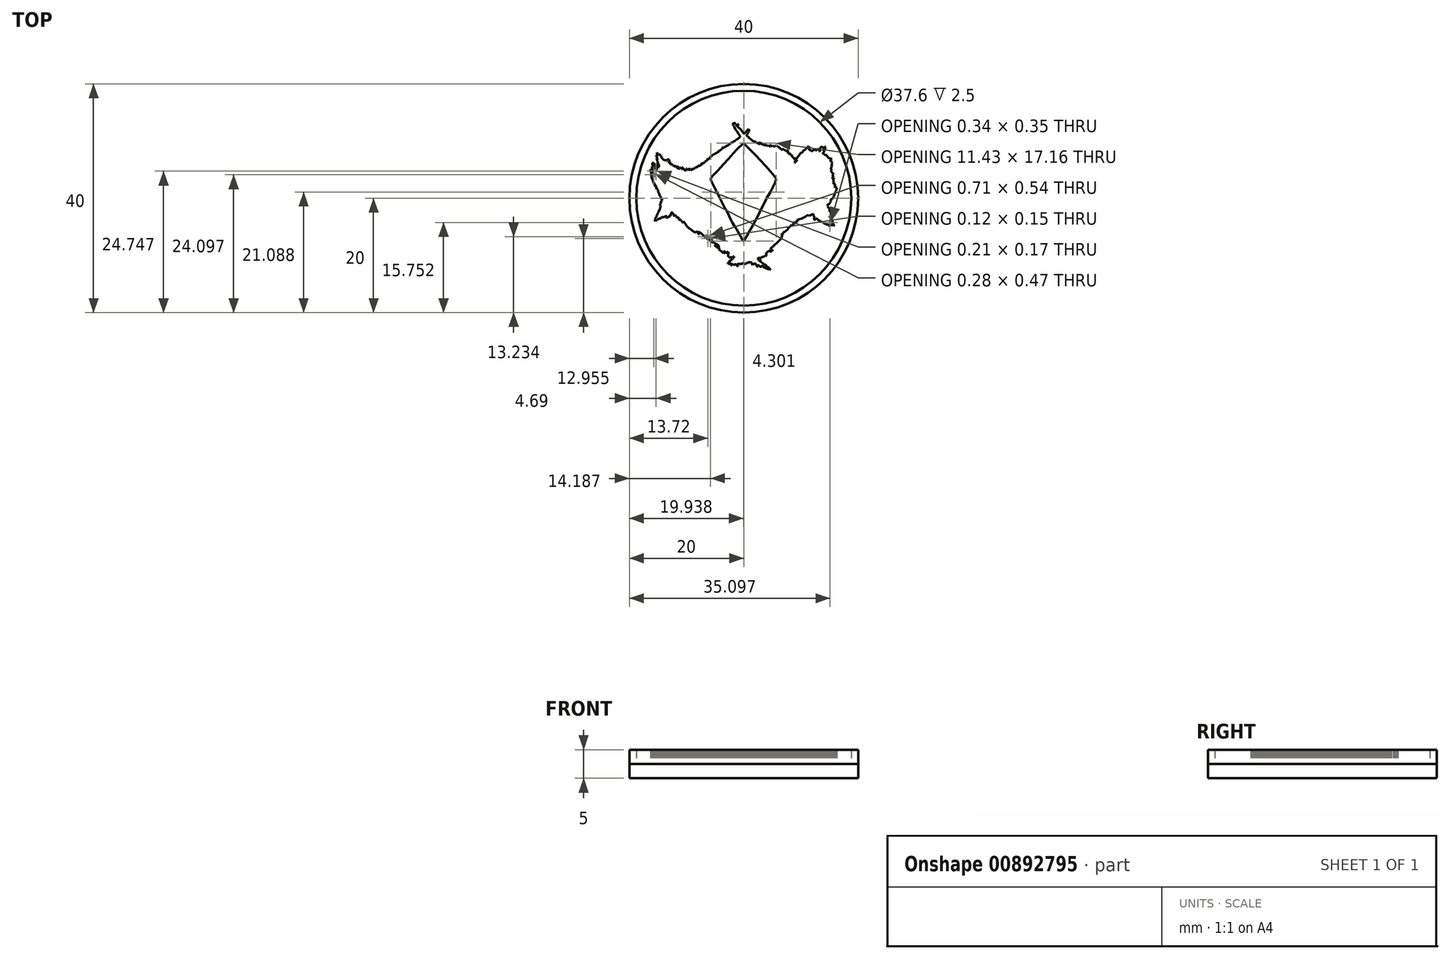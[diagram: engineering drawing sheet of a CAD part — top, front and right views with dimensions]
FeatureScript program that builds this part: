
annotation { "Feature Type Name" : "Feature", "Feature Type Description" : "" }
export const myFeature = defineFeature(function(context is Context, id is Id, definition is map)
    precondition{}
    {
        {
            var Q0;
            Q0=qCreatedBy(makeId("Top.planeOp"),FACE);
            var sketch = newSketch(context, id + "F0", { "sketchPlane" : qUnion([Q0])});
            skCircle(sketch, "E0", {"center": v(0, 0) * mm, "radius": 20 * mm});
            skLineSegment(sketch, "E1", {"start": v(-14.5, 0) * mm, "end": v(-14.54, 0.13) * mm});
            skLineSegment(sketch, "E2", {"start": v(-14.54, 0.13) * mm, "end": v(-14.54, 0.3) * mm});
            skLineSegment(sketch, "E3", {"start": v(-14.54, 0.3) * mm, "end": v(-14.71, 0.46) * mm});
            skLineSegment(sketch, "E4", {"start": v(-14.71, 0.46) * mm, "end": v(-14.74, 0.74) * mm});
            skLineSegment(sketch, "E5", {"start": v(-14.74, 0.74) * mm, "end": v(-14.94, 1.13) * mm});
            skLineSegment(sketch, "E6", {"start": v(-14.94, 1.13) * mm, "end": v(-14.94, 1.38) * mm});
            skLineSegment(sketch, "E7", {"start": v(-14.94, 1.38) * mm, "end": v(-15.19, 1.72) * mm});
            skLineSegment(sketch, "E8", {"start": v(-15.19, 1.72) * mm, "end": v(-15.27, 1.72) * mm});
            skLineSegment(sketch, "E9", {"start": v(-15.27, 1.72) * mm, "end": v(-15.39, 1.88) * mm});
            skLineSegment(sketch, "E10", {"start": v(-15.39, 1.88) * mm, "end": v(-15.39, 1.93) * mm});
            skLineSegment(sketch, "E11", {"start": v(-15.39, 1.93) * mm, "end": v(-15.35, 1.93) * mm});
            skLineSegment(sketch, "E12", {"start": v(-15.35, 1.93) * mm, "end": v(-15.31, 1.9) * mm});
            skLineSegment(sketch, "E13", {"start": v(-15.31, 1.9) * mm, "end": v(-15.28, 1.88) * mm});
            skLineSegment(sketch, "E14", {"start": v(-15.28, 1.88) * mm, "end": v(-15.3, 2) * mm});
            skLineSegment(sketch, "E15", {"start": v(-15.3, 2) * mm, "end": v(-15.39, 2.25) * mm});
            skLineSegment(sketch, "E16", {"start": v(-15.39, 2.25) * mm, "end": v(-15.5, 2.42) * mm});
            skLineSegment(sketch, "E17", {"start": v(-15.5, 2.42) * mm, "end": v(-15.53, 2.38) * mm});
            skLineSegment(sketch, "E18", {"start": v(-15.53, 2.38) * mm, "end": v(-15.5, 2.3) * mm});
            skLineSegment(sketch, "E19", {"start": v(-15.5, 2.3) * mm, "end": v(-15.43, 2.07) * mm});
            skLineSegment(sketch, "E20", {"start": v(-15.43, 2.07) * mm, "end": v(-15.49, 2.1) * mm});
            skLineSegment(sketch, "E21", {"start": v(-15.49, 2.1) * mm, "end": v(-15.77, 2.88) * mm});
            skLineSegment(sketch, "E22", {"start": v(-15.77, 2.88) * mm, "end": v(-16.12, 3.61) * mm});
            skLineSegment(sketch, "E23", {"start": v(-16.12, 3.61) * mm, "end": v(-16.1, 3.73) * mm});
            skLineSegment(sketch, "E24", {"start": v(-16.1, 3.73) * mm, "end": v(-16.09, 3.76) * mm});
            skLineSegment(sketch, "E25", {"start": v(-16.09, 3.76) * mm, "end": v(-16.09, 3.82) * mm});
            skLineSegment(sketch, "E26", {"start": v(-16.09, 3.82) * mm, "end": v(-16.2, 3.97) * mm});
            skLineSegment(sketch, "E27", {"start": v(-16.2, 3.97) * mm, "end": v(-16.2, 4.5) * mm});
            skLineSegment(sketch, "E28", {"start": v(-16.2, 4.5) * mm, "end": v(-16.28, 4.76) * mm});
            skLineSegment(sketch, "E29", {"start": v(-16.28, 4.76) * mm, "end": v(-16.3, 4.82) * mm});
            skLineSegment(sketch, "E30", {"start": v(-16.3, 4.82) * mm, "end": v(-16.26, 4.9) * mm});
            skLineSegment(sketch, "E31", {"start": v(-16.26, 4.9) * mm, "end": v(-16.21, 5.05) * mm});
            skLineSegment(sketch, "E32", {"start": v(-16.21, 5.05) * mm, "end": v(-16.16, 5.08) * mm});
            skLineSegment(sketch, "E33", {"start": v(-16.16, 5.08) * mm, "end": v(-16.07, 5.08) * mm});
            skLineSegment(sketch, "E34", {"start": v(-16.07, 5.08) * mm, "end": v(-16.02, 5.06) * mm});
            skLineSegment(sketch, "E35", {"start": v(-16.02, 5.06) * mm, "end": v(-16, 4.99) * mm});
            skLineSegment(sketch, "E36", {"start": v(-16, 4.99) * mm, "end": v(-16, 4.8) * mm});
            skLineSegment(sketch, "E37", {"start": v(-16, 4.8) * mm, "end": v(-16, 4.68) * mm});
            skLineSegment(sketch, "E38", {"start": v(-16, 4.68) * mm, "end": v(-15.94, 4.57) * mm});
            skLineSegment(sketch, "E39", {"start": v(-15.94, 4.57) * mm, "end": v(-15.87, 4.5) * mm});
            skLineSegment(sketch, "E40", {"start": v(-15.87, 4.5) * mm, "end": v(-15.84, 4.45) * mm});
            skLineSegment(sketch, "E41", {"start": v(-15.84, 4.45) * mm, "end": v(-15.81, 4.44) * mm});
            skLineSegment(sketch, "E42", {"start": v(-15.81, 4.44) * mm, "end": v(-15.8, 4.45) * mm});
            skLineSegment(sketch, "E43", {"start": v(-15.8, 4.45) * mm, "end": v(-15.8, 4.5) * mm});
            skLineSegment(sketch, "E44", {"start": v(-15.8, 4.5) * mm, "end": v(-15.83, 4.56) * mm});
            skLineSegment(sketch, "E45", {"start": v(-15.83, 4.56) * mm, "end": v(-15.87, 4.63) * mm});
            skLineSegment(sketch, "E46", {"start": v(-15.87, 4.63) * mm, "end": v(-15.89, 4.7) * mm});
            skLineSegment(sketch, "E47", {"start": v(-15.89, 4.7) * mm, "end": v(-15.91, 4.95) * mm});
            skLineSegment(sketch, "E48", {"start": v(-15.91, 4.95) * mm, "end": v(-15.94, 5.06) * mm});
            skLineSegment(sketch, "E49", {"start": v(-15.94, 5.06) * mm, "end": v(-16, 5.15) * mm});
            skLineSegment(sketch, "E50", {"start": v(-16, 5.15) * mm, "end": v(-16.11, 5.25) * mm});
            skLineSegment(sketch, "E51", {"start": v(-16.11, 5.25) * mm, "end": v(-16.14, 5.31) * mm});
            skLineSegment(sketch, "E52", {"start": v(-16.14, 5.31) * mm, "end": v(-16.1, 5.37) * mm});
            skLineSegment(sketch, "E53", {"start": v(-16.1, 5.37) * mm, "end": v(-16.06, 5.43) * mm});
            skLineSegment(sketch, "E54", {"start": v(-16.06, 5.43) * mm, "end": v(-16.03, 5.44) * mm});
            skLineSegment(sketch, "E55", {"start": v(-16.03, 5.44) * mm, "end": v(-15.99, 5.44) * mm});
            skLineSegment(sketch, "E56", {"start": v(-15.99, 5.44) * mm, "end": v(-15.97, 5.4) * mm});
            skLineSegment(sketch, "E57", {"start": v(-15.97, 5.4) * mm, "end": v(-15.9, 5.33) * mm});
            skLineSegment(sketch, "E58", {"start": v(-15.9, 5.33) * mm, "end": v(-15.87, 5.3) * mm});
            skLineSegment(sketch, "E59", {"start": v(-15.87, 5.3) * mm, "end": v(-15.84, 5.29) * mm});
            skLineSegment(sketch, "E60", {"start": v(-15.84, 5.29) * mm, "end": v(-15.81, 5.28) * mm});
            skLineSegment(sketch, "E61", {"start": v(-15.81, 5.28) * mm, "end": v(-15.78, 5.3) * mm});
            skLineSegment(sketch, "E62", {"start": v(-15.78, 5.3) * mm, "end": v(-15.77, 5.3) * mm});
            skLineSegment(sketch, "E63", {"start": v(-15.77, 5.3) * mm, "end": v(-15.76, 5.35) * mm});
            skLineSegment(sketch, "E64", {"start": v(-15.76, 5.35) * mm, "end": v(-15.75, 5.43) * mm});
            skLineSegment(sketch, "E65", {"start": v(-15.75, 5.43) * mm, "end": v(-15.73, 5.45) * mm});
            skLineSegment(sketch, "E66", {"start": v(-15.73, 5.45) * mm, "end": v(-15.72, 5.48) * mm});
            skLineSegment(sketch, "E67", {"start": v(-15.72, 5.48) * mm, "end": v(-15.72, 5.51) * mm});
            skLineSegment(sketch, "E68", {"start": v(-15.72, 5.51) * mm, "end": v(-15.72, 5.54) * mm});
            skLineSegment(sketch, "E69", {"start": v(-15.72, 5.54) * mm, "end": v(-15.73, 5.58) * mm});
            skLineSegment(sketch, "E70", {"start": v(-15.73, 5.58) * mm, "end": v(-15.78, 5.62) * mm});
            skLineSegment(sketch, "E71", {"start": v(-15.78, 5.62) * mm, "end": v(-15.84, 5.67) * mm});
            skLineSegment(sketch, "E72", {"start": v(-15.84, 5.67) * mm, "end": v(-15.9, 5.7) * mm});
            skLineSegment(sketch, "E73", {"start": v(-15.9, 5.7) * mm, "end": v(-15.93, 5.74) * mm});
            skLineSegment(sketch, "E74", {"start": v(-15.93, 5.74) * mm, "end": v(-15.95, 5.78) * mm});
            skLineSegment(sketch, "E75", {"start": v(-15.95, 5.78) * mm, "end": v(-15.98, 5.84) * mm});
            skLineSegment(sketch, "E76", {"start": v(-15.98, 5.84) * mm, "end": v(-15.99, 5.89) * mm});
            skLineSegment(sketch, "E77", {"start": v(-15.99, 5.89) * mm, "end": v(-16, 5.94) * mm});
            skLineSegment(sketch, "E78", {"start": v(-16, 5.94) * mm, "end": v(-16, 5.98) * mm});
            skLineSegment(sketch, "E79", {"start": v(-16, 5.98) * mm, "end": v(-15.99, 6.03) * mm});
            skLineSegment(sketch, "E80", {"start": v(-15.99, 6.03) * mm, "end": v(-15.97, 6.08) * mm});
            skLineSegment(sketch, "E81", {"start": v(-15.97, 6.08) * mm, "end": v(-15.95, 6.13) * mm});
            skLineSegment(sketch, "E82", {"start": v(-15.95, 6.13) * mm, "end": v(-15.95, 6.16) * mm});
            skLineSegment(sketch, "E83", {"start": v(-15.95, 6.16) * mm, "end": v(-15.93, 6.18) * mm});
            skLineSegment(sketch, "E84", {"start": v(-15.93, 6.18) * mm, "end": v(-15.9, 6.2) * mm});
            skLineSegment(sketch, "E85", {"start": v(-15.9, 6.2) * mm, "end": v(-15.87, 6.2) * mm});
            skLineSegment(sketch, "E86", {"start": v(-15.87, 6.2) * mm, "end": v(-15.84, 6.19) * mm});
            skLineSegment(sketch, "E87", {"start": v(-15.84, 6.19) * mm, "end": v(-15.83, 6.18) * mm});
            skLineSegment(sketch, "E88", {"start": v(-15.83, 6.18) * mm, "end": v(-15.79, 6.16) * mm});
            skLineSegment(sketch, "E89", {"start": v(-15.79, 6.16) * mm, "end": v(-15.73, 6.12) * mm});
            skLineSegment(sketch, "E90", {"start": v(-15.73, 6.12) * mm, "end": v(-15.68, 6.09) * mm});
            skLineSegment(sketch, "E91", {"start": v(-15.68, 6.09) * mm, "end": v(-15.64, 6.05) * mm});
            skLineSegment(sketch, "E92", {"start": v(-15.64, 6.05) * mm, "end": v(-15.6, 6.01) * mm});
            skLineSegment(sketch, "E93", {"start": v(-15.6, 6.01) * mm, "end": v(-15.58, 5.97) * mm});
            skLineSegment(sketch, "E94", {"start": v(-15.58, 5.97) * mm, "end": v(-15.57, 5.92) * mm});
            skLineSegment(sketch, "E95", {"start": v(-15.57, 5.92) * mm, "end": v(-15.57, 5.86) * mm});
            skLineSegment(sketch, "E96", {"start": v(-15.57, 5.86) * mm, "end": v(-15.58, 5.79) * mm});
            skLineSegment(sketch, "E97", {"start": v(-15.58, 5.79) * mm, "end": v(-15.6, 5.74) * mm});
            skLineSegment(sketch, "E98", {"start": v(-15.6, 5.74) * mm, "end": v(-15.62, 5.7) * mm});
            skLineSegment(sketch, "E99", {"start": v(-15.62, 5.7) * mm, "end": v(-15.63, 5.63) * mm});
            skLineSegment(sketch, "E100", {"start": v(-15.63, 5.63) * mm, "end": v(-15.63, 5.6) * mm});
            skLineSegment(sketch, "E101", {"start": v(-15.63, 5.6) * mm, "end": v(-15.62, 5.57) * mm});
            skLineSegment(sketch, "E102", {"start": v(-15.62, 5.57) * mm, "end": v(-15.61, 5.52) * mm});
            skLineSegment(sketch, "E103", {"start": v(-15.61, 5.52) * mm, "end": v(-15.62, 5.45) * mm});
            skLineSegment(sketch, "E104", {"start": v(-15.62, 5.45) * mm, "end": v(-15.6, 5.4) * mm});
            skLineSegment(sketch, "E105", {"start": v(-15.6, 5.4) * mm, "end": v(-15.58, 5.38) * mm});
            skLineSegment(sketch, "E106", {"start": v(-15.58, 5.38) * mm, "end": v(-15.57, 5.36) * mm});
            skLineSegment(sketch, "E107", {"start": v(-15.57, 5.36) * mm, "end": v(-15.55, 5.35) * mm});
            skLineSegment(sketch, "E108", {"start": v(-15.55, 5.35) * mm, "end": v(-15.58, 5.34) * mm});
            skLineSegment(sketch, "E109", {"start": v(-15.58, 5.34) * mm, "end": v(-15.59, 5.33) * mm});
            skLineSegment(sketch, "E110", {"start": v(-15.59, 5.33) * mm, "end": v(-15.6, 5.3) * mm});
            skLineSegment(sketch, "E111", {"start": v(-15.6, 5.3) * mm, "end": v(-15.58, 5.28) * mm});
            skLineSegment(sketch, "E112", {"start": v(-15.58, 5.28) * mm, "end": v(-15.57, 5.27) * mm});
            skLineSegment(sketch, "E113", {"start": v(-15.57, 5.27) * mm, "end": v(-15.55, 5.26) * mm});
            skLineSegment(sketch, "E114", {"start": v(-15.55, 5.26) * mm, "end": v(-15.54, 5.27) * mm});
            skLineSegment(sketch, "E115", {"start": v(-15.54, 5.27) * mm, "end": v(-15.53, 5.27) * mm});
            skLineSegment(sketch, "E116", {"start": v(-15.53, 5.27) * mm, "end": v(-15.52, 5.3) * mm});
            skLineSegment(sketch, "E117", {"start": v(-15.52, 5.3) * mm, "end": v(-15.52, 5.3) * mm});
            skLineSegment(sketch, "E118", {"start": v(-15.52, 5.3) * mm, "end": v(-15.5, 5.3) * mm});
            skLineSegment(sketch, "E119", {"start": v(-15.5, 5.3) * mm, "end": v(-15.5, 5.3) * mm});
            skLineSegment(sketch, "E120", {"start": v(-15.5, 5.3) * mm, "end": v(-15.49, 5.28) * mm});
            skLineSegment(sketch, "E121", {"start": v(-15.49, 5.28) * mm, "end": v(-15.48, 5.28) * mm});
            skLineSegment(sketch, "E122", {"start": v(-15.48, 5.28) * mm, "end": v(-15.46, 5.27) * mm});
            skLineSegment(sketch, "E123", {"start": v(-15.46, 5.27) * mm, "end": v(-15.46, 5.26) * mm});
            skLineSegment(sketch, "E124", {"start": v(-15.46, 5.26) * mm, "end": v(-15.44, 5.23) * mm});
            skLineSegment(sketch, "E125", {"start": v(-15.44, 5.23) * mm, "end": v(-15.42, 5.22) * mm});
            skLineSegment(sketch, "E126", {"start": v(-15.42, 5.22) * mm, "end": v(-15.4, 5.1) * mm});
            skLineSegment(sketch, "E127", {"start": v(-15.4, 5.1) * mm, "end": v(-15.39, 5.05) * mm});
            skLineSegment(sketch, "E128", {"start": v(-15.39, 5.05) * mm, "end": v(-15.37, 5.03) * mm});
            skLineSegment(sketch, "E129", {"start": v(-15.37, 5.03) * mm, "end": v(-15.35, 5.02) * mm});
            skLineSegment(sketch, "E130", {"start": v(-15.35, 5.02) * mm, "end": v(-15.32, 5.03) * mm});
            skLineSegment(sketch, "E131", {"start": v(-15.32, 5.03) * mm, "end": v(-15.32, 5.04) * mm});
            skLineSegment(sketch, "E132", {"start": v(-15.32, 5.04) * mm, "end": v(-15.32, 5.06) * mm});
            skLineSegment(sketch, "E133", {"start": v(-15.32, 5.06) * mm, "end": v(-15.34, 5.06) * mm});
            skLineSegment(sketch, "E134", {"start": v(-15.34, 5.06) * mm, "end": v(-15.35, 5.07) * mm});
            skLineSegment(sketch, "E135", {"start": v(-15.35, 5.07) * mm, "end": v(-15.35, 5.08) * mm});
            skLineSegment(sketch, "E136", {"start": v(-15.35, 5.08) * mm, "end": v(-15.35, 5.1) * mm});
            skLineSegment(sketch, "E137", {"start": v(-15.35, 5.1) * mm, "end": v(-15.33, 5.1) * mm});
            skLineSegment(sketch, "E138", {"start": v(-15.33, 5.1) * mm, "end": v(-15.3, 5.1) * mm});
            skLineSegment(sketch, "E139", {"start": v(-15.3, 5.1) * mm, "end": v(-15.3, 5.09) * mm});
            skLineSegment(sketch, "E140", {"start": v(-15.3, 5.09) * mm, "end": v(-15.28, 5.08) * mm});
            skLineSegment(sketch, "E141", {"start": v(-15.28, 5.08) * mm, "end": v(-15.27, 5.06) * mm});
            skLineSegment(sketch, "E142", {"start": v(-15.27, 5.06) * mm, "end": v(-15.25, 5.06) * mm});
            skLineSegment(sketch, "E143", {"start": v(-15.25, 5.06) * mm, "end": v(-15.23, 5.05) * mm});
            skLineSegment(sketch, "E144", {"start": v(-15.23, 5.05) * mm, "end": v(-15.21, 5.03) * mm});
            skLineSegment(sketch, "E145", {"start": v(-15.21, 5.03) * mm, "end": v(-15.2, 5.02) * mm});
            skLineSegment(sketch, "E146", {"start": v(-15.2, 5.02) * mm, "end": v(-15.15, 5.02) * mm});
            skLineSegment(sketch, "E147", {"start": v(-15.15, 5.02) * mm, "end": v(-15.14, 5.02) * mm});
            skLineSegment(sketch, "E148", {"start": v(-15.14, 5.02) * mm, "end": v(-15.13, 5.04) * mm});
            skLineSegment(sketch, "E149", {"start": v(-15.13, 5.04) * mm, "end": v(-15.13, 5.05) * mm});
            skLineSegment(sketch, "E150", {"start": v(-15.13, 5.05) * mm, "end": v(-15.13, 5.07) * mm});
            skLineSegment(sketch, "E151", {"start": v(-15.13, 5.07) * mm, "end": v(-15.14, 5.08) * mm});
            skLineSegment(sketch, "E152", {"start": v(-15.14, 5.08) * mm, "end": v(-15.15, 5.1) * mm});
            skLineSegment(sketch, "E153", {"start": v(-15.15, 5.1) * mm, "end": v(-15.19, 5.12) * mm});
            skLineSegment(sketch, "E154", {"start": v(-15.19, 5.12) * mm, "end": v(-15.2, 5.14) * mm});
            skLineSegment(sketch, "E155", {"start": v(-15.2, 5.14) * mm, "end": v(-15.2, 5.18) * mm});
            skLineSegment(sketch, "E156", {"start": v(-15.2, 5.18) * mm, "end": v(-15.2, 5.22) * mm});
            skLineSegment(sketch, "E157", {"start": v(-15.2, 5.22) * mm, "end": v(-15.2, 5.25) * mm});
            skLineSegment(sketch, "E158", {"start": v(-15.2, 5.25) * mm, "end": v(-15.2, 5.28) * mm});
            skLineSegment(sketch, "E159", {"start": v(-15.2, 5.28) * mm, "end": v(-15.2, 5.3) * mm});
            skLineSegment(sketch, "E160", {"start": v(-15.2, 5.3) * mm, "end": v(-15.24, 5.36) * mm});
            skLineSegment(sketch, "E161", {"start": v(-15.24, 5.36) * mm, "end": v(-15.26, 5.4) * mm});
            skLineSegment(sketch, "E162", {"start": v(-15.26, 5.4) * mm, "end": v(-15.28, 5.47) * mm});
            skLineSegment(sketch, "E163", {"start": v(-15.28, 5.47) * mm, "end": v(-15.3, 5.53) * mm});
            skLineSegment(sketch, "E164", {"start": v(-15.3, 5.53) * mm, "end": v(-15.3, 5.56) * mm});
            skLineSegment(sketch, "E165", {"start": v(-15.3, 5.56) * mm, "end": v(-15.33, 5.6) * mm});
            skLineSegment(sketch, "E166", {"start": v(-15.33, 5.6) * mm, "end": v(-15.34, 5.63) * mm});
            skLineSegment(sketch, "E167", {"start": v(-15.34, 5.63) * mm, "end": v(-15.34, 5.66) * mm});
            skLineSegment(sketch, "E168", {"start": v(-15.34, 5.66) * mm, "end": v(-15.33, 5.69) * mm});
            skLineSegment(sketch, "E169", {"start": v(-15.33, 5.69) * mm, "end": v(-15.32, 5.7) * mm});
            skLineSegment(sketch, "E170", {"start": v(-15.32, 5.7) * mm, "end": v(-15.28, 5.73) * mm});
            skLineSegment(sketch, "E171", {"start": v(-15.28, 5.73) * mm, "end": v(-15.25, 5.75) * mm});
            skLineSegment(sketch, "E172", {"start": v(-15.25, 5.75) * mm, "end": v(-15.19, 5.75) * mm});
            skLineSegment(sketch, "E173", {"start": v(-15.19, 5.75) * mm, "end": v(-15.17, 5.75) * mm});
            skLineSegment(sketch, "E174", {"start": v(-15.17, 5.75) * mm, "end": v(-15.13, 5.72) * mm});
            skLineSegment(sketch, "E175", {"start": v(-15.13, 5.72) * mm, "end": v(-15.12, 5.7) * mm});
            skLineSegment(sketch, "E176", {"start": v(-15.12, 5.7) * mm, "end": v(-15.1, 5.62) * mm});
            skLineSegment(sketch, "E177", {"start": v(-15.1, 5.62) * mm, "end": v(-15.09, 5.59) * mm});
            skLineSegment(sketch, "E178", {"start": v(-15.09, 5.59) * mm, "end": v(-15.03, 5.53) * mm});
            skLineSegment(sketch, "E179", {"start": v(-15.03, 5.53) * mm, "end": v(-14.97, 5.52) * mm});
            skLineSegment(sketch, "E180", {"start": v(-14.97, 5.52) * mm, "end": v(-14.9, 5.47) * mm});
            skLineSegment(sketch, "E181", {"start": v(-14.9, 5.47) * mm, "end": v(-14.85, 5.44) * mm});
            skLineSegment(sketch, "E182", {"start": v(-14.85, 5.44) * mm, "end": v(-14.8, 5.43) * mm});
            skLineSegment(sketch, "E183", {"start": v(-14.8, 5.43) * mm, "end": v(-14.8, 5.44) * mm});
            skLineSegment(sketch, "E184", {"start": v(-14.8, 5.44) * mm, "end": v(-14.8, 5.6) * mm});
            skLineSegment(sketch, "E185", {"start": v(-14.8, 5.6) * mm, "end": v(-14.84, 5.75) * mm});
            skLineSegment(sketch, "E186", {"start": v(-14.84, 5.75) * mm, "end": v(-14.9, 5.92) * mm});
            skLineSegment(sketch, "E187", {"start": v(-14.9, 5.92) * mm, "end": v(-14.94, 6.02) * mm});
            skLineSegment(sketch, "E188", {"start": v(-14.94, 6.02) * mm, "end": v(-15, 6.16) * mm});
            skLineSegment(sketch, "E189", {"start": v(-15, 6.16) * mm, "end": v(-15.03, 6.2) * mm});
            skLineSegment(sketch, "E190", {"start": v(-15.03, 6.2) * mm, "end": v(-15.04, 6.28) * mm});
            skLineSegment(sketch, "E191", {"start": v(-15.04, 6.28) * mm, "end": v(-15.03, 6.33) * mm});
            skLineSegment(sketch, "E192", {"start": v(-15.03, 6.33) * mm, "end": v(-15.04, 6.4) * mm});
            skLineSegment(sketch, "E193", {"start": v(-15.04, 6.4) * mm, "end": v(-15.07, 6.45) * mm});
            skLineSegment(sketch, "E194", {"start": v(-15.07, 6.45) * mm, "end": v(-15.13, 6.51) * mm});
            skLineSegment(sketch, "E195", {"start": v(-15.13, 6.51) * mm, "end": v(-15.14, 6.56) * mm});
            skLineSegment(sketch, "E196", {"start": v(-15.14, 6.56) * mm, "end": v(-15.15, 6.71) * mm});
            skLineSegment(sketch, "E197", {"start": v(-15.15, 6.71) * mm, "end": v(-15.16, 6.78) * mm});
            skLineSegment(sketch, "E198", {"start": v(-15.16, 6.78) * mm, "end": v(-15.19, 6.82) * mm});
            skLineSegment(sketch, "E199", {"start": v(-15.19, 6.82) * mm, "end": v(-15.2, 6.86) * mm});
            skLineSegment(sketch, "E200", {"start": v(-15.2, 6.86) * mm, "end": v(-15.2, 6.87) * mm});
            skLineSegment(sketch, "E201", {"start": v(-15.2, 6.87) * mm, "end": v(-15.19, 6.89) * mm});
            skLineSegment(sketch, "E202", {"start": v(-15.19, 6.89) * mm, "end": v(-15.16, 6.89) * mm});
            skLineSegment(sketch, "E203", {"start": v(-15.16, 6.89) * mm, "end": v(-15.15, 6.84) * mm});
            skLineSegment(sketch, "E204", {"start": v(-15.15, 6.84) * mm, "end": v(-15.13, 6.83) * mm});
            skLineSegment(sketch, "E205", {"start": v(-15.13, 6.83) * mm, "end": v(-15.1, 6.8) * mm});
            skLineSegment(sketch, "E206", {"start": v(-15.1, 6.8) * mm, "end": v(-15.1, 6.8) * mm});
            skLineSegment(sketch, "E207", {"start": v(-15.1, 6.8) * mm, "end": v(-15.09, 6.8) * mm});
            skLineSegment(sketch, "E208", {"start": v(-15.09, 6.8) * mm, "end": v(-15.09, 6.82) * mm});
            skLineSegment(sketch, "E209", {"start": v(-15.09, 6.82) * mm, "end": v(-15.09, 6.84) * mm});
            skLineSegment(sketch, "E210", {"start": v(-15.09, 6.84) * mm, "end": v(-15.1, 6.86) * mm});
            skLineSegment(sketch, "E211", {"start": v(-15.1, 6.86) * mm, "end": v(-15.12, 6.89) * mm});
            skLineSegment(sketch, "E212", {"start": v(-15.12, 6.89) * mm, "end": v(-15.17, 6.99) * mm});
            skLineSegment(sketch, "E213", {"start": v(-15.17, 6.99) * mm, "end": v(-15.2, 7.14) * mm});
            skLineSegment(sketch, "E214", {"start": v(-15.2, 7.14) * mm, "end": v(-15.24, 7.29) * mm});
            skLineSegment(sketch, "E215", {"start": v(-15.24, 7.29) * mm, "end": v(-15.26, 7.35) * mm});
            skLineSegment(sketch, "E216", {"start": v(-15.26, 7.35) * mm, "end": v(-15.3, 7.42) * mm});
            skLineSegment(sketch, "E217", {"start": v(-15.3, 7.42) * mm, "end": v(-15.33, 7.43) * mm});
            skLineSegment(sketch, "E218", {"start": v(-15.33, 7.43) * mm, "end": v(-15.32, 7.46) * mm});
            skLineSegment(sketch, "E219", {"start": v(-15.32, 7.46) * mm, "end": v(-15.28, 7.47) * mm});
            skLineSegment(sketch, "E220", {"start": v(-15.28, 7.47) * mm, "end": v(-15.22, 7.4) * mm});
            skLineSegment(sketch, "E221", {"start": v(-15.22, 7.4) * mm, "end": v(-15.18, 7.4) * mm});
            skLineSegment(sketch, "E222", {"start": v(-15.18, 7.4) * mm, "end": v(-15.14, 7.44) * mm});
            skLineSegment(sketch, "E223", {"start": v(-15.14, 7.44) * mm, "end": v(-15.1, 7.46) * mm});
            skLineSegment(sketch, "E224", {"start": v(-15.1, 7.46) * mm, "end": v(-15.1, 7.54) * mm});
            skLineSegment(sketch, "E225", {"start": v(-15.1, 7.54) * mm, "end": v(-15.13, 7.6) * mm});
            skLineSegment(sketch, "E226", {"start": v(-15.13, 7.6) * mm, "end": v(-15.17, 7.72) * mm});
            skLineSegment(sketch, "E227", {"start": v(-15.17, 7.72) * mm, "end": v(-15.17, 7.81) * mm});
            skLineSegment(sketch, "E228", {"start": v(-15.17, 7.81) * mm, "end": v(-15.22, 7.88) * mm});
            skLineSegment(sketch, "E229", {"start": v(-15.22, 7.88) * mm, "end": v(-15.2, 7.91) * mm});
            skLineSegment(sketch, "E230", {"start": v(-15.2, 7.91) * mm, "end": v(-15.12, 7.86) * mm});
            skLineSegment(sketch, "E231", {"start": v(-15.12, 7.86) * mm, "end": v(-15.01, 7.78) * mm});
            skLineSegment(sketch, "E232", {"start": v(-15.01, 7.78) * mm, "end": v(-14.94, 7.7) * mm});
            skLineSegment(sketch, "E233", {"start": v(-14.94, 7.7) * mm, "end": v(-14.89, 7.63) * mm});
            skLineSegment(sketch, "E234", {"start": v(-14.89, 7.63) * mm, "end": v(-14.86, 7.62) * mm});
            skLineSegment(sketch, "E235", {"start": v(-14.86, 7.62) * mm, "end": v(-14.86, 7.67) * mm});
            skLineSegment(sketch, "E236", {"start": v(-14.86, 7.67) * mm, "end": v(-14.84, 7.69) * mm});
            skLineSegment(sketch, "E237", {"start": v(-15.81, 4.21) * mm, "end": v(-15.84, 4.26) * mm});
            skLineSegment(sketch, "E238", {"start": v(-15.84, 4.26) * mm, "end": v(-15.84, 4.3) * mm});
            skLineSegment(sketch, "E239", {"start": v(-15.84, 4.3) * mm, "end": v(-15.8, 4.33) * mm});
            skLineSegment(sketch, "E240", {"start": v(-15.8, 4.33) * mm, "end": v(-15.75, 4.31) * mm});
            skLineSegment(sketch, "E241", {"start": v(-15.75, 4.31) * mm, "end": v(-15.67, 4.2) * mm});
            skLineSegment(sketch, "E242", {"start": v(-15.67, 4.2) * mm, "end": v(-15.6, 4.03) * mm});
            skLineSegment(sketch, "E243", {"start": v(-15.6, 4.03) * mm, "end": v(-15.56, 3.86) * mm});
            skLineSegment(sketch, "E244", {"start": v(-15.56, 3.86) * mm, "end": v(-15.59, 3.87) * mm});
            skLineSegment(sketch, "E245", {"start": v(-15.59, 3.87) * mm, "end": v(-15.68, 4.04) * mm});
            skLineSegment(sketch, "E246", {"start": v(-15.68, 4.04) * mm, "end": v(-15.74, 4.13) * mm});
            skLineSegment(sketch, "E247", {"start": v(-15.74, 4.13) * mm, "end": v(-15.79, 4.18) * mm});
            skLineSegment(sketch, "E248", {"start": v(-15.79, 4.18) * mm, "end": v(-15.81, 4.21) * mm});
            skLineSegment(sketch, "E249", {"start": v(-15.21, 4.66) * mm, "end": v(-15.33, 4.67) * mm});
            skLineSegment(sketch, "E250", {"start": v(-15.33, 4.67) * mm, "end": v(-15.39, 4.7) * mm});
            skLineSegment(sketch, "E251", {"start": v(-15.39, 4.7) * mm, "end": v(-15.41, 4.74) * mm});
            skLineSegment(sketch, "E252", {"start": v(-15.41, 4.74) * mm, "end": v(-15.41, 4.8) * mm});
            skLineSegment(sketch, "E253", {"start": v(-15.41, 4.8) * mm, "end": v(-15.39, 4.83) * mm});
            skLineSegment(sketch, "E254", {"start": v(-15.39, 4.83) * mm, "end": v(-15.32, 4.83) * mm});
            skLineSegment(sketch, "E255", {"start": v(-15.32, 4.83) * mm, "end": v(-15.28, 4.8) * mm});
            skLineSegment(sketch, "E256", {"start": v(-15.28, 4.8) * mm, "end": v(-15.24, 4.75) * mm});
            skLineSegment(sketch, "E257", {"start": v(-15.24, 4.75) * mm, "end": v(-15.2, 4.7) * mm});
            skLineSegment(sketch, "E258", {"start": v(-15.2, 4.7) * mm, "end": v(-15.21, 4.66) * mm});
            skLineSegment(sketch, "E259", {"start": v(-14.84, 7.69) * mm, "end": v(-14.78, 7.6) * mm});
            skLineSegment(sketch, "E260", {"start": v(-14.78, 7.6) * mm, "end": v(-14.75, 7.62) * mm});
            skLineSegment(sketch, "E261", {"start": v(-14.75, 7.62) * mm, "end": v(-14.77, 7.69) * mm});
            skLineSegment(sketch, "E262", {"start": v(-14.77, 7.69) * mm, "end": v(-14.74, 7.7) * mm});
            skLineSegment(sketch, "E263", {"start": v(-14.74, 7.7) * mm, "end": v(-14.68, 7.66) * mm});
            skLineSegment(sketch, "E264", {"start": v(-14.68, 7.66) * mm, "end": v(-14.6, 7.58) * mm});
            skLineSegment(sketch, "E265", {"start": v(-14.6, 7.58) * mm, "end": v(-14.58, 7.5) * mm});
            skLineSegment(sketch, "E266", {"start": v(-14.58, 7.5) * mm, "end": v(-14.48, 7.38) * mm});
            skLineSegment(sketch, "E267", {"start": v(-14.48, 7.38) * mm, "end": v(-14.43, 7.35) * mm});
            skLineSegment(sketch, "E268", {"start": v(-14.43, 7.35) * mm, "end": v(-14.4, 7.26) * mm});
            skLineSegment(sketch, "E269", {"start": v(-14.4, 7.26) * mm, "end": v(-14.32, 7.1) * mm});
            skLineSegment(sketch, "E270", {"start": v(-14.32, 7.1) * mm, "end": v(-14.28, 7) * mm});
            skLineSegment(sketch, "E271", {"start": v(-14.28, 7) * mm, "end": v(-14.22, 6.97) * mm});
            skLineSegment(sketch, "E272", {"start": v(-14.22, 6.97) * mm, "end": v(-14.19, 6.87) * mm});
            skLineSegment(sketch, "E273", {"start": v(-14.19, 6.87) * mm, "end": v(-14.13, 6.8) * mm});
            skLineSegment(sketch, "E274", {"start": v(-14.13, 6.8) * mm, "end": v(-14.02, 6.8) * mm});
            skLineSegment(sketch, "E275", {"start": v(-14.02, 6.8) * mm, "end": v(-14, 6.76) * mm});
            skLineSegment(sketch, "E276", {"start": v(-14, 6.76) * mm, "end": v(-14.03, 6.72) * mm});
            skLineSegment(sketch, "E277", {"start": v(-14.03, 6.72) * mm, "end": v(-14, 6.68) * mm});
            skLineSegment(sketch, "E278", {"start": v(-14, 6.68) * mm, "end": v(-13.97, 6.64) * mm});
            skLineSegment(sketch, "E279", {"start": v(-13.97, 6.64) * mm, "end": v(-13.93, 6.65) * mm});
            skLineSegment(sketch, "E280", {"start": v(-13.93, 6.65) * mm, "end": v(-13.88, 6.7) * mm});
            skLineSegment(sketch, "E281", {"start": v(-13.88, 6.7) * mm, "end": v(-13.8, 6.73) * mm});
            skLineSegment(sketch, "E282", {"start": v(-13.8, 6.73) * mm, "end": v(-13.78, 6.77) * mm});
            skLineSegment(sketch, "E283", {"start": v(-13.78, 6.77) * mm, "end": v(-13.73, 6.78) * mm});
            skLineSegment(sketch, "E284", {"start": v(-13.73, 6.78) * mm, "end": v(-13.7, 6.73) * mm});
            skLineSegment(sketch, "E285", {"start": v(-13.7, 6.73) * mm, "end": v(-13.66, 6.67) * mm});
            skLineSegment(sketch, "E286", {"start": v(-13.66, 6.67) * mm, "end": v(-13.62, 6.62) * mm});
            skLineSegment(sketch, "E287", {"start": v(-13.62, 6.62) * mm, "end": v(-13.58, 6.6) * mm});
            skLineSegment(sketch, "E288", {"start": v(-13.58, 6.6) * mm, "end": v(-13.56, 6.62) * mm});
            skLineSegment(sketch, "E289", {"start": v(-13.56, 6.62) * mm, "end": v(-13.55, 6.76) * mm});
            skLineSegment(sketch, "E290", {"start": v(-13.55, 6.76) * mm, "end": v(-13.5, 6.77) * mm});
            skLineSegment(sketch, "E291", {"start": v(-13.5, 6.77) * mm, "end": v(-13.47, 6.73) * mm});
            skLineSegment(sketch, "E292", {"start": v(-13.47, 6.73) * mm, "end": v(-13.44, 6.67) * mm});
            skLineSegment(sketch, "E293", {"start": v(-13.44, 6.67) * mm, "end": v(-13.43, 6.63) * mm});
            skLineSegment(sketch, "E294", {"start": v(-13.43, 6.63) * mm, "end": v(-13.4, 6.62) * mm});
            skLineSegment(sketch, "E295", {"start": v(-13.4, 6.62) * mm, "end": v(-13.39, 6.63) * mm});
            skLineSegment(sketch, "E296", {"start": v(-13.39, 6.63) * mm, "end": v(-13.38, 6.72) * mm});
            skLineSegment(sketch, "E297", {"start": v(-13.38, 6.72) * mm, "end": v(-13.36, 6.73) * mm});
            skLineSegment(sketch, "E298", {"start": v(-13.36, 6.73) * mm, "end": v(-13.36, 6.75) * mm});
            skLineSegment(sketch, "E299", {"start": v(-13.36, 6.75) * mm, "end": v(-13.39, 6.79) * mm});
            skLineSegment(sketch, "E300", {"start": v(-13.39, 6.79) * mm, "end": v(-13.4, 6.82) * mm});
            skLineSegment(sketch, "E301", {"start": v(-13.4, 6.82) * mm, "end": v(-13.38, 6.84) * mm});
            skLineSegment(sketch, "E302", {"start": v(-13.38, 6.84) * mm, "end": v(-13.31, 6.77) * mm});
            skLineSegment(sketch, "E303", {"start": v(-13.31, 6.77) * mm, "end": v(-13.28, 6.79) * mm});
            skLineSegment(sketch, "E304", {"start": v(-13.28, 6.79) * mm, "end": v(-13.24, 6.8) * mm});
            skLineSegment(sketch, "E305", {"start": v(-13.24, 6.8) * mm, "end": v(-13.18, 6.78) * mm});
            skLineSegment(sketch, "E306", {"start": v(-13.18, 6.78) * mm, "end": v(-13.16, 6.76) * mm});
            skLineSegment(sketch, "E307", {"start": v(-13.16, 6.76) * mm, "end": v(-13.12, 6.77) * mm});
            skLineSegment(sketch, "E308", {"start": v(-13.12, 6.77) * mm, "end": v(-13.09, 6.8) * mm});
            skLineSegment(sketch, "E309", {"start": v(-13.09, 6.8) * mm, "end": v(-13.05, 6.81) * mm});
            skLineSegment(sketch, "E310", {"start": v(-13.05, 6.81) * mm, "end": v(-13.02, 6.78) * mm});
            skLineSegment(sketch, "E311", {"start": v(-13.02, 6.78) * mm, "end": v(-13.04, 6.76) * mm});
            skLineSegment(sketch, "E312", {"start": v(-13.04, 6.76) * mm, "end": v(-13.07, 6.72) * mm});
            skLineSegment(sketch, "E313", {"start": v(-13.07, 6.72) * mm, "end": v(-13.08, 6.7) * mm});
            skLineSegment(sketch, "E314", {"start": v(-13.08, 6.7) * mm, "end": v(-13, 6.6) * mm});
            skLineSegment(sketch, "E315", {"start": v(-13, 6.6) * mm, "end": v(-12.98, 6.57) * mm});
            skLineSegment(sketch, "E316", {"start": v(-12.98, 6.57) * mm, "end": v(-12.95, 6.51) * mm});
            skLineSegment(sketch, "E317", {"start": v(-12.95, 6.51) * mm, "end": v(-12.98, 6.47) * mm});
            skLineSegment(sketch, "E318", {"start": v(-12.98, 6.47) * mm, "end": v(-13.09, 6.46) * mm});
            skLineSegment(sketch, "E319", {"start": v(-13.09, 6.46) * mm, "end": v(-13.11, 6.45) * mm});
            skLineSegment(sketch, "E320", {"start": v(-13.11, 6.45) * mm, "end": v(-13.11, 6.4) * mm});
            skLineSegment(sketch, "E321", {"start": v(-13.11, 6.4) * mm, "end": v(-13.08, 6.37) * mm});
            skLineSegment(sketch, "E322", {"start": v(-13.08, 6.37) * mm, "end": v(-13.06, 6.38) * mm});
            skLineSegment(sketch, "E323", {"start": v(-13.06, 6.38) * mm, "end": v(-13.05, 6.4) * mm});
            skLineSegment(sketch, "E324", {"start": v(-13.05, 6.4) * mm, "end": v(-13.02, 6.4) * mm});
            skLineSegment(sketch, "E325", {"start": v(-13.02, 6.4) * mm, "end": v(-13, 6.35) * mm});
            skLineSegment(sketch, "E326", {"start": v(-13, 6.35) * mm, "end": v(-13, 6.31) * mm});
            skLineSegment(sketch, "E327", {"start": v(-13, 6.31) * mm, "end": v(-13.04, 6.29) * mm});
            skLineSegment(sketch, "E328", {"start": v(-13.04, 6.29) * mm, "end": v(-13.07, 6.26) * mm});
            skLineSegment(sketch, "E329", {"start": v(-13.07, 6.26) * mm, "end": v(-13.07, 6.22) * mm});
            skLineSegment(sketch, "E330", {"start": v(-13.07, 6.22) * mm, "end": v(-13.03, 6.18) * mm});
            skLineSegment(sketch, "E331", {"start": v(-13.03, 6.18) * mm, "end": v(-13, 6.18) * mm});
            skLineSegment(sketch, "E332", {"start": v(-13, 6.18) * mm, "end": v(-12.97, 6.2) * mm});
            skLineSegment(sketch, "E333", {"start": v(-12.97, 6.2) * mm, "end": v(-12.93, 6.2) * mm});
            skLineSegment(sketch, "E334", {"start": v(-12.93, 6.2) * mm, "end": v(-12.93, 6.17) * mm});
            skLineSegment(sketch, "E335", {"start": v(-12.93, 6.17) * mm, "end": v(-12.94, 6.13) * mm});
            skLineSegment(sketch, "E336", {"start": v(-12.94, 6.13) * mm, "end": v(-12.91, 6.07) * mm});
            skLineSegment(sketch, "E337", {"start": v(-12.91, 6.07) * mm, "end": v(-12.82, 5.94) * mm});
            skLineSegment(sketch, "E338", {"start": v(-12.82, 5.94) * mm, "end": v(-12.77, 5.9) * mm});
            skLineSegment(sketch, "E339", {"start": v(-12.77, 5.9) * mm, "end": v(-12.74, 5.92) * mm});
            skLineSegment(sketch, "E340", {"start": v(-12.74, 5.92) * mm, "end": v(-12.75, 6.01) * mm});
            skLineSegment(sketch, "E341", {"start": v(-12.75, 6.01) * mm, "end": v(-12.73, 6.06) * mm});
            skLineSegment(sketch, "E342", {"start": v(-12.73, 6.06) * mm, "end": v(-12.68, 6.06) * mm});
            skLineSegment(sketch, "E343", {"start": v(-12.68, 6.06) * mm, "end": v(-12.21, 5.68) * mm});
            skLineSegment(sketch, "E344", {"start": v(-12.21, 5.68) * mm, "end": v(-12.18, 5.6) * mm});
            skLineSegment(sketch, "E345", {"start": v(-12.18, 5.6) * mm, "end": v(-12.15, 5.53) * mm});
            skLineSegment(sketch, "E346", {"start": v(-12.15, 5.53) * mm, "end": v(-12.12, 5.55) * mm});
            skLineSegment(sketch, "E347", {"start": v(-12.12, 5.55) * mm, "end": v(-12.12, 5.63) * mm});
            skLineSegment(sketch, "E348", {"start": v(-12.12, 5.63) * mm, "end": v(-12.1, 5.67) * mm});
            skLineSegment(sketch, "E349", {"start": v(-12.1, 5.67) * mm, "end": v(-12.06, 5.67) * mm});
            skLineSegment(sketch, "E350", {"start": v(-12.06, 5.67) * mm, "end": v(-11.92, 5.56) * mm});
            skLineSegment(sketch, "E351", {"start": v(-11.92, 5.56) * mm, "end": v(-11.75, 5.51) * mm});
            skLineSegment(sketch, "E352", {"start": v(-11.75, 5.51) * mm, "end": v(-11.63, 5.4) * mm});
            skLineSegment(sketch, "E353", {"start": v(-12.89, 6.2) * mm, "end": v(-12.87, 6.2) * mm});
            skLineSegment(sketch, "E354", {"start": v(-12.87, 6.2) * mm, "end": v(-12.84, 6.2) * mm});
            skLineSegment(sketch, "E355", {"start": v(-12.84, 6.2) * mm, "end": v(-12.81, 6.18) * mm});
            skLineSegment(sketch, "E356", {"start": v(-12.81, 6.18) * mm, "end": v(-12.81, 6.1) * mm});
            skLineSegment(sketch, "E357", {"start": v(-12.81, 6.1) * mm, "end": v(-12.83, 6.07) * mm});
            skLineSegment(sketch, "E358", {"start": v(-12.83, 6.07) * mm, "end": v(-12.85, 6.07) * mm});
            skLineSegment(sketch, "E359", {"start": v(-12.85, 6.07) * mm, "end": v(-12.88, 6.1) * mm});
            skLineSegment(sketch, "E360", {"start": v(-12.88, 6.1) * mm, "end": v(-12.9, 6.13) * mm});
            skLineSegment(sketch, "E361", {"start": v(-12.9, 6.13) * mm, "end": v(-12.89, 6.2) * mm});
            skLineSegment(sketch, "E362", {"start": v(-11.63, 5.4) * mm, "end": v(-11.5, 5.23) * mm});
            skLineSegment(sketch, "E363", {"start": v(-11.5, 5.23) * mm, "end": v(-11.45, 5.18) * mm});
            skLineSegment(sketch, "E364", {"start": v(-11.45, 5.18) * mm, "end": v(-11.43, 5.18) * mm});
            skLineSegment(sketch, "E365", {"start": v(-11.43, 5.18) * mm, "end": v(-11.42, 5.23) * mm});
            skLineSegment(sketch, "E366", {"start": v(-11.42, 5.23) * mm, "end": v(-11.46, 5.28) * mm});
            skLineSegment(sketch, "E367", {"start": v(-11.46, 5.28) * mm, "end": v(-11.46, 5.34) * mm});
            skLineSegment(sketch, "E368", {"start": v(-11.46, 5.34) * mm, "end": v(-11.46, 5.38) * mm});
            skLineSegment(sketch, "E369", {"start": v(-11.46, 5.38) * mm, "end": v(-11.52, 5.45) * mm});
            skLineSegment(sketch, "E370", {"start": v(-11.52, 5.45) * mm, "end": v(-11.57, 5.52) * mm});
            skLineSegment(sketch, "E371", {"start": v(-11.57, 5.52) * mm, "end": v(-11.58, 5.59) * mm});
            skLineSegment(sketch, "E372", {"start": v(-11.58, 5.59) * mm, "end": v(-11.55, 5.62) * mm});
            skLineSegment(sketch, "E373", {"start": v(-11.55, 5.62) * mm, "end": v(-11.52, 5.6) * mm});
            skLineSegment(sketch, "E374", {"start": v(-11.52, 5.6) * mm, "end": v(-11.48, 5.53) * mm});
            skLineSegment(sketch, "E375", {"start": v(-11.48, 5.53) * mm, "end": v(-11.44, 5.48) * mm});
            skLineSegment(sketch, "E376", {"start": v(-11.44, 5.48) * mm, "end": v(-11.42, 5.42) * mm});
            skLineSegment(sketch, "E377", {"start": v(-11.42, 5.42) * mm, "end": v(-11.4, 5.33) * mm});
            skLineSegment(sketch, "E378", {"start": v(-11.4, 5.33) * mm, "end": v(-11.38, 5.29) * mm});
            skLineSegment(sketch, "E379", {"start": v(-11.38, 5.29) * mm, "end": v(-11.35, 5.22) * mm});
            skLineSegment(sketch, "E380", {"start": v(-11.35, 5.22) * mm, "end": v(-11.34, 5.18) * mm});
            skLineSegment(sketch, "E381", {"start": v(-11.34, 5.18) * mm, "end": v(-11.3, 5.18) * mm});
            skLineSegment(sketch, "E382", {"start": v(-11.3, 5.18) * mm, "end": v(-11.3, 5.2) * mm});
            skLineSegment(sketch, "E383", {"start": v(-11.3, 5.2) * mm, "end": v(-11.17, 5.2) * mm});
            skLineSegment(sketch, "E384", {"start": v(-11.17, 5.2) * mm, "end": v(-11.13, 5.25) * mm});
            skLineSegment(sketch, "E385", {"start": v(-11.13, 5.25) * mm, "end": v(-11.07, 5.32) * mm});
            skLineSegment(sketch, "E386", {"start": v(-11.07, 5.32) * mm, "end": v(-11, 5.35) * mm});
            skLineSegment(sketch, "E387", {"start": v(-11, 5.35) * mm, "end": v(-11, 5.42) * mm});
            skLineSegment(sketch, "E388", {"start": v(-11, 5.42) * mm, "end": v(-10.95, 5.43) * mm});
            skLineSegment(sketch, "E389", {"start": v(-10.95, 5.43) * mm, "end": v(-10.9, 5.34) * mm});
            skLineSegment(sketch, "E390", {"start": v(-10.9, 5.34) * mm, "end": v(-10.86, 5.21) * mm});
            skLineSegment(sketch, "E391", {"start": v(-10.86, 5.21) * mm, "end": v(-10.81, 5.1) * mm});
            skLineSegment(sketch, "E392", {"start": v(-10.81, 5.1) * mm, "end": v(-10.78, 5.07) * mm});
            skLineSegment(sketch, "E393", {"start": v(-10.78, 5.07) * mm, "end": v(-10.75, 5.08) * mm});
            skLineSegment(sketch, "E394", {"start": v(-10.75, 5.08) * mm, "end": v(-10.7, 5.12) * mm});
            skLineSegment(sketch, "E395", {"start": v(-10.7, 5.12) * mm, "end": v(-10.7, 5.16) * mm});
            skLineSegment(sketch, "E396", {"start": v(-10.7, 5.16) * mm, "end": v(-10.72, 5.21) * mm});
            skLineSegment(sketch, "E397", {"start": v(-10.72, 5.21) * mm, "end": v(-10.74, 5.27) * mm});
            skLineSegment(sketch, "E398", {"start": v(-10.74, 5.27) * mm, "end": v(-10.77, 5.3) * mm});
            skLineSegment(sketch, "E399", {"start": v(-10.77, 5.3) * mm, "end": v(-10.76, 5.34) * mm});
            skLineSegment(sketch, "E400", {"start": v(-10.76, 5.34) * mm, "end": v(-10.72, 5.38) * mm});
            skLineSegment(sketch, "E401", {"start": v(-10.72, 5.38) * mm, "end": v(-10.66, 5.37) * mm});
            skLineSegment(sketch, "E402", {"start": v(-10.66, 5.37) * mm, "end": v(-10.64, 5.25) * mm});
            skLineSegment(sketch, "E403", {"start": v(-10.64, 5.25) * mm, "end": v(-10.58, 5.2) * mm});
            skLineSegment(sketch, "E404", {"start": v(-10.58, 5.2) * mm, "end": v(-10.5, 5.13) * mm});
            skLineSegment(sketch, "E405", {"start": v(-10.5, 5.13) * mm, "end": v(-10.4, 5) * mm});
            skLineSegment(sketch, "E406", {"start": v(-10.4, 5) * mm, "end": v(-10.32, 4.89) * mm});
            skLineSegment(sketch, "E407", {"start": v(-10.32, 4.89) * mm, "end": v(-10.31, 4.85) * mm});
            skLineSegment(sketch, "E408", {"start": v(-10.31, 4.85) * mm, "end": v(-10.27, 4.85) * mm});
            skLineSegment(sketch, "E409", {"start": v(-10.27, 4.85) * mm, "end": v(-10.26, 4.9) * mm});
            skLineSegment(sketch, "E410", {"start": v(-10.26, 4.9) * mm, "end": v(-10.29, 4.93) * mm});
            skLineSegment(sketch, "E411", {"start": v(-10.29, 4.93) * mm, "end": v(-10.29, 4.98) * mm});
            skLineSegment(sketch, "E412", {"start": v(-10.29, 4.98) * mm, "end": v(-10.27, 5) * mm});
            skLineSegment(sketch, "E413", {"start": v(-10.27, 5) * mm, "end": v(-10.22, 4.98) * mm});
            skLineSegment(sketch, "E414", {"start": v(-10.22, 4.98) * mm, "end": v(-10.18, 4.96) * mm});
            skLineSegment(sketch, "E415", {"start": v(-10.18, 4.96) * mm, "end": v(-10.16, 4.93) * mm});
            skLineSegment(sketch, "E416", {"start": v(-10.16, 4.93) * mm, "end": v(-10.15, 4.9) * mm});
            skLineSegment(sketch, "E417", {"start": v(-10.15, 4.9) * mm, "end": v(-10.07, 4.9) * mm});
            skLineSegment(sketch, "E418", {"start": v(-10.07, 4.9) * mm, "end": v(-10.05, 4.93) * mm});
            skLineSegment(sketch, "E419", {"start": v(-10.05, 4.93) * mm, "end": v(-10.03, 4.95) * mm});
            skLineSegment(sketch, "E420", {"start": v(-10.03, 4.95) * mm, "end": v(-10.03, 5.03) * mm});
            skLineSegment(sketch, "E421", {"start": v(-10.03, 5.03) * mm, "end": v(-10.06, 5.07) * mm});
            skLineSegment(sketch, "E422", {"start": v(-10.06, 5.07) * mm, "end": v(-10.06, 5.15) * mm});
            skLineSegment(sketch, "E423", {"start": v(-10.06, 5.15) * mm, "end": v(-10.02, 5.2) * mm});
            skLineSegment(sketch, "E424", {"start": v(-10.02, 5.2) * mm, "end": v(-9.95, 5.17) * mm});
            skLineSegment(sketch, "E425", {"start": v(-9.95, 5.17) * mm, "end": v(-9.94, 5.13) * mm});
            skLineSegment(sketch, "E426", {"start": v(-9.94, 5.13) * mm, "end": v(-9.97, 5.08) * mm});
            skLineSegment(sketch, "E427", {"start": v(-9.97, 5.08) * mm, "end": v(-9.92, 5) * mm});
            skLineSegment(sketch, "E428", {"start": v(-9.92, 5) * mm, "end": v(-9.88, 4.95) * mm});
            skLineSegment(sketch, "E429", {"start": v(-9.88, 4.95) * mm, "end": v(-9.84, 4.95) * mm});
            skLineSegment(sketch, "E430", {"start": v(-9.84, 4.95) * mm, "end": v(-9.82, 5.01) * mm});
            skLineSegment(sketch, "E431", {"start": v(-9.82, 5.01) * mm, "end": v(-9.79, 5.04) * mm});
            skLineSegment(sketch, "E432", {"start": v(-9.79, 5.04) * mm, "end": v(-9.73, 5.05) * mm});
            skLineSegment(sketch, "E433", {"start": v(-9.73, 5.05) * mm, "end": v(-9.7, 5.08) * mm});
            skLineSegment(sketch, "E434", {"start": v(-9.7, 5.08) * mm, "end": v(-9.65, 5.08) * mm});
            skLineSegment(sketch, "E435", {"start": v(-9.65, 5.08) * mm, "end": v(-9.62, 4.98) * mm});
            skLineSegment(sketch, "E436", {"start": v(-9.62, 4.98) * mm, "end": v(-9.58, 4.93) * mm});
            skLineSegment(sketch, "E437", {"start": v(-9.58, 4.93) * mm, "end": v(-9.53, 4.93) * mm});
            skLineSegment(sketch, "E438", {"start": v(-9.53, 4.93) * mm, "end": v(-9.51, 4.96) * mm});
            skLineSegment(sketch, "E439", {"start": v(-9.51, 4.96) * mm, "end": v(-9.51, 5.03) * mm});
            skLineSegment(sketch, "E440", {"start": v(-9.51, 5.03) * mm, "end": v(-9.56, 5.09) * mm});
            skLineSegment(sketch, "E441", {"start": v(-9.56, 5.09) * mm, "end": v(-9.55, 5.12) * mm});
            skLineSegment(sketch, "E442", {"start": v(-9.55, 5.12) * mm, "end": v(-9.5, 5.1) * mm});
            skLineSegment(sketch, "E443", {"start": v(-9.5, 5.1) * mm, "end": v(-9.41, 5.03) * mm});
            skLineSegment(sketch, "E444", {"start": v(-9.41, 5.03) * mm, "end": v(-9.4, 5.04) * mm});
            skLineSegment(sketch, "E445", {"start": v(-9.4, 5.04) * mm, "end": v(-9.4, 5.12) * mm});
            skLineSegment(sketch, "E446", {"start": v(-9.4, 5.12) * mm, "end": v(-9.38, 5.12) * mm});
            skLineSegment(sketch, "E447", {"start": v(-9.38, 5.12) * mm, "end": v(-9.29, 5.03) * mm});
            skLineSegment(sketch, "E448", {"start": v(-9.29, 5.03) * mm, "end": v(-9.27, 4.98) * mm});
            skLineSegment(sketch, "E449", {"start": v(-9.27, 4.98) * mm, "end": v(-9.15, 4.93) * mm});
            skLineSegment(sketch, "E450", {"start": v(-9.15, 4.93) * mm, "end": v(-9.06, 4.93) * mm});
            skLineSegment(sketch, "E451", {"start": v(-9.06, 4.93) * mm, "end": v(-9, 5.03) * mm});
            skLineSegment(sketch, "E452", {"start": v(-9, 5.03) * mm, "end": v(-8.99, 5.07) * mm});
            skLineSegment(sketch, "E453", {"start": v(-8.99, 5.07) * mm, "end": v(-8.99, 5.12) * mm});
            skLineSegment(sketch, "E454", {"start": v(-8.99, 5.12) * mm, "end": v(-9.02, 5.15) * mm});
            skLineSegment(sketch, "E455", {"start": v(-9.02, 5.15) * mm, "end": v(-9.02, 5.22) * mm});
            skLineSegment(sketch, "E456", {"start": v(-9.02, 5.22) * mm, "end": v(-9, 5.25) * mm});
            skLineSegment(sketch, "E457", {"start": v(-9, 5.25) * mm, "end": v(-8.97, 5.25) * mm});
            skLineSegment(sketch, "E458", {"start": v(-8.97, 5.25) * mm, "end": v(-8.93, 5.2) * mm});
            skLineSegment(sketch, "E459", {"start": v(-8.93, 5.2) * mm, "end": v(-8.9, 5.16) * mm});
            skLineSegment(sketch, "E460", {"start": v(-8.9, 5.16) * mm, "end": v(-8.69, 5.16) * mm});
            skLineSegment(sketch, "E461", {"start": v(-8.69, 5.16) * mm, "end": v(-8.64, 5.2) * mm});
            skLineSegment(sketch, "E462", {"start": v(-8.64, 5.2) * mm, "end": v(-8.6, 5.24) * mm});
            skLineSegment(sketch, "E463", {"start": v(-8.6, 5.24) * mm, "end": v(-8.52, 5.27) * mm});
            skLineSegment(sketch, "E464", {"start": v(-8.52, 5.27) * mm, "end": v(-8.47, 5.34) * mm});
            skLineSegment(sketch, "E465", {"start": v(-8.47, 5.34) * mm, "end": v(-8.4, 5.42) * mm});
            skLineSegment(sketch, "E466", {"start": v(-8.4, 5.42) * mm, "end": v(-8.35, 5.45) * mm});
            skLineSegment(sketch, "E467", {"start": v(-8.35, 5.45) * mm, "end": v(-8.28, 5.44) * mm});
            skLineSegment(sketch, "E468", {"start": v(-8.28, 5.44) * mm, "end": v(-8.23, 5.42) * mm});
            skLineSegment(sketch, "E469", {"start": v(-8.23, 5.42) * mm, "end": v(-8.14, 5.42) * mm});
            skLineSegment(sketch, "E470", {"start": v(-8.14, 5.42) * mm, "end": v(-8.06, 5.55) * mm});
            skLineSegment(sketch, "E471", {"start": v(-8.06, 5.55) * mm, "end": v(-7.91, 5.66) * mm});
            skLineSegment(sketch, "E472", {"start": v(-7.91, 5.66) * mm, "end": v(-7.81, 5.76) * mm});
            skLineSegment(sketch, "E473", {"start": v(-7.81, 5.76) * mm, "end": v(-7.76, 5.76) * mm});
            skLineSegment(sketch, "E474", {"start": v(-7.76, 5.76) * mm, "end": v(-7.74, 5.75) * mm});
            skLineSegment(sketch, "E475", {"start": v(-7.74, 5.75) * mm, "end": v(-7.81, 5.67) * mm});
            skLineSegment(sketch, "E476", {"start": v(-7.81, 5.67) * mm, "end": v(-7.8, 5.63) * mm});
            skLineSegment(sketch, "E477", {"start": v(-7.8, 5.63) * mm, "end": v(-7.73, 5.63) * mm});
            skLineSegment(sketch, "E478", {"start": v(-7.73, 5.63) * mm, "end": v(-7.58, 5.8) * mm});
            skLineSegment(sketch, "E479", {"start": v(-7.58, 5.8) * mm, "end": v(-7.47, 5.8) * mm});
            skLineSegment(sketch, "E480", {"start": v(-7.47, 5.8) * mm, "end": v(-7.43, 5.85) * mm});
            skLineSegment(sketch, "E481", {"start": v(-7.43, 5.85) * mm, "end": v(-7.43, 5.98) * mm});
            skLineSegment(sketch, "E482", {"start": v(-7.43, 5.98) * mm, "end": v(-7.45, 6.02) * mm});
            skLineSegment(sketch, "E483", {"start": v(-7.45, 6.02) * mm, "end": v(-7.44, 6.05) * mm});
            skLineSegment(sketch, "E484", {"start": v(-7.44, 6.05) * mm, "end": v(-7.41, 6.1) * mm});
            skLineSegment(sketch, "E485", {"start": v(-7.41, 6.1) * mm, "end": v(-7.37, 6.09) * mm});
            skLineSegment(sketch, "E486", {"start": v(-7.37, 6.09) * mm, "end": v(-7.36, 6.05) * mm});
            skLineSegment(sketch, "E487", {"start": v(-7.36, 6.05) * mm, "end": v(-7.38, 6) * mm});
            skLineSegment(sketch, "E488", {"start": v(-7.38, 6) * mm, "end": v(-7.38, 5.93) * mm});
            skLineSegment(sketch, "E489", {"start": v(-7.38, 5.93) * mm, "end": v(-7.37, 5.9) * mm});
            skLineSegment(sketch, "E490", {"start": v(-7.37, 5.9) * mm, "end": v(-7.32, 5.9) * mm});
            skLineSegment(sketch, "E491", {"start": v(-7.32, 5.9) * mm, "end": v(-7.3, 5.94) * mm});
            skLineSegment(sketch, "E492", {"start": v(-7.3, 5.94) * mm, "end": v(-7.27, 6.01) * mm});
            skLineSegment(sketch, "E493", {"start": v(-7.27, 6.01) * mm, "end": v(-7.25, 6.05) * mm});
            skLineSegment(sketch, "E494", {"start": v(-7.25, 6.05) * mm, "end": v(-7.2, 6.06) * mm});
            skLineSegment(sketch, "E495", {"start": v(-7.2, 6.06) * mm, "end": v(-7.2, 6) * mm});
            skLineSegment(sketch, "E496", {"start": v(-7.2, 6) * mm, "end": v(-7.17, 6) * mm});
            skLineSegment(sketch, "E497", {"start": v(-7.17, 6) * mm, "end": v(-7.1, 6.1) * mm});
            skLineSegment(sketch, "E498", {"start": v(-7.1, 6.1) * mm, "end": v(-7.07, 6.16) * mm});
            skLineSegment(sketch, "E499", {"start": v(-7.07, 6.16) * mm, "end": v(-7, 6.22) * mm});
            skLineSegment(sketch, "E500", {"start": v(-7, 6.22) * mm, "end": v(-6.97, 6.26) * mm});
            skLineSegment(sketch, "E501", {"start": v(-6.97, 6.26) * mm, "end": v(-6.94, 6.22) * mm});
            skLineSegment(sketch, "E502", {"start": v(-6.94, 6.22) * mm, "end": v(-6.86, 6.23) * mm});
            skLineSegment(sketch, "E503", {"start": v(-6.86, 6.23) * mm, "end": v(-6.83, 6.28) * mm});
            skLineSegment(sketch, "E504", {"start": v(-6.83, 6.28) * mm, "end": v(-6.82, 6.35) * mm});
            skLineSegment(sketch, "E505", {"start": v(-6.82, 6.35) * mm, "end": v(-6.8, 6.38) * mm});
            skLineSegment(sketch, "E506", {"start": v(-6.8, 6.38) * mm, "end": v(-6.77, 6.43) * mm});
            skLineSegment(sketch, "E507", {"start": v(-6.77, 6.43) * mm, "end": v(-6.72, 6.48) * mm});
            skLineSegment(sketch, "E508", {"start": v(-6.72, 6.48) * mm, "end": v(-6.62, 6.49) * mm});
            skLineSegment(sketch, "E509", {"start": v(-6.62, 6.49) * mm, "end": v(-6.56, 6.55) * mm});
            skLineSegment(sketch, "E510", {"start": v(-6.56, 6.55) * mm, "end": v(-6.53, 6.61) * mm});
            skLineSegment(sketch, "E511", {"start": v(-6.53, 6.61) * mm, "end": v(-6.5, 6.65) * mm});
            skLineSegment(sketch, "E512", {"start": v(-6.5, 6.65) * mm, "end": v(-6.42, 6.63) * mm});
            skLineSegment(sketch, "E513", {"start": v(-6.42, 6.63) * mm, "end": v(-6.36, 6.65) * mm});
            skLineSegment(sketch, "E514", {"start": v(-6.36, 6.65) * mm, "end": v(-6.32, 6.67) * mm});
            skLineSegment(sketch, "E515", {"start": v(-6.32, 6.67) * mm, "end": v(-6.33, 6.7) * mm});
            skLineSegment(sketch, "E516", {"start": v(-6.33, 6.7) * mm, "end": v(-6.42, 6.74) * mm});
            skLineSegment(sketch, "E517", {"start": v(-6.42, 6.74) * mm, "end": v(-6.35, 6.8) * mm});
            skLineSegment(sketch, "E518", {"start": v(-6.35, 6.8) * mm, "end": v(-6.32, 6.88) * mm});
            skLineSegment(sketch, "E519", {"start": v(-6.32, 6.88) * mm, "end": v(-6.25, 6.95) * mm});
            skLineSegment(sketch, "E520", {"start": v(-6.25, 6.95) * mm, "end": v(-6.22, 6.94) * mm});
            skLineSegment(sketch, "E521", {"start": v(-6.22, 6.94) * mm, "end": v(-6.21, 6.9) * mm});
            skLineSegment(sketch, "E522", {"start": v(-6.21, 6.9) * mm, "end": v(-6.24, 6.88) * mm});
            skLineSegment(sketch, "E523", {"start": v(-6.24, 6.88) * mm, "end": v(-6.25, 6.8) * mm});
            skLineSegment(sketch, "E524", {"start": v(-6.25, 6.8) * mm, "end": v(-6.18, 6.8) * mm});
            skLineSegment(sketch, "E525", {"start": v(-6.18, 6.8) * mm, "end": v(-6.16, 6.85) * mm});
            skLineSegment(sketch, "E526", {"start": v(-6.16, 6.85) * mm, "end": v(-6.05, 6.93) * mm});
            skLineSegment(sketch, "E527", {"start": v(-6.05, 6.93) * mm, "end": v(-5.91, 7.04) * mm});
            skLineSegment(sketch, "E528", {"start": v(-5.91, 7.04) * mm, "end": v(-5.89, 7.07) * mm});
            skLineSegment(sketch, "E529", {"start": v(-5.89, 7.07) * mm, "end": v(-5.89, 7.11) * mm});
            skLineSegment(sketch, "E530", {"start": v(-5.89, 7.11) * mm, "end": v(-5.95, 7.17) * mm});
            skLineSegment(sketch, "E531", {"start": v(-5.95, 7.17) * mm, "end": v(-5.94, 7.23) * mm});
            skLineSegment(sketch, "E532", {"start": v(-5.94, 7.23) * mm, "end": v(-5.91, 7.25) * mm});
            skLineSegment(sketch, "E533", {"start": v(-5.91, 7.25) * mm, "end": v(-5.86, 7.26) * mm});
            skLineSegment(sketch, "E534", {"start": v(-5.86, 7.26) * mm, "end": v(-5.85, 7.23) * mm});
            skLineSegment(sketch, "E535", {"start": v(-5.85, 7.23) * mm, "end": v(-5.78, 7.24) * mm});
            skLineSegment(sketch, "E536", {"start": v(-5.78, 7.24) * mm, "end": v(-5.75, 7.27) * mm});
            skLineSegment(sketch, "E537", {"start": v(-5.75, 7.27) * mm, "end": v(-5.7, 7.27) * mm});
            skLineSegment(sketch, "E538", {"start": v(-5.7, 7.27) * mm, "end": v(-5.52, 7.52) * mm});
            skLineSegment(sketch, "E539", {"start": v(-5.52, 7.52) * mm, "end": v(-5.41, 7.52) * mm});
            skLineSegment(sketch, "E540", {"start": v(-5.41, 7.52) * mm, "end": v(-5.21, 7.72) * mm});
            skLineSegment(sketch, "E541", {"start": v(-5.21, 7.72) * mm, "end": v(-5.15, 7.73) * mm});
            skLineSegment(sketch, "E542", {"start": v(-5.15, 7.73) * mm, "end": v(-5.15, 7.67) * mm});
            skLineSegment(sketch, "E543", {"start": v(-5.15, 7.67) * mm, "end": v(-5.1, 7.67) * mm});
            skLineSegment(sketch, "E544", {"start": v(-5.1, 7.67) * mm, "end": v(-5.09, 7.73) * mm});
            skLineSegment(sketch, "E545", {"start": v(-5.09, 7.73) * mm, "end": v(-5.05, 7.72) * mm});
            skLineSegment(sketch, "E546", {"start": v(-5.05, 7.72) * mm, "end": v(-5.04, 7.7) * mm});
            skLineSegment(sketch, "E547", {"start": v(-5.04, 7.7) * mm, "end": v(-5.02, 7.72) * mm});
            skLineSegment(sketch, "E548", {"start": v(-5.02, 7.72) * mm, "end": v(-5, 7.73) * mm});
            skLineSegment(sketch, "E549", {"start": v(-5, 7.73) * mm, "end": v(-4.99, 7.8) * mm});
            skLineSegment(sketch, "E550", {"start": v(-4.99, 7.8) * mm, "end": v(-5.02, 7.84) * mm});
            skLineSegment(sketch, "E551", {"start": v(-5.02, 7.84) * mm, "end": v(-4.98, 7.87) * mm});
            skLineSegment(sketch, "E552", {"start": v(-4.98, 7.87) * mm, "end": v(-4.92, 7.85) * mm});
            skLineSegment(sketch, "E553", {"start": v(-4.92, 7.85) * mm, "end": v(-4.87, 7.82) * mm});
            skLineSegment(sketch, "E554", {"start": v(-4.87, 7.82) * mm, "end": v(-4.8, 7.85) * mm});
            skLineSegment(sketch, "E555", {"start": v(-4.8, 7.85) * mm, "end": v(-4.71, 7.91) * mm});
            skLineSegment(sketch, "E556", {"start": v(-4.71, 7.91) * mm, "end": v(-4.7, 7.97) * mm});
            skLineSegment(sketch, "E557", {"start": v(-4.7, 7.97) * mm, "end": v(-4.63, 7.98) * mm});
            skLineSegment(sketch, "E558", {"start": v(-4.63, 7.98) * mm, "end": v(-4.58, 8.02) * mm});
            skLineSegment(sketch, "E559", {"start": v(-4.58, 8.02) * mm, "end": v(-4.54, 8.06) * mm});
            skLineSegment(sketch, "E560", {"start": v(-4.54, 8.06) * mm, "end": v(-4.4, 8.13) * mm});
            skLineSegment(sketch, "E561", {"start": v(-4.4, 8.13) * mm, "end": v(-4.35, 8.18) * mm});
            skLineSegment(sketch, "E562", {"start": v(-4.35, 8.18) * mm, "end": v(-4.36, 8.2) * mm});
            skLineSegment(sketch, "E563", {"start": v(-4.36, 8.2) * mm, "end": v(-4.4, 8.25) * mm});
            skLineSegment(sketch, "E564", {"start": v(-4.4, 8.25) * mm, "end": v(-4.42, 8.3) * mm});
            skLineSegment(sketch, "E565", {"start": v(-4.42, 8.3) * mm, "end": v(-4.36, 8.3) * mm});
            skLineSegment(sketch, "E566", {"start": v(-4.36, 8.3) * mm, "end": v(-4.3, 8.3) * mm});
            skLineSegment(sketch, "E567", {"start": v(-4.3, 8.3) * mm, "end": v(-4.28, 8.27) * mm});
            skLineSegment(sketch, "E568", {"start": v(-4.28, 8.27) * mm, "end": v(-4.24, 8.27) * mm});
            skLineSegment(sketch, "E569", {"start": v(-4.24, 8.27) * mm, "end": v(-4.2, 8.3) * mm});
            skLineSegment(sketch, "E570", {"start": v(-4.2, 8.3) * mm, "end": v(-4.17, 8.35) * mm});
            skLineSegment(sketch, "E571", {"start": v(-4.17, 8.35) * mm, "end": v(-4.1, 8.37) * mm});
            skLineSegment(sketch, "E572", {"start": v(-4.1, 8.37) * mm, "end": v(-3.9, 8.58) * mm});
            skLineSegment(sketch, "E573", {"start": v(-3.9, 8.58) * mm, "end": v(-3.73, 8.7) * mm});
            skLineSegment(sketch, "E574", {"start": v(-3.73, 8.7) * mm, "end": v(-3.73, 8.77) * mm});
            skLineSegment(sketch, "E575", {"start": v(-3.73, 8.77) * mm, "end": v(-3.76, 8.82) * mm});
            skLineSegment(sketch, "E576", {"start": v(-3.76, 8.82) * mm, "end": v(-3.75, 8.86) * mm});
            skLineSegment(sketch, "E577", {"start": v(-3.75, 8.86) * mm, "end": v(-3.72, 8.9) * mm});
            skLineSegment(sketch, "E578", {"start": v(-3.72, 8.9) * mm, "end": v(-3.69, 8.9) * mm});
            skLineSegment(sketch, "E579", {"start": v(-3.69, 8.9) * mm, "end": v(-3.66, 8.88) * mm});
            skLineSegment(sketch, "E580", {"start": v(-3.66, 8.88) * mm, "end": v(-3.65, 8.84) * mm});
            skLineSegment(sketch, "E581", {"start": v(-3.65, 8.84) * mm, "end": v(-3.68, 8.8) * mm});
            skLineSegment(sketch, "E582", {"start": v(-3.68, 8.8) * mm, "end": v(-3.67, 8.76) * mm});
            skLineSegment(sketch, "E583", {"start": v(-3.67, 8.76) * mm, "end": v(-3.6, 8.77) * mm});
            skLineSegment(sketch, "E584", {"start": v(-3.6, 8.77) * mm, "end": v(-3.53, 8.81) * mm});
            skLineSegment(sketch, "E585", {"start": v(-3.53, 8.81) * mm, "end": v(-3.45, 8.9) * mm});
            skLineSegment(sketch, "E586", {"start": v(-3.45, 8.9) * mm, "end": v(-3.32, 8.94) * mm});
            skLineSegment(sketch, "E587", {"start": v(-3.32, 8.94) * mm, "end": v(-2.76, 9.26) * mm});
            skLineSegment(sketch, "E588", {"start": v(-2.76, 9.26) * mm, "end": v(-2.58, 9.36) * mm});
            skLineSegment(sketch, "E589", {"start": v(-2.58, 9.36) * mm, "end": v(-2.52, 9.49) * mm});
            skLineSegment(sketch, "E590", {"start": v(-2.52, 9.49) * mm, "end": v(-2.45, 9.55) * mm});
            skLineSegment(sketch, "E591", {"start": v(-2.45, 9.55) * mm, "end": v(-2.33, 9.6) * mm});
            skLineSegment(sketch, "E592", {"start": v(-2.33, 9.6) * mm, "end": v(-2.24, 9.62) * mm});
            skLineSegment(sketch, "E593", {"start": v(-2.24, 9.62) * mm, "end": v(-1.56, 10.05) * mm});
            skLineSegment(sketch, "E594", {"start": v(-1.56, 10.05) * mm, "end": v(-1.26, 10.27) * mm});
            skLineSegment(sketch, "E595", {"start": v(-1.26, 10.27) * mm, "end": v(-1, 10.42) * mm});
            skLineSegment(sketch, "E596", {"start": v(-1, 10.42) * mm, "end": v(-0.74, 10.64) * mm});
            skLineSegment(sketch, "E597", {"start": v(-0.74, 10.64) * mm, "end": v(-0.6, 10.78) * mm});
            skLineSegment(sketch, "E598", {"start": v(-0.6, 10.78) * mm, "end": v(-0.6, 10.84) * mm});
            skLineSegment(sketch, "E599", {"start": v(-0.6, 10.84) * mm, "end": v(-0.99, 11.38) * mm});
            skLineSegment(sketch, "E600", {"start": v(-0.99, 11.38) * mm, "end": v(-1.03, 11.55) * mm});
            skLineSegment(sketch, "E601", {"start": v(-1.03, 11.55) * mm, "end": v(-1.38, 11.95) * mm});
            skLineSegment(sketch, "E602", {"start": v(-1.38, 11.95) * mm, "end": v(-1.63, 12.41) * mm});
            skLineSegment(sketch, "E603", {"start": v(-1.63, 12.41) * mm, "end": v(-1.7, 12.62) * mm});
            skLineSegment(sketch, "E604", {"start": v(-1.7, 12.62) * mm, "end": v(-1.8, 12.72) * mm});
            skLineSegment(sketch, "E605", {"start": v(-1.8, 12.72) * mm, "end": v(-1.88, 12.89) * mm});
            skLineSegment(sketch, "E606", {"start": v(-1.88, 12.89) * mm, "end": v(-1.8, 12.87) * mm});
            skLineSegment(sketch, "E607", {"start": v(-1.8, 12.87) * mm, "end": v(-1.8, 12.92) * mm});
            skLineSegment(sketch, "E608", {"start": v(-1.8, 12.92) * mm, "end": v(-1.88, 13.03) * mm});
            skLineSegment(sketch, "E609", {"start": v(-1.88, 13.03) * mm, "end": v(-1.87, 13.13) * mm});
            skLineSegment(sketch, "E610", {"start": v(-1.87, 13.13) * mm, "end": v(-1.78, 13.16) * mm});
            skLineSegment(sketch, "E611", {"start": v(-1.78, 13.16) * mm, "end": v(-1.7, 13.25) * mm});
            skLineSegment(sketch, "E612", {"start": v(-1.7, 13.25) * mm, "end": v(-1.57, 13.16) * mm});
            skLineSegment(sketch, "E613", {"start": v(-1.57, 13.16) * mm, "end": v(-1.56, 13.08) * mm});
            skLineSegment(sketch, "E614", {"start": v(-1.56, 13.08) * mm, "end": v(-1.48, 13) * mm});
            skLineSegment(sketch, "E615", {"start": v(-1.48, 13) * mm, "end": v(-1.38, 13) * mm});
            skLineSegment(sketch, "E616", {"start": v(-1.38, 13) * mm, "end": v(-1.11, 12.6) * mm});
            skLineSegment(sketch, "E617", {"start": v(-1.11, 12.6) * mm, "end": v(-0.46, 12) * mm});
            skLineSegment(sketch, "E618", {"start": v(-0.46, 12) * mm, "end": v(-0.36, 11.8) * mm});
            skLineSegment(sketch, "E619", {"start": v(-0.36, 11.8) * mm, "end": v(-0.27, 11.74) * mm});
            skLineSegment(sketch, "E620", {"start": v(-0.27, 11.74) * mm, "end": v(0.05, 11.32) * mm});
            skLineSegment(sketch, "E621", {"start": v(0.05, 11.32) * mm, "end": v(0.14, 11.3) * mm});
            skLineSegment(sketch, "E622", {"start": v(0.14, 11.3) * mm, "end": v(0.14, 11.38) * mm});
            skLineSegment(sketch, "E623", {"start": v(0.14, 11.38) * mm, "end": v(0.58, 11.84) * mm});
            skLineSegment(sketch, "E624", {"start": v(0.58, 11.84) * mm, "end": v(0.59, 11.93) * mm});
            skLineSegment(sketch, "E625", {"start": v(0.59, 11.93) * mm, "end": v(0.7, 12) * mm});
            skLineSegment(sketch, "E626", {"start": v(0.7, 12) * mm, "end": v(0.84, 12.1) * mm});
            skLineSegment(sketch, "E627", {"start": v(0.84, 12.1) * mm, "end": v(0.88, 12.1) * mm});
            skLineSegment(sketch, "E628", {"start": v(0.88, 12.1) * mm, "end": v(0.86, 12.05) * mm});
            skLineSegment(sketch, "E629", {"start": v(0.86, 12.05) * mm, "end": v(0.9, 12.02) * mm});
            skLineSegment(sketch, "E630", {"start": v(0.9, 12.02) * mm, "end": v(0.9, 11.95) * mm});
            skLineSegment(sketch, "E631", {"start": v(0.9, 11.95) * mm, "end": v(0.95, 11.92) * mm});
            skLineSegment(sketch, "E632", {"start": v(0.95, 11.92) * mm, "end": v(0.9, 11.78) * mm});
            skLineSegment(sketch, "E633", {"start": v(0.9, 11.78) * mm, "end": v(0.9, 11.7) * mm});
            skLineSegment(sketch, "E634", {"start": v(0.9, 11.7) * mm, "end": v(0.72, 11.55) * mm});
            skLineSegment(sketch, "E635", {"start": v(0.72, 11.55) * mm, "end": v(0.77, 11.5) * mm});
            skLineSegment(sketch, "E636", {"start": v(0.77, 11.5) * mm, "end": v(0.72, 11.34) * mm});
            skLineSegment(sketch, "E637", {"start": v(0.72, 11.34) * mm, "end": v(0.62, 11.24) * mm});
            skLineSegment(sketch, "E638", {"start": v(0.62, 11.24) * mm, "end": v(0.6, 11.11) * mm});
            skLineSegment(sketch, "E639", {"start": v(0.6, 11.11) * mm, "end": v(0.47, 11) * mm});
            skLineSegment(sketch, "E640", {"start": v(0.47, 11) * mm, "end": v(0.5, 10.93) * mm});
            skLineSegment(sketch, "E641", {"start": v(0.5, 10.93) * mm, "end": v(0.64, 10.9) * mm});
            skLineSegment(sketch, "E642", {"start": v(0.64, 10.9) * mm, "end": v(0.79, 10.66) * mm});
            skLineSegment(sketch, "E643", {"start": v(0.79, 10.66) * mm, "end": v(0.92, 10.57) * mm});
            skLineSegment(sketch, "E644", {"start": v(0.92, 10.57) * mm, "end": v(1.05, 10.45) * mm});
            skLineSegment(sketch, "E645", {"start": v(1.05, 10.45) * mm, "end": v(1.3, 10.26) * mm});
            skLineSegment(sketch, "E646", {"start": v(1.3, 10.26) * mm, "end": v(1.56, 10.02) * mm});
            skLineSegment(sketch, "E647", {"start": v(1.56, 10.02) * mm, "end": v(1.98, 9.93) * mm});
            skLineSegment(sketch, "E648", {"start": v(1.98, 9.93) * mm, "end": v(2.03, 9.82) * mm});
            skLineSegment(sketch, "E649", {"start": v(-0.97, 12.79) * mm, "end": v(-1.02, 12.83) * mm});
            skLineSegment(sketch, "E650", {"start": v(-1.02, 12.83) * mm, "end": v(-1.02, 12.92) * mm});
            skLineSegment(sketch, "E651", {"start": v(-1.02, 12.92) * mm, "end": v(-1, 12.95) * mm});
            skLineSegment(sketch, "E652", {"start": v(-1, 12.95) * mm, "end": v(-0.96, 12.95) * mm});
            skLineSegment(sketch, "E653", {"start": v(-0.96, 12.95) * mm, "end": v(-0.94, 12.92) * mm});
            skLineSegment(sketch, "E654", {"start": v(-0.94, 12.92) * mm, "end": v(-0.94, 12.88) * mm});
            skLineSegment(sketch, "E655", {"start": v(-0.94, 12.88) * mm, "end": v(-0.92, 12.84) * mm});
            skLineSegment(sketch, "E656", {"start": v(-0.92, 12.84) * mm, "end": v(-0.91, 12.8) * mm});
            skLineSegment(sketch, "E657", {"start": v(-0.97, 12.79) * mm, "end": v(-0.91, 12.8) * mm});
            skLineSegment(sketch, "E658", {"start": v(0.87, 10.68) * mm, "end": v(0.84, 10.71) * mm});
            skLineSegment(sketch, "E659", {"start": v(0.84, 10.71) * mm, "end": v(0.84, 10.76) * mm});
            skLineSegment(sketch, "E660", {"start": v(0.84, 10.76) * mm, "end": v(0.9, 10.76) * mm});
            skLineSegment(sketch, "E661", {"start": v(0.9, 10.76) * mm, "end": v(0.94, 10.71) * mm});
            skLineSegment(sketch, "E662", {"start": v(0.94, 10.71) * mm, "end": v(0.93, 10.68) * mm});
            skLineSegment(sketch, "E663", {"start": v(0.93, 10.68) * mm, "end": v(0.9, 10.67) * mm});
            skLineSegment(sketch, "E664", {"start": v(0.87, 10.68) * mm, "end": v(0.9, 10.67) * mm});
            skLineSegment(sketch, "E665", {"start": v(2.03, 9.82) * mm, "end": v(2.13, 9.8) * mm});
            skLineSegment(sketch, "E666", {"start": v(2.13, 9.8) * mm, "end": v(2.2, 9.72) * mm});
            skLineSegment(sketch, "E667", {"start": v(2.2, 9.72) * mm, "end": v(2.3, 9.7) * mm});
            skLineSegment(sketch, "E668", {"start": v(2.3, 9.7) * mm, "end": v(2.42, 9.59) * mm});
            skLineSegment(sketch, "E669", {"start": v(2.42, 9.59) * mm, "end": v(2.5, 9.62) * mm});
            skLineSegment(sketch, "E670", {"start": v(2.5, 9.62) * mm, "end": v(2.6, 9.59) * mm});
            skLineSegment(sketch, "E671", {"start": v(2.6, 9.59) * mm, "end": v(2.72, 9.44) * mm});
            skLineSegment(sketch, "E672", {"start": v(2.72, 9.44) * mm, "end": v(2.78, 9.43) * mm});
            skLineSegment(sketch, "E673", {"start": v(2.78, 9.43) * mm, "end": v(2.8, 9.52) * mm});
            skLineSegment(sketch, "E674", {"start": v(2.8, 9.52) * mm, "end": v(2.63, 9.66) * mm});
            skLineSegment(sketch, "E675", {"start": v(2.63, 9.66) * mm, "end": v(2.62, 9.73) * mm});
            skLineSegment(sketch, "E676", {"start": v(2.62, 9.73) * mm, "end": v(2.67, 9.75) * mm});
            skLineSegment(sketch, "E677", {"start": v(2.67, 9.75) * mm, "end": v(2.81, 9.58) * mm});
            skLineSegment(sketch, "E678", {"start": v(2.81, 9.58) * mm, "end": v(2.85, 9.58) * mm});
            skLineSegment(sketch, "E679", {"start": v(2.85, 9.58) * mm, "end": v(2.84, 9.63) * mm});
            skLineSegment(sketch, "E680", {"start": v(2.84, 9.63) * mm, "end": v(2.81, 9.64) * mm});
            skLineSegment(sketch, "E681", {"start": v(2.81, 9.64) * mm, "end": v(2.81, 9.66) * mm});
            skLineSegment(sketch, "E682", {"start": v(2.81, 9.66) * mm, "end": v(2.9, 9.66) * mm});
            skLineSegment(sketch, "E683", {"start": v(2.9, 9.66) * mm, "end": v(2.96, 9.63) * mm});
            skLineSegment(sketch, "E684", {"start": v(2.96, 9.63) * mm, "end": v(3.28, 9.44) * mm});
            skLineSegment(sketch, "E685", {"start": v(3.28, 9.44) * mm, "end": v(3.38, 9.42) * mm});
            skLineSegment(sketch, "E686", {"start": v(3.38, 9.42) * mm, "end": v(3.49, 9.36) * mm});
            skLineSegment(sketch, "E687", {"start": v(3.49, 9.36) * mm, "end": v(3.61, 9.36) * mm});
            skLineSegment(sketch, "E688", {"start": v(3.61, 9.36) * mm, "end": v(3.73, 9.28) * mm});
            skLineSegment(sketch, "E689", {"start": v(3.73, 9.28) * mm, "end": v(3.78, 9.28) * mm});
            skLineSegment(sketch, "E690", {"start": v(3.78, 9.28) * mm, "end": v(3.78, 9.36) * mm});
            skLineSegment(sketch, "E691", {"start": v(3.78, 9.36) * mm, "end": v(3.84, 9.35) * mm});
            skLineSegment(sketch, "E692", {"start": v(3.84, 9.35) * mm, "end": v(4.11, 9.2) * mm});
            skLineSegment(sketch, "E693", {"start": v(4.11, 9.2) * mm, "end": v(4.18, 9.2) * mm});
            skLineSegment(sketch, "E694", {"start": v(4.18, 9.2) * mm, "end": v(4.19, 9.23) * mm});
            skLineSegment(sketch, "E695", {"start": v(4.19, 9.23) * mm, "end": v(4.23, 9.22) * mm});
            skLineSegment(sketch, "E696", {"start": v(4.23, 9.22) * mm, "end": v(4.28, 9.16) * mm});
            skLineSegment(sketch, "E697", {"start": v(4.28, 9.16) * mm, "end": v(4.33, 9.2) * mm});
            skLineSegment(sketch, "E698", {"start": v(4.33, 9.2) * mm, "end": v(4.38, 9.2) * mm});
            skLineSegment(sketch, "E699", {"start": v(2.76, 9.8) * mm, "end": v(2.76, 9.74) * mm});
            skLineSegment(sketch, "E700", {"start": v(2.76, 9.74) * mm, "end": v(2.79, 9.72) * mm});
            skLineSegment(sketch, "E701", {"start": v(2.79, 9.72) * mm, "end": v(2.83, 9.73) * mm});
            skLineSegment(sketch, "E702", {"start": v(2.83, 9.73) * mm, "end": v(2.85, 9.74) * mm});
            skLineSegment(sketch, "E703", {"start": v(2.85, 9.74) * mm, "end": v(2.82, 9.77) * mm});
            skLineSegment(sketch, "E704", {"start": v(2.82, 9.77) * mm, "end": v(2.8, 9.8) * mm});
            skLineSegment(sketch, "E705", {"start": v(2.8, 9.8) * mm, "end": v(2.79, 9.8) * mm});
            skLineSegment(sketch, "E706", {"start": v(2.76, 9.8) * mm, "end": v(2.79, 9.8) * mm});
            skLineSegment(sketch, "E707", {"start": v(4.38, 9.2) * mm, "end": v(4.43, 9.13) * mm});
            skLineSegment(sketch, "E708", {"start": v(4.43, 9.13) * mm, "end": v(4.47, 9.11) * mm});
            skLineSegment(sketch, "E709", {"start": v(4.47, 9.11) * mm, "end": v(4.53, 9.1) * mm});
            skLineSegment(sketch, "E710", {"start": v(4.53, 9.1) * mm, "end": v(4.59, 9.07) * mm});
            skLineSegment(sketch, "E711", {"start": v(4.59, 9.07) * mm, "end": v(4.64, 9.06) * mm});
            skLineSegment(sketch, "E712", {"start": v(4.64, 9.06) * mm, "end": v(4.64, 9.12) * mm});
            skLineSegment(sketch, "E713", {"start": v(4.64, 9.12) * mm, "end": v(4.6, 9.15) * mm});
            skLineSegment(sketch, "E714", {"start": v(4.6, 9.15) * mm, "end": v(4.59, 9.19) * mm});
            skLineSegment(sketch, "E715", {"start": v(4.59, 9.19) * mm, "end": v(4.62, 9.2) * mm});
            skLineSegment(sketch, "E716", {"start": v(4.62, 9.2) * mm, "end": v(4.7, 9.2) * mm});
            skLineSegment(sketch, "E717", {"start": v(4.7, 9.2) * mm, "end": v(4.7, 9.21) * mm});
            skLineSegment(sketch, "E718", {"start": v(4.7, 9.21) * mm, "end": v(4.7, 9.24) * mm});
            skLineSegment(sketch, "E719", {"start": v(4.7, 9.24) * mm, "end": v(4.65, 9.29) * mm});
            skLineSegment(sketch, "E720", {"start": v(4.65, 9.29) * mm, "end": v(4.63, 9.3) * mm});
            skLineSegment(sketch, "E721", {"start": v(4.63, 9.3) * mm, "end": v(4.63, 9.32) * mm});
            skLineSegment(sketch, "E722", {"start": v(4.63, 9.32) * mm, "end": v(4.66, 9.34) * mm});
            skLineSegment(sketch, "E723", {"start": v(4.66, 9.34) * mm, "end": v(4.7, 9.33) * mm});
            skLineSegment(sketch, "E724", {"start": v(4.7, 9.33) * mm, "end": v(4.73, 9.28) * mm});
            skLineSegment(sketch, "E725", {"start": v(4.73, 9.28) * mm, "end": v(4.77, 9.22) * mm});
            skLineSegment(sketch, "E726", {"start": v(4.77, 9.22) * mm, "end": v(4.8, 9.17) * mm});
            skLineSegment(sketch, "E727", {"start": v(4.8, 9.17) * mm, "end": v(4.83, 9.16) * mm});
            skLineSegment(sketch, "E728", {"start": v(4.83, 9.16) * mm, "end": v(4.91, 9.14) * mm});
            skLineSegment(sketch, "E729", {"start": v(4.91, 9.14) * mm, "end": v(4.99, 9.11) * mm});
            skLineSegment(sketch, "E730", {"start": v(4.99, 9.11) * mm, "end": v(5.04, 9.1) * mm});
            skLineSegment(sketch, "E731", {"start": v(5.04, 9.1) * mm, "end": v(5.1, 9.14) * mm});
            skLineSegment(sketch, "E732", {"start": v(5.1, 9.14) * mm, "end": v(5.13, 9.16) * mm});
            skLineSegment(sketch, "E733", {"start": v(5.13, 9.16) * mm, "end": v(5.2, 9.16) * mm});
            skLineSegment(sketch, "E734", {"start": v(5.2, 9.16) * mm, "end": v(5.24, 9.14) * mm});
            skLineSegment(sketch, "E735", {"start": v(5.24, 9.14) * mm, "end": v(5.26, 9.1) * mm});
            skLineSegment(sketch, "E736", {"start": v(5.26, 9.1) * mm, "end": v(5.29, 9.07) * mm});
            skLineSegment(sketch, "E737", {"start": v(5.29, 9.07) * mm, "end": v(5.35, 9.08) * mm});
            skLineSegment(sketch, "E738", {"start": v(5.35, 9.08) * mm, "end": v(5.4, 9.1) * mm});
            skLineSegment(sketch, "E739", {"start": v(5.4, 9.1) * mm, "end": v(5.44, 9.15) * mm});
            skLineSegment(sketch, "E740", {"start": v(5.44, 9.15) * mm, "end": v(5.51, 9.17) * mm});
            skLineSegment(sketch, "E741", {"start": v(5.51, 9.17) * mm, "end": v(5.6, 9.16) * mm});
            skLineSegment(sketch, "E742", {"start": v(5.6, 9.16) * mm, "end": v(5.64, 9.2) * mm});
            skLineSegment(sketch, "E743", {"start": v(5.64, 9.2) * mm, "end": v(5.75, 9.18) * mm});
            skLineSegment(sketch, "E744", {"start": v(5.75, 9.18) * mm, "end": v(5.86, 9.1) * mm});
            skLineSegment(sketch, "E745", {"start": v(5.86, 9.1) * mm, "end": v(5.97, 9.1) * mm});
            skLineSegment(sketch, "E746", {"start": v(5.97, 9.1) * mm, "end": v(6.17, 8.89) * mm});
            skLineSegment(sketch, "E747", {"start": v(6.17, 8.89) * mm, "end": v(6.25, 8.8) * mm});
            skLineSegment(sketch, "E748", {"start": v(6.25, 8.8) * mm, "end": v(6.3, 8.8) * mm});
            skLineSegment(sketch, "E749", {"start": v(6.3, 8.8) * mm, "end": v(6.46, 8.6) * mm});
            skLineSegment(sketch, "E750", {"start": v(6.46, 8.6) * mm, "end": v(6.5, 8.57) * mm});
            skLineSegment(sketch, "E751", {"start": v(6.5, 8.57) * mm, "end": v(6.53, 8.57) * mm});
            skLineSegment(sketch, "E752", {"start": v(6.53, 8.57) * mm, "end": v(6.54, 8.62) * mm});
            skLineSegment(sketch, "E753", {"start": v(6.54, 8.62) * mm, "end": v(6.58, 8.62) * mm});
            skLineSegment(sketch, "E754", {"start": v(6.58, 8.62) * mm, "end": v(6.63, 8.57) * mm});
            skLineSegment(sketch, "E755", {"start": v(6.63, 8.57) * mm, "end": v(6.65, 8.53) * mm});
            skLineSegment(sketch, "E756", {"start": v(6.65, 8.53) * mm, "end": v(6.67, 8.54) * mm});
            skLineSegment(sketch, "E757", {"start": v(6.67, 8.54) * mm, "end": v(6.7, 8.59) * mm});
            skLineSegment(sketch, "E758", {"start": v(6.7, 8.59) * mm, "end": v(6.74, 8.59) * mm});
            skLineSegment(sketch, "E759", {"start": v(6.74, 8.59) * mm, "end": v(6.75, 8.55) * mm});
            skLineSegment(sketch, "E760", {"start": v(6.75, 8.55) * mm, "end": v(6.78, 8.55) * mm});
            skLineSegment(sketch, "E761", {"start": v(6.78, 8.55) * mm, "end": v(6.8, 8.56) * mm});
            skLineSegment(sketch, "E762", {"start": v(6.8, 8.56) * mm, "end": v(6.8, 8.6) * mm});
            skLineSegment(sketch, "E763", {"start": v(6.8, 8.6) * mm, "end": v(6.82, 8.63) * mm});
            skLineSegment(sketch, "E764", {"start": v(6.82, 8.63) * mm, "end": v(6.87, 8.63) * mm});
            skLineSegment(sketch, "E765", {"start": v(6.87, 8.63) * mm, "end": v(6.94, 8.54) * mm});
            skLineSegment(sketch, "E766", {"start": v(6.94, 8.54) * mm, "end": v(7.04, 8.52) * mm});
            skLineSegment(sketch, "E767", {"start": v(7.04, 8.52) * mm, "end": v(7.2, 8.38) * mm});
            skLineSegment(sketch, "E768", {"start": v(7.2, 8.38) * mm, "end": v(7.3, 8.37) * mm});
            skLineSegment(sketch, "E769", {"start": v(7.3, 8.37) * mm, "end": v(7.37, 8.3) * mm});
            skLineSegment(sketch, "E770", {"start": v(7.37, 8.3) * mm, "end": v(7.44, 8.27) * mm});
            skLineSegment(sketch, "E771", {"start": v(7.44, 8.27) * mm, "end": v(7.5, 8.2) * mm});
            skLineSegment(sketch, "E772", {"start": v(7.5, 8.2) * mm, "end": v(7.55, 8.16) * mm});
            skLineSegment(sketch, "E773", {"start": v(7.55, 8.16) * mm, "end": v(7.62, 8.16) * mm});
            skLineSegment(sketch, "E774", {"start": v(7.62, 8.16) * mm, "end": v(7.64, 8.21) * mm});
            skLineSegment(sketch, "E775", {"start": v(7.64, 8.21) * mm, "end": v(7.63, 8.27) * mm});
            skLineSegment(sketch, "E776", {"start": v(7.63, 8.27) * mm, "end": v(7.6, 8.32) * mm});
            skLineSegment(sketch, "E777", {"start": v(7.6, 8.32) * mm, "end": v(7.6, 8.4) * mm});
            skLineSegment(sketch, "E778", {"start": v(7.6, 8.4) * mm, "end": v(7.65, 8.4) * mm});
            skLineSegment(sketch, "E779", {"start": v(7.65, 8.4) * mm, "end": v(7.71, 8.34) * mm});
            skLineSegment(sketch, "E780", {"start": v(7.71, 8.34) * mm, "end": v(7.74, 8.28) * mm});
            skLineSegment(sketch, "E781", {"start": v(7.74, 8.28) * mm, "end": v(7.72, 8.22) * mm});
            skLineSegment(sketch, "E782", {"start": v(7.72, 8.22) * mm, "end": v(7.69, 8.16) * mm});
            skLineSegment(sketch, "E783", {"start": v(7.69, 8.16) * mm, "end": v(7.67, 8.12) * mm});
            skLineSegment(sketch, "E784", {"start": v(7.67, 8.12) * mm, "end": v(7.7, 8.08) * mm});
            skLineSegment(sketch, "E785", {"start": v(7.7, 8.08) * mm, "end": v(7.74, 8.1) * mm});
            skLineSegment(sketch, "E786", {"start": v(7.74, 8.1) * mm, "end": v(7.76, 8.08) * mm});
            skLineSegment(sketch, "E787", {"start": v(7.76, 8.08) * mm, "end": v(7.78, 8.01) * mm});
            skLineSegment(sketch, "E788", {"start": v(7.78, 8.01) * mm, "end": v(7.75, 7.98) * mm});
            skLineSegment(sketch, "E789", {"start": v(7.75, 7.98) * mm, "end": v(7.77, 7.92) * mm});
            skLineSegment(sketch, "E790", {"start": v(7.77, 7.92) * mm, "end": v(7.79, 7.82) * mm});
            skLineSegment(sketch, "E791", {"start": v(7.79, 7.82) * mm, "end": v(7.8, 7.8) * mm});
            skLineSegment(sketch, "E792", {"start": v(7.8, 7.8) * mm, "end": v(7.83, 7.8) * mm});
            skLineSegment(sketch, "E793", {"start": v(7.83, 7.8) * mm, "end": v(7.85, 7.83) * mm});
            skLineSegment(sketch, "E794", {"start": v(7.85, 7.83) * mm, "end": v(7.89, 7.84) * mm});
            skLineSegment(sketch, "E795", {"start": v(7.89, 7.84) * mm, "end": v(7.93, 7.8) * mm});
            skLineSegment(sketch, "E796", {"start": v(7.93, 7.8) * mm, "end": v(7.97, 7.74) * mm});
            skLineSegment(sketch, "E797", {"start": v(7.97, 7.74) * mm, "end": v(8, 7.73) * mm});
            skLineSegment(sketch, "E798", {"start": v(8, 7.73) * mm, "end": v(8.03, 7.78) * mm});
            skLineSegment(sketch, "E799", {"start": v(8.03, 7.78) * mm, "end": v(8.03, 7.82) * mm});
            skLineSegment(sketch, "E800", {"start": v(8.03, 7.82) * mm, "end": v(8.07, 7.83) * mm});
            skLineSegment(sketch, "E801", {"start": v(8.07, 7.83) * mm, "end": v(8.08, 7.8) * mm});
            skLineSegment(sketch, "E802", {"start": v(8.08, 7.8) * mm, "end": v(8.1, 7.77) * mm});
            skLineSegment(sketch, "E803", {"start": v(8.1, 7.77) * mm, "end": v(8.16, 7.76) * mm});
            skLineSegment(sketch, "E804", {"start": v(8.16, 7.76) * mm, "end": v(8.2, 7.74) * mm});
            skLineSegment(sketch, "E805", {"start": v(8.2, 7.74) * mm, "end": v(8.22, 7.7) * mm});
            skLineSegment(sketch, "E806", {"start": v(8.22, 7.7) * mm, "end": v(8.26, 7.66) * mm});
            skLineSegment(sketch, "E807", {"start": v(8.26, 7.66) * mm, "end": v(8.28, 7.6) * mm});
            skLineSegment(sketch, "E808", {"start": v(8.28, 7.6) * mm, "end": v(8.28, 7.5) * mm});
            skLineSegment(sketch, "E809", {"start": v(8.28, 7.5) * mm, "end": v(8.32, 7.5) * mm});
            skLineSegment(sketch, "E810", {"start": v(8.32, 7.5) * mm, "end": v(8.34, 7.53) * mm});
            skLineSegment(sketch, "E811", {"start": v(8.34, 7.53) * mm, "end": v(8.38, 7.53) * mm});
            skLineSegment(sketch, "E812", {"start": v(8.38, 7.53) * mm, "end": v(8.41, 7.48) * mm});
            skLineSegment(sketch, "E813", {"start": v(8.41, 7.48) * mm, "end": v(8.45, 7.46) * mm});
            skLineSegment(sketch, "E814", {"start": v(8.45, 7.46) * mm, "end": v(8.42, 7.4) * mm});
            skLineSegment(sketch, "E815", {"start": v(8.42, 7.4) * mm, "end": v(8.42, 7.34) * mm});
            skLineSegment(sketch, "E816", {"start": v(8.42, 7.34) * mm, "end": v(8.45, 7.28) * mm});
            skLineSegment(sketch, "E817", {"start": v(8.45, 7.28) * mm, "end": v(8.51, 7.25) * mm});
            skLineSegment(sketch, "E818", {"start": v(8.51, 7.25) * mm, "end": v(8.56, 7.23) * mm});
            skLineSegment(sketch, "E819", {"start": v(8.56, 7.23) * mm, "end": v(8.61, 7.18) * mm});
            skLineSegment(sketch, "E820", {"start": v(8.61, 7.18) * mm, "end": v(8.66, 7.09) * mm});
            skLineSegment(sketch, "E821", {"start": v(8.66, 7.09) * mm, "end": v(8.75, 7.04) * mm});
            skLineSegment(sketch, "E822", {"start": v(8.75, 7.04) * mm, "end": v(8.82, 6.98) * mm});
            skLineSegment(sketch, "E823", {"start": v(8.82, 6.98) * mm, "end": v(8.92, 6.9) * mm});
            skLineSegment(sketch, "E824", {"start": v(8.92, 6.9) * mm, "end": v(8.94, 6.96) * mm});
            skLineSegment(sketch, "E825", {"start": v(8.94, 6.96) * mm, "end": v(8.97, 6.99) * mm});
            skLineSegment(sketch, "E826", {"start": v(8.97, 6.99) * mm, "end": v(9, 7) * mm});
            skLineSegment(sketch, "E827", {"start": v(9, 7) * mm, "end": v(9.02, 6.95) * mm});
            skLineSegment(sketch, "E828", {"start": v(9.02, 6.95) * mm, "end": v(9, 6.9) * mm});
            skLineSegment(sketch, "E829", {"start": v(9, 6.9) * mm, "end": v(8.98, 6.8) * mm});
            skLineSegment(sketch, "E830", {"start": v(8.98, 6.8) * mm, "end": v(8.99, 6.72) * mm});
            skLineSegment(sketch, "E831", {"start": v(8.99, 6.72) * mm, "end": v(8.94, 6.6) * mm});
            skLineSegment(sketch, "E832", {"start": v(8.94, 6.6) * mm, "end": v(8.98, 6.53) * mm});
            skLineSegment(sketch, "E833", {"start": v(8.98, 6.53) * mm, "end": v(9, 6.46) * mm});
            skLineSegment(sketch, "E834", {"start": v(9, 6.46) * mm, "end": v(8.99, 6.39) * mm});
            skLineSegment(sketch, "E835", {"start": v(8.99, 6.39) * mm, "end": v(8.96, 6.32) * mm});
            skLineSegment(sketch, "E836", {"start": v(8.96, 6.32) * mm, "end": v(8.93, 6.26) * mm});
            skLineSegment(sketch, "E837", {"start": v(8.93, 6.26) * mm, "end": v(8.92, 6.23) * mm});
            skLineSegment(sketch, "E838", {"start": v(8.92, 6.23) * mm, "end": v(8.96, 6.23) * mm});
            skLineSegment(sketch, "E839", {"start": v(8.96, 6.23) * mm, "end": v(9, 6.27) * mm});
            skLineSegment(sketch, "E840", {"start": v(9, 6.27) * mm, "end": v(9.05, 6.34) * mm});
            skLineSegment(sketch, "E841", {"start": v(9.05, 6.34) * mm, "end": v(9.09, 6.38) * mm});
            skLineSegment(sketch, "E842", {"start": v(9.09, 6.38) * mm, "end": v(9.13, 6.42) * mm});
            skLineSegment(sketch, "E843", {"start": v(9.13, 6.42) * mm, "end": v(9.19, 6.46) * mm});
            skLineSegment(sketch, "E844", {"start": v(9.19, 6.46) * mm, "end": v(9.22, 6.5) * mm});
            skLineSegment(sketch, "E845", {"start": v(9.22, 6.5) * mm, "end": v(9.25, 6.52) * mm});
            skLineSegment(sketch, "E846", {"start": v(9.25, 6.52) * mm, "end": v(9.27, 6.55) * mm});
            skLineSegment(sketch, "E847", {"start": v(9.27, 6.55) * mm, "end": v(9.28, 6.61) * mm});
            skLineSegment(sketch, "E848", {"start": v(9.28, 6.61) * mm, "end": v(9.27, 6.65) * mm});
            skLineSegment(sketch, "E849", {"start": v(9.27, 6.65) * mm, "end": v(9.25, 6.62) * mm});
            skLineSegment(sketch, "E850", {"start": v(9.25, 6.62) * mm, "end": v(9.22, 6.6) * mm});
            skLineSegment(sketch, "E851", {"start": v(9.22, 6.6) * mm, "end": v(9.2, 6.64) * mm});
            skLineSegment(sketch, "E852", {"start": v(9.2, 6.64) * mm, "end": v(9.19, 6.68) * mm});
            skLineSegment(sketch, "E853", {"start": v(9.19, 6.68) * mm, "end": v(9.2, 6.88) * mm});
            skLineSegment(sketch, "E854", {"start": v(9.2, 6.88) * mm, "end": v(9.27, 7) * mm});
            skLineSegment(sketch, "E855", {"start": v(9.27, 7) * mm, "end": v(9.35, 7.17) * mm});
            skLineSegment(sketch, "E856", {"start": v(9.35, 7.17) * mm, "end": v(9.42, 7.26) * mm});
            skLineSegment(sketch, "E857", {"start": v(9.42, 7.26) * mm, "end": v(9.5, 7.31) * mm});
            skLineSegment(sketch, "E858", {"start": v(9.5, 7.31) * mm, "end": v(9.57, 7.37) * mm});
            skLineSegment(sketch, "E859", {"start": v(9.57, 7.37) * mm, "end": v(9.63, 7.44) * mm});
            skLineSegment(sketch, "E860", {"start": v(9.63, 7.44) * mm, "end": v(9.67, 7.52) * mm});
            skLineSegment(sketch, "E861", {"start": v(9.67, 7.52) * mm, "end": v(9.74, 7.65) * mm});
            skLineSegment(sketch, "E862", {"start": v(9.74, 7.65) * mm, "end": v(9.81, 7.76) * mm});
            skLineSegment(sketch, "E863", {"start": v(9.81, 7.76) * mm, "end": v(9.91, 7.87) * mm});
            skLineSegment(sketch, "E864", {"start": v(9.91, 7.87) * mm, "end": v(9.98, 7.95) * mm});
            skLineSegment(sketch, "E865", {"start": v(9.98, 7.95) * mm, "end": v(10.04, 8) * mm});
            skLineSegment(sketch, "E866", {"start": v(10.04, 8) * mm, "end": v(10.08, 8) * mm});
            skLineSegment(sketch, "E867", {"start": v(10.08, 8) * mm, "end": v(10.08, 7.95) * mm});
            skLineSegment(sketch, "E868", {"start": v(10.08, 7.95) * mm, "end": v(10.13, 7.94) * mm});
            skLineSegment(sketch, "E869", {"start": v(10.13, 7.94) * mm, "end": v(10.16, 7.98) * mm});
            skLineSegment(sketch, "E870", {"start": v(10.16, 7.98) * mm, "end": v(10.21, 8.02) * mm});
            skLineSegment(sketch, "E871", {"start": v(10.21, 8.02) * mm, "end": v(10.27, 8.07) * mm});
            skLineSegment(sketch, "E872", {"start": v(10.27, 8.07) * mm, "end": v(10.33, 8.13) * mm});
            skLineSegment(sketch, "E873", {"start": v(10.33, 8.13) * mm, "end": v(10.46, 8.29) * mm});
            skLineSegment(sketch, "E874", {"start": v(10.46, 8.29) * mm, "end": v(10.5, 8.36) * mm});
            skLineSegment(sketch, "E875", {"start": v(10.5, 8.36) * mm, "end": v(10.54, 8.42) * mm});
            skLineSegment(sketch, "E876", {"start": v(10.54, 8.42) * mm, "end": v(10.62, 8.44) * mm});
            skLineSegment(sketch, "E877", {"start": v(10.62, 8.44) * mm, "end": v(10.68, 8.47) * mm});
            skLineSegment(sketch, "E878", {"start": v(10.68, 8.47) * mm, "end": v(10.78, 8.53) * mm});
            skLineSegment(sketch, "E879", {"start": v(10.78, 8.53) * mm, "end": v(10.85, 8.56) * mm});
            skLineSegment(sketch, "E880", {"start": v(10.85, 8.56) * mm, "end": v(10.9, 8.64) * mm});
            skLineSegment(sketch, "E881", {"start": v(10.9, 8.64) * mm, "end": v(10.91, 8.74) * mm});
            skLineSegment(sketch, "E882", {"start": v(10.91, 8.74) * mm, "end": v(10.96, 8.81) * mm});
            skLineSegment(sketch, "E883", {"start": v(10.96, 8.81) * mm, "end": v(11, 8.85) * mm});
            skLineSegment(sketch, "E884", {"start": v(11, 8.85) * mm, "end": v(11.05, 8.9) * mm});
            skLineSegment(sketch, "E885", {"start": v(11.05, 8.9) * mm, "end": v(11.06, 8.93) * mm});
            skLineSegment(sketch, "E886", {"start": v(11.06, 8.93) * mm, "end": v(11.09, 8.9) * mm});
            skLineSegment(sketch, "E887", {"start": v(11.09, 8.9) * mm, "end": v(11.09, 8.86) * mm});
            skLineSegment(sketch, "E888", {"start": v(11.09, 8.86) * mm, "end": v(11.11, 8.86) * mm});
            skLineSegment(sketch, "E889", {"start": v(11.11, 8.86) * mm, "end": v(11.17, 8.92) * mm});
            skLineSegment(sketch, "E890", {"start": v(11.17, 8.92) * mm, "end": v(11.2, 8.97) * mm});
            skLineSegment(sketch, "E891", {"start": v(11.2, 8.97) * mm, "end": v(11.22, 9.02) * mm});
            skLineSegment(sketch, "E892", {"start": v(11.22, 9.02) * mm, "end": v(11.27, 9.06) * mm});
            skLineSegment(sketch, "E893", {"start": v(11.27, 9.06) * mm, "end": v(11.3, 9.05) * mm});
            skLineSegment(sketch, "E894", {"start": v(11.3, 9.05) * mm, "end": v(11.34, 9.02) * mm});
            skLineSegment(sketch, "E895", {"start": v(11.34, 9.02) * mm, "end": v(11.35, 8.97) * mm});
            skLineSegment(sketch, "E896", {"start": v(11.35, 8.97) * mm, "end": v(11.35, 8.92) * mm});
            skLineSegment(sketch, "E897", {"start": v(11.35, 8.92) * mm, "end": v(11.38, 8.9) * mm});
            skLineSegment(sketch, "E898", {"start": v(11.38, 8.9) * mm, "end": v(11.4, 8.87) * mm});
            skLineSegment(sketch, "E899", {"start": v(11.4, 8.87) * mm, "end": v(11.44, 8.87) * mm});
            skLineSegment(sketch, "E900", {"start": v(11.44, 8.87) * mm, "end": v(11.45, 8.9) * mm});
            skLineSegment(sketch, "E901", {"start": v(11.45, 8.9) * mm, "end": v(11.48, 8.91) * mm});
            skLineSegment(sketch, "E902", {"start": v(11.48, 8.91) * mm, "end": v(11.5, 8.95) * mm});
            skLineSegment(sketch, "E903", {"start": v(11.5, 8.95) * mm, "end": v(11.52, 8.96) * mm});
            skLineSegment(sketch, "E904", {"start": v(11.52, 8.96) * mm, "end": v(11.57, 8.96) * mm});
            skLineSegment(sketch, "E905", {"start": v(11.57, 8.96) * mm, "end": v(11.6, 8.93) * mm});
            skLineSegment(sketch, "E906", {"start": v(11.6, 8.93) * mm, "end": v(11.61, 8.9) * mm});
            skLineSegment(sketch, "E907", {"start": v(11.61, 8.9) * mm, "end": v(11.6, 8.88) * mm});
            skLineSegment(sketch, "E908", {"start": v(11.6, 8.88) * mm, "end": v(11.55, 8.84) * mm});
            skLineSegment(sketch, "E909", {"start": v(11.55, 8.84) * mm, "end": v(11.5, 8.79) * mm});
            skLineSegment(sketch, "E910", {"start": v(11.5, 8.79) * mm, "end": v(11.43, 8.72) * mm});
            skLineSegment(sketch, "E911", {"start": v(11.43, 8.72) * mm, "end": v(11.39, 8.67) * mm});
            skLineSegment(sketch, "E912", {"start": v(11.39, 8.67) * mm, "end": v(11.39, 8.62) * mm});
            skLineSegment(sketch, "E913", {"start": v(11.39, 8.62) * mm, "end": v(11.4, 8.6) * mm});
            skLineSegment(sketch, "E914", {"start": v(11.4, 8.6) * mm, "end": v(11.5, 8.59) * mm});
            skLineSegment(sketch, "E915", {"start": v(11.5, 8.59) * mm, "end": v(11.52, 8.57) * mm});
            skLineSegment(sketch, "E916", {"start": v(11.52, 8.57) * mm, "end": v(11.48, 8.52) * mm});
            skLineSegment(sketch, "E917", {"start": v(11.48, 8.52) * mm, "end": v(11.48, 8.45) * mm});
            skLineSegment(sketch, "E918", {"start": v(11.48, 8.45) * mm, "end": v(11.52, 8.42) * mm});
            skLineSegment(sketch, "E919", {"start": v(11.52, 8.42) * mm, "end": v(11.6, 8.45) * mm});
            skLineSegment(sketch, "E920", {"start": v(11.6, 8.45) * mm, "end": v(11.7, 8.45) * mm});
            skLineSegment(sketch, "E921", {"start": v(11.7, 8.45) * mm, "end": v(11.75, 8.4) * mm});
            skLineSegment(sketch, "E922", {"start": v(11.75, 8.4) * mm, "end": v(11.78, 8.32) * mm});
            skLineSegment(sketch, "E923", {"start": v(11.78, 8.32) * mm, "end": v(11.83, 8.27) * mm});
            skLineSegment(sketch, "E924", {"start": v(11.83, 8.27) * mm, "end": v(11.93, 8.25) * mm});
            skLineSegment(sketch, "E925", {"start": v(11.93, 8.25) * mm, "end": v(11.99, 8.32) * mm});
            skLineSegment(sketch, "E926", {"start": v(11.99, 8.32) * mm, "end": v(12.08, 8.34) * mm});
            skLineSegment(sketch, "E927", {"start": v(12.08, 8.34) * mm, "end": v(12.13, 8.37) * mm});
            skLineSegment(sketch, "E928", {"start": v(12.13, 8.37) * mm, "end": v(12.14, 8.45) * mm});
            skLineSegment(sketch, "E929", {"start": v(12.14, 8.45) * mm, "end": v(12.2, 8.5) * mm});
            skLineSegment(sketch, "E930", {"start": v(12.2, 8.5) * mm, "end": v(12.28, 8.5) * mm});
            skLineSegment(sketch, "E931", {"start": v(12.28, 8.5) * mm, "end": v(12.3, 8.53) * mm});
            skLineSegment(sketch, "E932", {"start": v(12.3, 8.53) * mm, "end": v(12.35, 8.53) * mm});
            skLineSegment(sketch, "E933", {"start": v(12.35, 8.53) * mm, "end": v(12.4, 8.47) * mm});
            skLineSegment(sketch, "E934", {"start": v(12.4, 8.47) * mm, "end": v(12.47, 8.47) * mm});
            skLineSegment(sketch, "E935", {"start": v(12.47, 8.47) * mm, "end": v(12.54, 8.55) * mm});
            skLineSegment(sketch, "E936", {"start": v(12.54, 8.55) * mm, "end": v(12.58, 8.6) * mm});
            skLineSegment(sketch, "E937", {"start": v(12.58, 8.6) * mm, "end": v(12.65, 8.6) * mm});
            skLineSegment(sketch, "E938", {"start": v(12.65, 8.6) * mm, "end": v(12.68, 8.57) * mm});
            skLineSegment(sketch, "E939", {"start": v(12.68, 8.57) * mm, "end": v(12.67, 8.51) * mm});
            skLineSegment(sketch, "E940", {"start": v(12.67, 8.51) * mm, "end": v(12.65, 8.47) * mm});
            skLineSegment(sketch, "E941", {"start": v(12.65, 8.47) * mm, "end": v(12.61, 8.44) * mm});
            skLineSegment(sketch, "E942", {"start": v(12.61, 8.44) * mm, "end": v(12.62, 8.4) * mm});
            skLineSegment(sketch, "E943", {"start": v(12.62, 8.4) * mm, "end": v(12.67, 8.37) * mm});
            skLineSegment(sketch, "E944", {"start": v(12.67, 8.37) * mm, "end": v(12.72, 8.39) * mm});
            skLineSegment(sketch, "E945", {"start": v(12.72, 8.39) * mm, "end": v(12.76, 8.42) * mm});
            skLineSegment(sketch, "E946", {"start": v(12.76, 8.42) * mm, "end": v(12.78, 8.48) * mm});
            skLineSegment(sketch, "E947", {"start": v(12.78, 8.48) * mm, "end": v(12.82, 8.53) * mm});
            skLineSegment(sketch, "E948", {"start": v(12.82, 8.53) * mm, "end": v(12.9, 8.56) * mm});
            skLineSegment(sketch, "E949", {"start": v(12.9, 8.56) * mm, "end": v(12.94, 8.59) * mm});
            skLineSegment(sketch, "E950", {"start": v(12.94, 8.59) * mm, "end": v(13.01, 8.6) * mm});
            skLineSegment(sketch, "E951", {"start": v(13.01, 8.6) * mm, "end": v(13.1, 8.6) * mm});
            skLineSegment(sketch, "E952", {"start": v(13.1, 8.6) * mm, "end": v(13.17, 8.56) * mm});
            skLineSegment(sketch, "E953", {"start": v(13.17, 8.56) * mm, "end": v(13.22, 8.5) * mm});
            skLineSegment(sketch, "E954", {"start": v(13.22, 8.5) * mm, "end": v(13.22, 8.44) * mm});
            skLineSegment(sketch, "E955", {"start": v(13.22, 8.44) * mm, "end": v(13.21, 8.38) * mm});
            skLineSegment(sketch, "E956", {"start": v(13.21, 8.38) * mm, "end": v(13.17, 8.34) * mm});
            skLineSegment(sketch, "E957", {"start": v(13.17, 8.34) * mm, "end": v(13.15, 8.3) * mm});
            skLineSegment(sketch, "E958", {"start": v(13.15, 8.3) * mm, "end": v(13.14, 8.28) * mm});
            skLineSegment(sketch, "E959", {"start": v(13.14, 8.28) * mm, "end": v(13.16, 8.26) * mm});
            skLineSegment(sketch, "E960", {"start": v(13.16, 8.26) * mm, "end": v(13.22, 8.23) * mm});
            skLineSegment(sketch, "E961", {"start": v(13.22, 8.23) * mm, "end": v(13.3, 8.24) * mm});
            skLineSegment(sketch, "E962", {"start": v(13.3, 8.24) * mm, "end": v(13.37, 8.32) * mm});
            skLineSegment(sketch, "E963", {"start": v(13.37, 8.32) * mm, "end": v(13.43, 8.38) * mm});
            skLineSegment(sketch, "E964", {"start": v(13.43, 8.38) * mm, "end": v(13.44, 8.46) * mm});
            skLineSegment(sketch, "E965", {"start": v(13.44, 8.46) * mm, "end": v(13.35, 8.57) * mm});
            skLineSegment(sketch, "E966", {"start": v(13.35, 8.57) * mm, "end": v(13.38, 8.66) * mm});
            skLineSegment(sketch, "E967", {"start": v(13.38, 8.66) * mm, "end": v(13.38, 8.77) * mm});
            skLineSegment(sketch, "E968", {"start": v(13.38, 8.77) * mm, "end": v(13.4, 8.8) * mm});
            skLineSegment(sketch, "E969", {"start": v(13.4, 8.8) * mm, "end": v(13.45, 8.86) * mm});
            skLineSegment(sketch, "E970", {"start": v(13.45, 8.86) * mm, "end": v(13.51, 8.92) * mm});
            skLineSegment(sketch, "E971", {"start": v(13.51, 8.92) * mm, "end": v(13.57, 8.97) * mm});
            skLineSegment(sketch, "E972", {"start": v(13.57, 8.97) * mm, "end": v(13.6, 9) * mm});
            skLineSegment(sketch, "E973", {"start": v(13.6, 9) * mm, "end": v(13.62, 9.02) * mm});
            skLineSegment(sketch, "E974", {"start": v(13.62, 9.02) * mm, "end": v(13.66, 9.02) * mm});
            skLineSegment(sketch, "E975", {"start": v(13.66, 9.02) * mm, "end": v(13.68, 9) * mm});
            skLineSegment(sketch, "E976", {"start": v(13.68, 9) * mm, "end": v(13.7, 8.98) * mm});
            skLineSegment(sketch, "E977", {"start": v(13.7, 8.98) * mm, "end": v(13.74, 8.94) * mm});
            skLineSegment(sketch, "E978", {"start": v(13.74, 8.94) * mm, "end": v(13.78, 8.9) * mm});
            skLineSegment(sketch, "E979", {"start": v(13.78, 8.9) * mm, "end": v(13.81, 8.85) * mm});
            skLineSegment(sketch, "E980", {"start": v(13.81, 8.85) * mm, "end": v(13.85, 8.83) * mm});
            skLineSegment(sketch, "E981", {"start": v(13.85, 8.83) * mm, "end": v(13.88, 8.81) * mm});
            skLineSegment(sketch, "E982", {"start": v(13.88, 8.81) * mm, "end": v(13.9, 8.8) * mm});
            skLineSegment(sketch, "E983", {"start": v(13.9, 8.8) * mm, "end": v(13.91, 8.77) * mm});
            skLineSegment(sketch, "E984", {"start": v(13.91, 8.77) * mm, "end": v(13.94, 8.77) * mm});
            skLineSegment(sketch, "E985", {"start": v(13.94, 8.77) * mm, "end": v(13.96, 8.8) * mm});
            skLineSegment(sketch, "E986", {"start": v(13.96, 8.8) * mm, "end": v(13.98, 8.82) * mm});
            skLineSegment(sketch, "E987", {"start": v(13.98, 8.82) * mm, "end": v(14.1, 8.92) * mm});
            skLineSegment(sketch, "E988", {"start": v(14.1, 8.92) * mm, "end": v(14.19, 8.99) * mm});
            skLineSegment(sketch, "E989", {"start": v(14.19, 8.99) * mm, "end": v(14.22, 9.02) * mm});
            skLineSegment(sketch, "E990", {"start": v(14.22, 9.02) * mm, "end": v(14.26, 9.02) * mm});
            skLineSegment(sketch, "E991", {"start": v(14.26, 9.02) * mm, "end": v(14.28, 9) * mm});
            skLineSegment(sketch, "E992", {"start": v(14.28, 9) * mm, "end": v(14.28, 8.9) * mm});
            skLineSegment(sketch, "E993", {"start": v(14.28, 8.9) * mm, "end": v(14.24, 8.86) * mm});
            skLineSegment(sketch, "E994", {"start": v(14.24, 8.86) * mm, "end": v(14.2, 8.83) * mm});
            skLineSegment(sketch, "E995", {"start": v(14.2, 8.83) * mm, "end": v(14.2, 8.8) * mm});
            skLineSegment(sketch, "E996", {"start": v(14.2, 8.8) * mm, "end": v(14.22, 8.75) * mm});
            skLineSegment(sketch, "E997", {"start": v(14.22, 8.75) * mm, "end": v(14.25, 8.7) * mm});
            skLineSegment(sketch, "E998", {"start": v(14.25, 8.7) * mm, "end": v(14.25, 8.62) * mm});
            skLineSegment(sketch, "E999", {"start": v(14.25, 8.62) * mm, "end": v(14.2, 8.55) * mm});
            skLineSegment(sketch, "E1000", {"start": v(14.2, 8.55) * mm, "end": v(14.18, 8.48) * mm});
            skLineSegment(sketch, "E1001", {"start": v(14.18, 8.48) * mm, "end": v(14.15, 8.45) * mm});
            skLineSegment(sketch, "E1002", {"start": v(14.15, 8.45) * mm, "end": v(14.13, 8.42) * mm});
            skLineSegment(sketch, "E1003", {"start": v(14.13, 8.42) * mm, "end": v(14.09, 8.42) * mm});
            skLineSegment(sketch, "E1004", {"start": v(14.09, 8.42) * mm, "end": v(14.06, 8.45) * mm});
            skLineSegment(sketch, "E1005", {"start": v(14.06, 8.45) * mm, "end": v(14.03, 8.45) * mm});
            skLineSegment(sketch, "E1006", {"start": v(14.03, 8.45) * mm, "end": v(14, 8.42) * mm});
            skLineSegment(sketch, "E1007", {"start": v(14, 8.42) * mm, "end": v(13.98, 8.4) * mm});
            skLineSegment(sketch, "E1008", {"start": v(13.98, 8.4) * mm, "end": v(13.98, 8.3) * mm});
            skLineSegment(sketch, "E1009", {"start": v(13.98, 8.3) * mm, "end": v(14.06, 8.2) * mm});
            skLineSegment(sketch, "E1010", {"start": v(14.06, 8.2) * mm, "end": v(14.06, 8.16) * mm});
            skLineSegment(sketch, "E1011", {"start": v(14.06, 8.16) * mm, "end": v(14.03, 8.12) * mm});
            skLineSegment(sketch, "E1012", {"start": v(14.03, 8.12) * mm, "end": v(13.99, 8.07) * mm});
            skLineSegment(sketch, "E1013", {"start": v(13.99, 8.07) * mm, "end": v(13.94, 8.01) * mm});
            skLineSegment(sketch, "E1014", {"start": v(13.94, 8.01) * mm, "end": v(13.91, 7.97) * mm});
            skLineSegment(sketch, "E1015", {"start": v(13.91, 7.97) * mm, "end": v(13.89, 7.92) * mm});
            skLineSegment(sketch, "E1016", {"start": v(13.89, 7.92) * mm, "end": v(13.84, 7.87) * mm});
            skLineSegment(sketch, "E1017", {"start": v(13.84, 7.87) * mm, "end": v(13.8, 7.83) * mm});
            skLineSegment(sketch, "E1018", {"start": v(13.8, 7.83) * mm, "end": v(13.82, 7.8) * mm});
            skLineSegment(sketch, "E1019", {"start": v(13.82, 7.8) * mm, "end": v(13.88, 7.8) * mm});
            skLineSegment(sketch, "E1020", {"start": v(13.88, 7.8) * mm, "end": v(13.9, 7.81) * mm});
            skLineSegment(sketch, "E1021", {"start": v(13.9, 7.81) * mm, "end": v(13.93, 7.83) * mm});
            skLineSegment(sketch, "E1022", {"start": v(13.93, 7.83) * mm, "end": v(13.97, 7.82) * mm});
            skLineSegment(sketch, "E1023", {"start": v(13.97, 7.82) * mm, "end": v(13.98, 7.8) * mm});
            skLineSegment(sketch, "E1024", {"start": v(13.98, 7.8) * mm, "end": v(14.02, 7.77) * mm});
            skLineSegment(sketch, "E1025", {"start": v(14.02, 7.77) * mm, "end": v(14.06, 7.74) * mm});
            skLineSegment(sketch, "E1026", {"start": v(14.06, 7.74) * mm, "end": v(14.1, 7.73) * mm});
            skLineSegment(sketch, "E1027", {"start": v(14.1, 7.73) * mm, "end": v(14.14, 7.71) * mm});
            skLineSegment(sketch, "E1028", {"start": v(14.14, 7.71) * mm, "end": v(14.12, 7.68) * mm});
            skLineSegment(sketch, "E1029", {"start": v(14.12, 7.68) * mm, "end": v(14.1, 7.65) * mm});
            skLineSegment(sketch, "E1030", {"start": v(14.1, 7.65) * mm, "end": v(14.09, 7.61) * mm});
            skLineSegment(sketch, "E1031", {"start": v(14.09, 7.61) * mm, "end": v(14.12, 7.6) * mm});
            skLineSegment(sketch, "E1032", {"start": v(14.12, 7.6) * mm, "end": v(14.19, 7.64) * mm});
            skLineSegment(sketch, "E1033", {"start": v(14.19, 7.64) * mm, "end": v(14.23, 7.68) * mm});
            skLineSegment(sketch, "E1034", {"start": v(14.23, 7.68) * mm, "end": v(14.24, 7.68) * mm});
            skLineSegment(sketch, "E1035", {"start": v(14.24, 7.68) * mm, "end": v(14.27, 7.66) * mm});
            skLineSegment(sketch, "E1036", {"start": v(14.27, 7.66) * mm, "end": v(14.3, 7.63) * mm});
            skLineSegment(sketch, "E1037", {"start": v(14.3, 7.63) * mm, "end": v(14.3, 7.57) * mm});
            skLineSegment(sketch, "E1038", {"start": v(14.3, 7.57) * mm, "end": v(14.3, 7.55) * mm});
            skLineSegment(sketch, "E1039", {"start": v(14.3, 7.55) * mm, "end": v(14.3, 7.53) * mm});
            skLineSegment(sketch, "E1040", {"start": v(14.3, 7.53) * mm, "end": v(14.33, 7.5) * mm});
            skLineSegment(sketch, "E1041", {"start": v(14.33, 7.5) * mm, "end": v(14.35, 7.5) * mm});
            skLineSegment(sketch, "E1042", {"start": v(14.35, 7.5) * mm, "end": v(14.41, 7.55) * mm});
            skLineSegment(sketch, "E1043", {"start": v(14.41, 7.55) * mm, "end": v(14.45, 7.57) * mm});
            skLineSegment(sketch, "E1044", {"start": v(14.45, 7.57) * mm, "end": v(14.47, 7.58) * mm});
            skLineSegment(sketch, "E1045", {"start": v(14.47, 7.58) * mm, "end": v(14.5, 7.57) * mm});
            skLineSegment(sketch, "E1046", {"start": v(14.5, 7.57) * mm, "end": v(14.52, 7.54) * mm});
            skLineSegment(sketch, "E1047", {"start": v(14.52, 7.54) * mm, "end": v(14.52, 7.51) * mm});
            skLineSegment(sketch, "E1048", {"start": v(14.52, 7.51) * mm, "end": v(14.5, 7.5) * mm});
            skLineSegment(sketch, "E1049", {"start": v(14.5, 7.5) * mm, "end": v(14.51, 7.47) * mm});
            skLineSegment(sketch, "E1050", {"start": v(14.51, 7.47) * mm, "end": v(14.55, 7.45) * mm});
            skLineSegment(sketch, "E1051", {"start": v(14.55, 7.45) * mm, "end": v(14.6, 7.42) * mm});
            skLineSegment(sketch, "E1052", {"start": v(14.6, 7.42) * mm, "end": v(14.64, 7.39) * mm});
            skLineSegment(sketch, "E1053", {"start": v(14.64, 7.39) * mm, "end": v(14.68, 7.32) * mm});
            skLineSegment(sketch, "E1054", {"start": v(14.68, 7.32) * mm, "end": v(14.73, 7.2) * mm});
            skLineSegment(sketch, "E1055", {"start": v(14.73, 7.2) * mm, "end": v(14.76, 7.13) * mm});
            skLineSegment(sketch, "E1056", {"start": v(14.76, 7.13) * mm, "end": v(14.8, 7.07) * mm});
            skLineSegment(sketch, "E1057", {"start": v(14.8, 7.07) * mm, "end": v(14.86, 7.02) * mm});
            skLineSegment(sketch, "E1058", {"start": v(14.86, 7.02) * mm, "end": v(14.93, 7) * mm});
            skLineSegment(sketch, "E1059", {"start": v(14.93, 7) * mm, "end": v(15.03, 6.99) * mm});
            skLineSegment(sketch, "E1060", {"start": v(15.03, 6.99) * mm, "end": v(15.1, 6.95) * mm});
            skLineSegment(sketch, "E1061", {"start": v(15.1, 6.95) * mm, "end": v(15.19, 6.9) * mm});
            skLineSegment(sketch, "E1062", {"start": v(15.19, 6.9) * mm, "end": v(15.26, 6.9) * mm});
            skLineSegment(sketch, "E1063", {"start": v(15.26, 6.9) * mm, "end": v(15.32, 6.92) * mm});
            skLineSegment(sketch, "E1064", {"start": v(15.32, 6.92) * mm, "end": v(15.35, 6.9) * mm});
            skLineSegment(sketch, "E1065", {"start": v(15.35, 6.9) * mm, "end": v(15.39, 6.88) * mm});
            skLineSegment(sketch, "E1066", {"start": v(15.39, 6.88) * mm, "end": v(15.3, 6.8) * mm});
            skLineSegment(sketch, "E1067", {"start": v(15.3, 6.8) * mm, "end": v(15.26, 6.75) * mm});
            skLineSegment(sketch, "E1068", {"start": v(15.26, 6.75) * mm, "end": v(15.15, 6.59) * mm});
            skLineSegment(sketch, "E1069", {"start": v(15.15, 6.59) * mm, "end": v(15.14, 6.5) * mm});
            skLineSegment(sketch, "E1070", {"start": v(15.14, 6.5) * mm, "end": v(15.18, 6.47) * mm});
            skLineSegment(sketch, "E1071", {"start": v(15.18, 6.47) * mm, "end": v(15.21, 6.5) * mm});
            skLineSegment(sketch, "E1072", {"start": v(15.21, 6.5) * mm, "end": v(15.27, 6.5) * mm});
            skLineSegment(sketch, "E1073", {"start": v(15.27, 6.5) * mm, "end": v(15.33, 6.43) * mm});
            skLineSegment(sketch, "E1074", {"start": v(15.33, 6.43) * mm, "end": v(15.42, 6.32) * mm});
            skLineSegment(sketch, "E1075", {"start": v(15.42, 6.32) * mm, "end": v(15.48, 6.24) * mm});
            skLineSegment(sketch, "E1076", {"start": v(15.48, 6.24) * mm, "end": v(15.49, 6.16) * mm});
            skLineSegment(sketch, "E1077", {"start": v(15.49, 6.16) * mm, "end": v(15.44, 6.07) * mm});
            skLineSegment(sketch, "E1078", {"start": v(15.44, 6.07) * mm, "end": v(15.4, 5.96) * mm});
            skLineSegment(sketch, "E1079", {"start": v(15.4, 5.96) * mm, "end": v(15.37, 5.85) * mm});
            skLineSegment(sketch, "E1080", {"start": v(15.37, 5.85) * mm, "end": v(15.3, 5.74) * mm});
            skLineSegment(sketch, "E1081", {"start": v(15.3, 5.74) * mm, "end": v(15.27, 5.64) * mm});
            skLineSegment(sketch, "E1082", {"start": v(15.27, 5.64) * mm, "end": v(15.3, 5.64) * mm});
            skLineSegment(sketch, "E1083", {"start": v(15.3, 5.64) * mm, "end": v(15.37, 5.68) * mm});
            skLineSegment(sketch, "E1084", {"start": v(15.37, 5.68) * mm, "end": v(15.38, 5.6) * mm});
            skLineSegment(sketch, "E1085", {"start": v(15.38, 5.6) * mm, "end": v(15.33, 5.5) * mm});
            skLineSegment(sketch, "E1086", {"start": v(15.33, 5.5) * mm, "end": v(15.32, 5.47) * mm});
            skLineSegment(sketch, "E1087", {"start": v(15.32, 5.47) * mm, "end": v(15.32, 5.42) * mm});
            skLineSegment(sketch, "E1088", {"start": v(15.32, 5.42) * mm, "end": v(15.35, 5.4) * mm});
            skLineSegment(sketch, "E1089", {"start": v(15.35, 5.4) * mm, "end": v(15.33, 5.36) * mm});
            skLineSegment(sketch, "E1090", {"start": v(15.33, 5.36) * mm, "end": v(15.3, 5.3) * mm});
            skLineSegment(sketch, "E1091", {"start": v(15.3, 5.3) * mm, "end": v(15.28, 5.2) * mm});
            skLineSegment(sketch, "E1092", {"start": v(15.28, 5.2) * mm, "end": v(15.27, 5.13) * mm});
            skLineSegment(sketch, "E1093", {"start": v(15.27, 5.13) * mm, "end": v(15.25, 5.1) * mm});
            skLineSegment(sketch, "E1094", {"start": v(15.25, 5.1) * mm, "end": v(15.25, 5.06) * mm});
            skLineSegment(sketch, "E1095", {"start": v(15.25, 5.06) * mm, "end": v(15.32, 5.06) * mm});
            skLineSegment(sketch, "E1096", {"start": v(15.32, 5.06) * mm, "end": v(15.32, 4.97) * mm});
            skLineSegment(sketch, "E1097", {"start": v(15.32, 4.97) * mm, "end": v(15.34, 4.88) * mm});
            skLineSegment(sketch, "E1098", {"start": v(15.34, 4.88) * mm, "end": v(15.32, 4.8) * mm});
            skLineSegment(sketch, "E1099", {"start": v(15.32, 4.8) * mm, "end": v(15.3, 4.73) * mm});
            skLineSegment(sketch, "E1100", {"start": v(15.3, 4.73) * mm, "end": v(15.27, 4.68) * mm});
            skLineSegment(sketch, "E1101", {"start": v(15.27, 4.68) * mm, "end": v(15.3, 4.64) * mm});
            skLineSegment(sketch, "E1102", {"start": v(15.3, 4.64) * mm, "end": v(15.38, 4.65) * mm});
            skLineSegment(sketch, "E1103", {"start": v(15.38, 4.65) * mm, "end": v(15.42, 4.58) * mm});
            skLineSegment(sketch, "E1104", {"start": v(15.42, 4.58) * mm, "end": v(15.4, 4.5) * mm});
            skLineSegment(sketch, "E1105", {"start": v(15.4, 4.5) * mm, "end": v(15.45, 4.45) * mm});
            skLineSegment(sketch, "E1106", {"start": v(15.45, 4.45) * mm, "end": v(15.5, 4.45) * mm});
            skLineSegment(sketch, "E1107", {"start": v(15.5, 4.45) * mm, "end": v(15.52, 4.37) * mm});
            skLineSegment(sketch, "E1108", {"start": v(15.52, 4.37) * mm, "end": v(15.54, 4.34) * mm});
            skLineSegment(sketch, "E1109", {"start": v(15.54, 4.34) * mm, "end": v(15.57, 4.37) * mm});
            skLineSegment(sketch, "E1110", {"start": v(15.57, 4.37) * mm, "end": v(15.63, 4.38) * mm});
            skLineSegment(sketch, "E1111", {"start": v(15.63, 4.38) * mm, "end": v(15.66, 4.35) * mm});
            skLineSegment(sketch, "E1112", {"start": v(15.66, 4.35) * mm, "end": v(15.64, 4.26) * mm});
            skLineSegment(sketch, "E1113", {"start": v(15.64, 4.26) * mm, "end": v(15.6, 4.18) * mm});
            skLineSegment(sketch, "E1114", {"start": v(15.6, 4.18) * mm, "end": v(15.59, 4.07) * mm});
            skLineSegment(sketch, "E1115", {"start": v(15.59, 4.07) * mm, "end": v(15.56, 4.02) * mm});
            skLineSegment(sketch, "E1116", {"start": v(15.56, 4.02) * mm, "end": v(15.6, 3.96) * mm});
            skLineSegment(sketch, "E1117", {"start": v(15.6, 3.96) * mm, "end": v(15.64, 3.84) * mm});
            skLineSegment(sketch, "E1118", {"start": v(15.64, 3.84) * mm, "end": v(15.62, 3.73) * mm});
            skLineSegment(sketch, "E1119", {"start": v(15.62, 3.73) * mm, "end": v(15.54, 3.63) * mm});
            skLineSegment(sketch, "E1120", {"start": v(15.54, 3.63) * mm, "end": v(15.47, 3.55) * mm});
            skLineSegment(sketch, "E1121", {"start": v(15.47, 3.55) * mm, "end": v(15.48, 3.49) * mm});
            skLineSegment(sketch, "E1122", {"start": v(15.48, 3.49) * mm, "end": v(15.55, 3.47) * mm});
            skLineSegment(sketch, "E1123", {"start": v(15.55, 3.47) * mm, "end": v(15.62, 3.53) * mm});
            skLineSegment(sketch, "E1124", {"start": v(15.62, 3.53) * mm, "end": v(15.7, 3.57) * mm});
            skLineSegment(sketch, "E1125", {"start": v(15.7, 3.57) * mm, "end": v(15.76, 3.55) * mm});
            skLineSegment(sketch, "E1126", {"start": v(15.76, 3.55) * mm, "end": v(15.8, 3.47) * mm});
            skLineSegment(sketch, "E1127", {"start": v(15.8, 3.47) * mm, "end": v(15.75, 3.42) * mm});
            skLineSegment(sketch, "E1128", {"start": v(15.75, 3.42) * mm, "end": v(15.7, 3.42) * mm});
            skLineSegment(sketch, "E1129", {"start": v(15.7, 3.42) * mm, "end": v(15.69, 3.33) * mm});
            skLineSegment(sketch, "E1130", {"start": v(15.69, 3.33) * mm, "end": v(15.64, 3.3) * mm});
            skLineSegment(sketch, "E1131", {"start": v(15.64, 3.3) * mm, "end": v(15.66, 3.23) * mm});
            skLineSegment(sketch, "E1132", {"start": v(15.66, 3.23) * mm, "end": v(15.7, 3.1) * mm});
            skLineSegment(sketch, "E1133", {"start": v(15.7, 3.1) * mm, "end": v(15.73, 2.96) * mm});
            skLineSegment(sketch, "E1134", {"start": v(15.73, 2.96) * mm, "end": v(15.7, 2.79) * mm});
            skLineSegment(sketch, "E1135", {"start": v(15.7, 2.79) * mm, "end": v(15.68, 2.54) * mm});
            skLineSegment(sketch, "E1136", {"start": v(15.68, 2.54) * mm, "end": v(15.72, 2.46) * mm});
            skLineSegment(sketch, "E1137", {"start": v(15.72, 2.46) * mm, "end": v(15.83, 2.5) * mm});
            skLineSegment(sketch, "E1138", {"start": v(15.83, 2.5) * mm, "end": v(15.9, 2.53) * mm});
            skLineSegment(sketch, "E1139", {"start": v(15.9, 2.53) * mm, "end": v(15.95, 2.45) * mm});
            skLineSegment(sketch, "E1140", {"start": v(15.95, 2.45) * mm, "end": v(16.05, 2.46) * mm});
            skLineSegment(sketch, "E1141", {"start": v(16.05, 2.46) * mm, "end": v(16, 2.35) * mm});
            skLineSegment(sketch, "E1142", {"start": v(16, 2.35) * mm, "end": v(15.95, 2.15) * mm});
            skLineSegment(sketch, "E1143", {"start": v(15.95, 2.15) * mm, "end": v(15.84, 2) * mm});
            skLineSegment(sketch, "E1144", {"start": v(15.84, 2) * mm, "end": v(15.88, 1.97) * mm});
            skLineSegment(sketch, "E1145", {"start": v(15.88, 1.97) * mm, "end": v(16.03, 1.98) * mm});
            skLineSegment(sketch, "E1146", {"start": v(16.03, 1.98) * mm, "end": v(16.16, 2.01) * mm});
            skLineSegment(sketch, "E1147", {"start": v(16.16, 2.01) * mm, "end": v(16.16, 1.94) * mm});
            skLineSegment(sketch, "E1148", {"start": v(16.16, 1.94) * mm, "end": v(16.2, 1.88) * mm});
            skLineSegment(sketch, "E1149", {"start": v(16.2, 1.88) * mm, "end": v(16.18, 1.81) * mm});
            skLineSegment(sketch, "E1150", {"start": v(16.18, 1.81) * mm, "end": v(16.17, 1.75) * mm});
            skLineSegment(sketch, "E1151", {"start": v(16.17, 1.75) * mm, "end": v(16.25, 1.73) * mm});
            skLineSegment(sketch, "E1152", {"start": v(16.25, 1.73) * mm, "end": v(16.3, 1.74) * mm});
            skLineSegment(sketch, "E1153", {"start": v(16.3, 1.74) * mm, "end": v(16.31, 1.67) * mm});
            skLineSegment(sketch, "E1154", {"start": v(16.31, 1.67) * mm, "end": v(16.27, 1.6) * mm});
            skLineSegment(sketch, "E1155", {"start": v(16.27, 1.6) * mm, "end": v(16.2, 1.5) * mm});
            skLineSegment(sketch, "E1156", {"start": v(16.2, 1.5) * mm, "end": v(16.1, 1.36) * mm});
            skLineSegment(sketch, "E1157", {"start": v(16.1, 1.36) * mm, "end": v(16.13, 1.22) * mm});
            skLineSegment(sketch, "E1158", {"start": v(16.13, 1.22) * mm, "end": v(16.02, 1.1) * mm});
            skLineSegment(sketch, "E1159", {"start": v(16.02, 1.1) * mm, "end": v(16.02, 0.93) * mm});
            skLineSegment(sketch, "E1160", {"start": v(16.02, 0.93) * mm, "end": v(15.92, 0.83) * mm});
            skLineSegment(sketch, "E1161", {"start": v(15.92, 0.83) * mm, "end": v(15.93, 0.79) * mm});
            skLineSegment(sketch, "E1162", {"start": v(15.93, 0.79) * mm, "end": v(15.98, 0.76) * mm});
            skLineSegment(sketch, "E1163", {"start": v(15.98, 0.76) * mm, "end": v(15.86, 0.55) * mm});
            skLineSegment(sketch, "E1164", {"start": v(15.86, 0.55) * mm, "end": v(15.76, 0.36) * mm});
            skLineSegment(sketch, "E1165", {"start": v(15.76, 0.36) * mm, "end": v(15.7, 0.29) * mm});
            skLineSegment(sketch, "E1166", {"start": v(15.7, 0.29) * mm, "end": v(15.67, 0.27) * mm});
            skLineSegment(sketch, "E1167", {"start": v(15.67, 0.27) * mm, "end": v(15.68, 0.24) * mm});
            skLineSegment(sketch, "E1168", {"start": v(15.68, 0.24) * mm, "end": v(15.72, 0.23) * mm});
            skLineSegment(sketch, "E1169", {"start": v(15.72, 0.23) * mm, "end": v(15.68, 0.1) * mm});
            skLineSegment(sketch, "E1170", {"start": v(15.68, 0.1) * mm, "end": v(15.62, 0.05) * mm});
            skLineSegment(sketch, "E1171", {"start": v(15.62, 0.05) * mm, "end": v(15.54, -0.02) * mm});
            skLineSegment(sketch, "E1172", {"start": v(15.54, -0.02) * mm, "end": v(15.46, -0.12) * mm});
            skLineSegment(sketch, "E1173", {"start": v(15.46, -0.12) * mm, "end": v(15.26, -0.17) * mm});
            skLineSegment(sketch, "E1174", {"start": v(15.26, -0.17) * mm, "end": v(15.23, -0.25) * mm});
            skLineSegment(sketch, "E1175", {"start": v(15.23, -0.25) * mm, "end": v(15.29, -0.29) * mm});
            skLineSegment(sketch, "E1176", {"start": v(15.29, -0.29) * mm, "end": v(15.21, -0.38) * mm});
            skLineSegment(sketch, "E1177", {"start": v(15.21, -0.38) * mm, "end": v(15.23, -0.45) * mm});
            skLineSegment(sketch, "E1178", {"start": v(15.23, -0.45) * mm, "end": v(15.27, -0.55) * mm});
            skLineSegment(sketch, "E1179", {"start": v(15.27, -0.55) * mm, "end": v(15.17, -0.64) * mm});
            skLineSegment(sketch, "E1180", {"start": v(15.17, -0.64) * mm, "end": v(15.1, -0.72) * mm});
            skLineSegment(sketch, "E1181", {"start": v(15.1, -0.72) * mm, "end": v(15.06, -0.84) * mm});
            skLineSegment(sketch, "E1182", {"start": v(15.06, -0.84) * mm, "end": v(14.88, -1.08) * mm});
            skLineSegment(sketch, "E1183", {"start": v(14.88, -1.08) * mm, "end": v(14.72, -1.07) * mm});
            skLineSegment(sketch, "E1184", {"start": v(14.72, -1.07) * mm, "end": v(14.66, -1.09) * mm});
            skLineSegment(sketch, "E1185", {"start": v(14.66, -1.09) * mm, "end": v(14.64, -1.15) * mm});
            skLineSegment(sketch, "E1186", {"start": v(14.64, -1.15) * mm, "end": v(14.68, -1.22) * mm});
            skLineSegment(sketch, "E1187", {"start": v(14.68, -1.22) * mm, "end": v(14.67, -1.3) * mm});
            skLineSegment(sketch, "E1188", {"start": v(14.67, -1.3) * mm, "end": v(14.66, -1.42) * mm});
            skLineSegment(sketch, "E1189", {"start": v(14.66, -1.42) * mm, "end": v(15.04, -1.9) * mm});
            skLineSegment(sketch, "E1190", {"start": v(15.04, -1.9) * mm, "end": v(15.13, -2.04) * mm});
            skLineSegment(sketch, "E1191", {"start": v(15.13, -2.04) * mm, "end": v(15.05, -2.07) * mm});
            skLineSegment(sketch, "E1192", {"start": v(15.05, -2.07) * mm, "end": v(14.97, -2.08) * mm});
            skLineSegment(sketch, "E1193", {"start": v(14.97, -2.08) * mm, "end": v(14.92, -2.16) * mm});
            skLineSegment(sketch, "E1194", {"start": v(14.92, -2.16) * mm, "end": v(14.99, -2.22) * mm});
            skLineSegment(sketch, "E1195", {"start": v(14.99, -2.22) * mm, "end": v(15.09, -2.3) * mm});
            skLineSegment(sketch, "E1196", {"start": v(15.09, -2.3) * mm, "end": v(15.2, -2.44) * mm});
            skLineSegment(sketch, "E1197", {"start": v(15.2, -2.44) * mm, "end": v(15.33, -2.86) * mm});
            skLineSegment(sketch, "E1198", {"start": v(15.33, -2.86) * mm, "end": v(15.17, -2.98) * mm});
            skLineSegment(sketch, "E1199", {"start": v(15.17, -2.98) * mm, "end": v(15.1, -3.03) * mm});
            skLineSegment(sketch, "E1200", {"start": v(15.1, -3.03) * mm, "end": v(15.13, -3.07) * mm});
            skLineSegment(sketch, "E1201", {"start": v(15.13, -3.07) * mm, "end": v(15.17, -3.12) * mm});
            skLineSegment(sketch, "E1202", {"start": v(15.17, -3.12) * mm, "end": v(15.07, -3.2) * mm});
            skLineSegment(sketch, "E1203", {"start": v(15.07, -3.2) * mm, "end": v(15.02, -3.27) * mm});
            skLineSegment(sketch, "E1204", {"start": v(15.02, -3.27) * mm, "end": v(15.03, -3.33) * mm});
            skLineSegment(sketch, "E1205", {"start": v(15.03, -3.33) * mm, "end": v(15.1, -3.38) * mm});
            skLineSegment(sketch, "E1206", {"start": v(15.1, -3.38) * mm, "end": v(15.18, -3.41) * mm});
            skLineSegment(sketch, "E1207", {"start": v(15.18, -3.41) * mm, "end": v(15.25, -3.51) * mm});
            skLineSegment(sketch, "E1208", {"start": v(15.25, -3.51) * mm, "end": v(15.33, -3.65) * mm});
            skLineSegment(sketch, "E1209", {"start": v(15.33, -3.65) * mm, "end": v(15.38, -3.76) * mm});
            skLineSegment(sketch, "E1210", {"start": v(15.38, -3.76) * mm, "end": v(15.6, -3.92) * mm});
            skLineSegment(sketch, "E1211", {"start": v(15.6, -3.92) * mm, "end": v(15.64, -4) * mm});
            skLineSegment(sketch, "E1212", {"start": v(15.64, -4) * mm, "end": v(15.47, -4.14) * mm});
            skLineSegment(sketch, "E1213", {"start": v(15.47, -4.14) * mm, "end": v(15.42, -4.15) * mm});
            skLineSegment(sketch, "E1214", {"start": v(15.42, -4.15) * mm, "end": v(15.43, -4.26) * mm});
            skLineSegment(sketch, "E1215", {"start": v(15.43, -4.26) * mm, "end": v(15.46, -4.3) * mm});
            skLineSegment(sketch, "E1216", {"start": v(15.46, -4.3) * mm, "end": v(15.55, -4.37) * mm});
            skLineSegment(sketch, "E1217", {"start": v(15.55, -4.37) * mm, "end": v(15.71, -4.57) * mm});
            skLineSegment(sketch, "E1218", {"start": v(15.71, -4.57) * mm, "end": v(15.75, -4.65) * mm});
            skLineSegment(sketch, "E1219", {"start": v(15.75, -4.65) * mm, "end": v(15.77, -4.77) * mm});
            skLineSegment(sketch, "E1220", {"start": v(15.77, -4.77) * mm, "end": v(15.7, -4.81) * mm});
            skLineSegment(sketch, "E1221", {"start": v(15.7, -4.81) * mm, "end": v(15.69, -4.76) * mm});
            skLineSegment(sketch, "E1222", {"start": v(15.69, -4.76) * mm, "end": v(15.67, -4.79) * mm});
            skLineSegment(sketch, "E1223", {"start": v(15.67, -4.79) * mm, "end": v(15.65, -4.81) * mm});
            skLineSegment(sketch, "E1224", {"start": v(15.65, -4.81) * mm, "end": v(15.62, -4.8) * mm});
            skLineSegment(sketch, "E1225", {"start": v(15.62, -4.8) * mm, "end": v(15.58, -4.76) * mm});
            skLineSegment(sketch, "E1226", {"start": v(15.58, -4.76) * mm, "end": v(15.52, -4.73) * mm});
            skLineSegment(sketch, "E1227", {"start": v(15.52, -4.73) * mm, "end": v(15.42, -4.68) * mm});
            skLineSegment(sketch, "E1228", {"start": v(15.42, -4.68) * mm, "end": v(15.36, -4.68) * mm});
            skLineSegment(sketch, "E1229", {"start": v(15.36, -4.68) * mm, "end": v(15.32, -4.65) * mm});
            skLineSegment(sketch, "E1230", {"start": v(15.32, -4.65) * mm, "end": v(15.29, -4.62) * mm});
            skLineSegment(sketch, "E1231", {"start": v(15.29, -4.62) * mm, "end": v(15.24, -4.59) * mm});
            skLineSegment(sketch, "E1232", {"start": v(15.24, -4.59) * mm, "end": v(15.17, -4.59) * mm});
            skLineSegment(sketch, "E1233", {"start": v(15.17, -4.59) * mm, "end": v(15.14, -4.65) * mm});
            skLineSegment(sketch, "E1234", {"start": v(15.14, -4.65) * mm, "end": v(15.13, -4.77) * mm});
            skLineSegment(sketch, "E1235", {"start": v(15.13, -4.77) * mm, "end": v(15.13, -4.87) * mm});
            skLineSegment(sketch, "E1236", {"start": v(15.13, -4.87) * mm, "end": v(15.07, -4.9) * mm});
            skLineSegment(sketch, "E1237", {"start": v(15.07, -4.9) * mm, "end": v(14.98, -4.82) * mm});
            skLineSegment(sketch, "E1238", {"start": v(14.98, -4.82) * mm, "end": v(14.85, -4.75) * mm});
            skLineSegment(sketch, "E1239", {"start": v(14.85, -4.75) * mm, "end": v(14.77, -4.64) * mm});
            skLineSegment(sketch, "E1240", {"start": v(14.77, -4.64) * mm, "end": v(14.68, -4.58) * mm});
            skLineSegment(sketch, "E1241", {"start": v(14.68, -4.58) * mm, "end": v(14.64, -4.55) * mm});
            skLineSegment(sketch, "E1242", {"start": v(14.64, -4.55) * mm, "end": v(14.59, -4.63) * mm});
            skLineSegment(sketch, "E1243", {"start": v(14.59, -4.63) * mm, "end": v(14.52, -4.62) * mm});
            skLineSegment(sketch, "E1244", {"start": v(14.52, -4.62) * mm, "end": v(14.46, -4.59) * mm});
            skLineSegment(sketch, "E1245", {"start": v(14.46, -4.59) * mm, "end": v(14.42, -4.56) * mm});
            skLineSegment(sketch, "E1246", {"start": v(14.42, -4.56) * mm, "end": v(14.35, -4.48) * mm});
            skLineSegment(sketch, "E1247", {"start": v(14.92, -4.26) * mm, "end": v(14.96, -4.34) * mm});
            skLineSegment(sketch, "E1248", {"start": v(14.96, -4.34) * mm, "end": v(15.03, -4.4) * mm});
            skLineSegment(sketch, "E1249", {"start": v(15.03, -4.4) * mm, "end": v(15.13, -4.42) * mm});
            skLineSegment(sketch, "E1250", {"start": v(15.13, -4.42) * mm, "end": v(15.15, -4.37) * mm});
            skLineSegment(sketch, "E1251", {"start": v(15.15, -4.37) * mm, "end": v(15.17, -4.34) * mm});
            skLineSegment(sketch, "E1252", {"start": v(15.17, -4.34) * mm, "end": v(15.15, -4.3) * mm});
            skLineSegment(sketch, "E1253", {"start": v(15.15, -4.3) * mm, "end": v(15.13, -4.28) * mm});
            skLineSegment(sketch, "E1254", {"start": v(15.13, -4.28) * mm, "end": v(15.27, -4.17) * mm});
            skLineSegment(sketch, "E1255", {"start": v(15.27, -4.17) * mm, "end": v(15.25, -4.07) * mm});
            skLineSegment(sketch, "E1256", {"start": v(15.25, -4.07) * mm, "end": v(15.17, -4.11) * mm});
            skLineSegment(sketch, "E1257", {"start": v(15.17, -4.11) * mm, "end": v(15.12, -4.12) * mm});
            skLineSegment(sketch, "E1258", {"start": v(15.12, -4.12) * mm, "end": v(15.07, -4.11) * mm});
            skLineSegment(sketch, "E1259", {"start": v(15.07, -4.11) * mm, "end": v(14.96, -4.2) * mm});
            skLineSegment(sketch, "E1260", {"start": v(14.96, -4.2) * mm, "end": v(14.93, -4.28) * mm});
            skLineSegment(sketch, "E1261", {"start": v(14.35, -4.47) * mm, "end": v(14.33, -4.45) * mm});
            skLineSegment(sketch, "E1262", {"start": v(14.33, -4.45) * mm, "end": v(14.26, -4.48) * mm});
            skLineSegment(sketch, "E1263", {"start": v(14.26, -4.48) * mm, "end": v(14.2, -4.46) * mm});
            skLineSegment(sketch, "E1264", {"start": v(14.2, -4.46) * mm, "end": v(14.08, -4.4) * mm});
            skLineSegment(sketch, "E1265", {"start": v(14.08, -4.4) * mm, "end": v(13.9, -4.26) * mm});
            skLineSegment(sketch, "E1266", {"start": v(13.9, -4.26) * mm, "end": v(13.7, -4.13) * mm});
            skLineSegment(sketch, "E1267", {"start": v(13.7, -4.13) * mm, "end": v(13.62, -4.13) * mm});
            skLineSegment(sketch, "E1268", {"start": v(13.62, -4.13) * mm, "end": v(13.6, -4.14) * mm});
            skLineSegment(sketch, "E1269", {"start": v(13.6, -4.14) * mm, "end": v(13.52, -4.11) * mm});
            skLineSegment(sketch, "E1270", {"start": v(13.52, -4.11) * mm, "end": v(13.28, -3.97) * mm});
            skLineSegment(sketch, "E1271", {"start": v(13.28, -3.97) * mm, "end": v(13.1, -3.85) * mm});
            skLineSegment(sketch, "E1272", {"start": v(13.1, -3.85) * mm, "end": v(12.89, -3.68) * mm});
            skLineSegment(sketch, "E1273", {"start": v(12.89, -3.68) * mm, "end": v(12.77, -3.57) * mm});
            skLineSegment(sketch, "E1274", {"start": v(12.77, -3.57) * mm, "end": v(12.7, -3.56) * mm});
            skLineSegment(sketch, "E1275", {"start": v(12.7, -3.56) * mm, "end": v(12.65, -3.58) * mm});
            skLineSegment(sketch, "E1276", {"start": v(12.65, -3.58) * mm, "end": v(12.52, -3.67) * mm});
            skLineSegment(sketch, "E1277", {"start": v(12.52, -3.67) * mm, "end": v(12.46, -3.74) * mm});
            skLineSegment(sketch, "E1278", {"start": v(12.46, -3.74) * mm, "end": v(12.44, -3.82) * mm});
            skLineSegment(sketch, "E1279", {"start": v(12.44, -3.82) * mm, "end": v(12.38, -3.83) * mm});
            skLineSegment(sketch, "E1280", {"start": v(12.38, -3.83) * mm, "end": v(12.34, -3.78) * mm});
            skLineSegment(sketch, "E1281", {"start": v(12.34, -3.78) * mm, "end": v(12.34, -3.66) * mm});
            skLineSegment(sketch, "E1282", {"start": v(12.34, -3.66) * mm, "end": v(12.26, -3.57) * mm});
            skLineSegment(sketch, "E1283", {"start": v(12.26, -3.57) * mm, "end": v(12.3, -3.5) * mm});
            skLineSegment(sketch, "E1284", {"start": v(12.3, -3.5) * mm, "end": v(12.35, -3.48) * mm});
            skLineSegment(sketch, "E1285", {"start": v(12.35, -3.48) * mm, "end": v(12.34, -3.32) * mm});
            skLineSegment(sketch, "E1286", {"start": v(12.34, -3.32) * mm, "end": v(12.3, -3.17) * mm});
            skLineSegment(sketch, "E1287", {"start": v(12.3, -3.17) * mm, "end": v(12.24, -3.02) * mm});
            skLineSegment(sketch, "E1288", {"start": v(12.24, -3.02) * mm, "end": v(12.17, -3) * mm});
            skLineSegment(sketch, "E1289", {"start": v(12.17, -3) * mm, "end": v(12.16, -2.92) * mm});
            skLineSegment(sketch, "E1290", {"start": v(12.16, -2.92) * mm, "end": v(12.2, -2.84) * mm});
            skLineSegment(sketch, "E1291", {"start": v(12.2, -2.84) * mm, "end": v(12.19, -2.8) * mm});
            skLineSegment(sketch, "E1292", {"start": v(12.19, -2.8) * mm, "end": v(12.15, -2.79) * mm});
            skLineSegment(sketch, "E1293", {"start": v(12.15, -2.79) * mm, "end": v(12.1, -2.82) * mm});
            skLineSegment(sketch, "E1294", {"start": v(12.1, -2.82) * mm, "end": v(12, -2.84) * mm});
            skLineSegment(sketch, "E1295", {"start": v(12, -2.84) * mm, "end": v(11.84, -2.83) * mm});
            skLineSegment(sketch, "E1296", {"start": v(11.84, -2.83) * mm, "end": v(11.77, -2.87) * mm});
            skLineSegment(sketch, "E1297", {"start": v(11.77, -2.87) * mm, "end": v(11.63, -3) * mm});
            skLineSegment(sketch, "E1298", {"start": v(11.63, -3) * mm, "end": v(11.52, -3.07) * mm});
            skLineSegment(sketch, "E1299", {"start": v(11.52, -3.07) * mm, "end": v(11.46, -3.09) * mm});
            skLineSegment(sketch, "E1300", {"start": v(11.46, -3.09) * mm, "end": v(11.4, -3.07) * mm});
            skLineSegment(sketch, "E1301", {"start": v(11.4, -3.07) * mm, "end": v(11.39, -3.04) * mm});
            skLineSegment(sketch, "E1302", {"start": v(11.39, -3.04) * mm, "end": v(11.37, -2.99) * mm});
            skLineSegment(sketch, "E1303", {"start": v(11.37, -2.99) * mm, "end": v(11.31, -2.95) * mm});
            skLineSegment(sketch, "E1304", {"start": v(11.31, -2.95) * mm, "end": v(11.25, -2.97) * mm});
            skLineSegment(sketch, "E1305", {"start": v(11.25, -2.97) * mm, "end": v(11.12, -2.96) * mm});
            skLineSegment(sketch, "E1306", {"start": v(11.12, -2.96) * mm, "end": v(11.06, -2.98) * mm});
            skLineSegment(sketch, "E1307", {"start": v(11.06, -2.98) * mm, "end": v(10.74, -3.25) * mm});
            skLineSegment(sketch, "E1308", {"start": v(10.74, -3.25) * mm, "end": v(10.39, -3.44) * mm});
            skLineSegment(sketch, "E1309", {"start": v(10.39, -3.44) * mm, "end": v(10.14, -3.55) * mm});
            skLineSegment(sketch, "E1310", {"start": v(10.14, -3.55) * mm, "end": v(9.9, -3.64) * mm});
            skLineSegment(sketch, "E1311", {"start": v(9.9, -3.64) * mm, "end": v(9.74, -3.68) * mm});
            skLineSegment(sketch, "E1312", {"start": v(9.74, -3.68) * mm, "end": v(9.57, -3.69) * mm});
            skLineSegment(sketch, "E1313", {"start": v(9.57, -3.69) * mm, "end": v(9.48, -3.76) * mm});
            skLineSegment(sketch, "E1314", {"start": v(9.48, -3.76) * mm, "end": v(9.36, -3.92) * mm});
            skLineSegment(sketch, "E1315", {"start": v(9.36, -3.92) * mm, "end": v(9.2, -4) * mm});
            skLineSegment(sketch, "E1316", {"start": v(9.2, -4) * mm, "end": v(9.16, -4.05) * mm});
            skLineSegment(sketch, "E1317", {"start": v(9.16, -4.05) * mm, "end": v(9.15, -4.1) * mm});
            skLineSegment(sketch, "E1318", {"start": v(9.15, -4.1) * mm, "end": v(9.17, -4.14) * mm});
            skLineSegment(sketch, "E1319", {"start": v(9.17, -4.14) * mm, "end": v(9.2, -4.15) * mm});
            skLineSegment(sketch, "E1320", {"start": v(9.2, -4.15) * mm, "end": v(9.26, -4.14) * mm});
            skLineSegment(sketch, "E1321", {"start": v(9.26, -4.14) * mm, "end": v(9.3, -4.14) * mm});
            skLineSegment(sketch, "E1322", {"start": v(9.3, -4.14) * mm, "end": v(9.3, -4.17) * mm});
            skLineSegment(sketch, "E1323", {"start": v(9.3, -4.17) * mm, "end": v(9.17, -4.26) * mm});
            skLineSegment(sketch, "E1324", {"start": v(9.17, -4.26) * mm, "end": v(9.09, -4.34) * mm});
            skLineSegment(sketch, "E1325", {"start": v(9.09, -4.34) * mm, "end": v(8.92, -4.46) * mm});
            skLineSegment(sketch, "E1326", {"start": v(8.92, -4.46) * mm, "end": v(8.86, -4.46) * mm});
            skLineSegment(sketch, "E1327", {"start": v(8.86, -4.46) * mm, "end": v(8.87, -4.4) * mm});
            skLineSegment(sketch, "E1328", {"start": v(8.87, -4.4) * mm, "end": v(8.92, -4.3) * mm});
            skLineSegment(sketch, "E1329", {"start": v(8.92, -4.3) * mm, "end": v(8.96, -4.23) * mm});
            skLineSegment(sketch, "E1330", {"start": v(8.96, -4.23) * mm, "end": v(8.91, -4.21) * mm});
            skLineSegment(sketch, "E1331", {"start": v(8.91, -4.21) * mm, "end": v(8.8, -4.25) * mm});
            skLineSegment(sketch, "E1332", {"start": v(8.8, -4.25) * mm, "end": v(8.67, -4.33) * mm});
            skLineSegment(sketch, "E1333", {"start": v(8.67, -4.33) * mm, "end": v(8.69, -4.4) * mm});
            skLineSegment(sketch, "E1334", {"start": v(8.69, -4.4) * mm, "end": v(8.72, -4.46) * mm});
            skLineSegment(sketch, "E1335", {"start": v(8.72, -4.46) * mm, "end": v(8.7, -4.55) * mm});
            skLineSegment(sketch, "E1336", {"start": v(8.7, -4.55) * mm, "end": v(8.66, -4.6) * mm});
            skLineSegment(sketch, "E1337", {"start": v(8.66, -4.6) * mm, "end": v(8.63, -4.69) * mm});
            skLineSegment(sketch, "E1338", {"start": v(8.63, -4.69) * mm, "end": v(8.52, -4.78) * mm});
            skLineSegment(sketch, "E1339", {"start": v(8.52, -4.78) * mm, "end": v(8.47, -4.8) * mm});
            skLineSegment(sketch, "E1340", {"start": v(8.47, -4.8) * mm, "end": v(8.41, -4.8) * mm});
            skLineSegment(sketch, "E1341", {"start": v(8.41, -4.8) * mm, "end": v(8.44, -4.73) * mm});
            skLineSegment(sketch, "E1342", {"start": v(8.44, -4.73) * mm, "end": v(8.42, -4.68) * mm});
            skLineSegment(sketch, "E1343", {"start": v(8.42, -4.68) * mm, "end": v(8.36, -4.66) * mm});
            skLineSegment(sketch, "E1344", {"start": v(8.36, -4.66) * mm, "end": v(8.3, -4.7) * mm});
            skLineSegment(sketch, "E1345", {"start": v(8.3, -4.7) * mm, "end": v(8.23, -4.8) * mm});
            skLineSegment(sketch, "E1346", {"start": v(8.23, -4.8) * mm, "end": v(8.14, -4.9) * mm});
            skLineSegment(sketch, "E1347", {"start": v(8.14, -4.9) * mm, "end": v(7.92, -5.13) * mm});
            skLineSegment(sketch, "E1348", {"start": v(7.92, -5.13) * mm, "end": v(7.74, -5.27) * mm});
            skLineSegment(sketch, "E1349", {"start": v(7.74, -5.27) * mm, "end": v(7.67, -5.34) * mm});
            skLineSegment(sketch, "E1350", {"start": v(7.67, -5.34) * mm, "end": v(7.67, -5.37) * mm});
            skLineSegment(sketch, "E1351", {"start": v(7.67, -5.37) * mm, "end": v(7.73, -5.4) * mm});
            skLineSegment(sketch, "E1352", {"start": v(7.73, -5.4) * mm, "end": v(7.7, -5.47) * mm});
            skLineSegment(sketch, "E1353", {"start": v(7.7, -5.47) * mm, "end": v(7.53, -5.62) * mm});
            skLineSegment(sketch, "E1354", {"start": v(7.13, -5.87) * mm, "end": v(7.05, -5.9) * mm});
            skLineSegment(sketch, "E1355", {"start": v(14.35, -4.48) * mm, "end": v(14.35, -4.47) * mm});
            skLineSegment(sketch, "E1356", {"start": v(7.53, -5.62) * mm, "end": v(7.16, -5.9) * mm});
            skLineSegment(sketch, "E1357", {"start": v(7.16, -5.9) * mm, "end": v(7.13, -5.87) * mm});
            skLineSegment(sketch, "E1358", {"start": v(7.05, -5.9) * mm, "end": v(6.95, -5.97) * mm});
            skLineSegment(sketch, "E1359", {"start": v(6.95, -5.97) * mm, "end": v(6.9, -6.05) * mm});
            skLineSegment(sketch, "E1360", {"start": v(6.9, -6.05) * mm, "end": v(6.86, -6.08) * mm});
            skLineSegment(sketch, "E1361", {"start": v(6.86, -6.08) * mm, "end": v(6.85, -6.12) * mm});
            skLineSegment(sketch, "E1362", {"start": v(6.85, -6.12) * mm, "end": v(6.91, -6.14) * mm});
            skLineSegment(sketch, "E1363", {"start": v(6.91, -6.14) * mm, "end": v(6.94, -6.16) * mm});
            skLineSegment(sketch, "E1364", {"start": v(6.94, -6.16) * mm, "end": v(6.93, -6.18) * mm});
            skLineSegment(sketch, "E1365", {"start": v(6.93, -6.18) * mm, "end": v(6.87, -6.24) * mm});
            skLineSegment(sketch, "E1366", {"start": v(6.87, -6.24) * mm, "end": v(6.77, -6.25) * mm});
            skLineSegment(sketch, "E1367", {"start": v(6.77, -6.25) * mm, "end": v(6.6, -6.37) * mm});
            skLineSegment(sketch, "E1368", {"start": v(6.6, -6.37) * mm, "end": v(6.6, -6.42) * mm});
            skLineSegment(sketch, "E1369", {"start": v(6.6, -6.42) * mm, "end": v(6.76, -6.51) * mm});
            skLineSegment(sketch, "E1370", {"start": v(6.76, -6.51) * mm, "end": v(6.75, -6.61) * mm});
            skLineSegment(sketch, "E1371", {"start": v(6.75, -6.61) * mm, "end": v(6.7, -6.67) * mm});
            skLineSegment(sketch, "E1372", {"start": v(6.7, -6.67) * mm, "end": v(6.55, -6.8) * mm});
            skLineSegment(sketch, "E1373", {"start": v(6.55, -6.8) * mm, "end": v(6.55, -6.9) * mm});
            skLineSegment(sketch, "E1374", {"start": v(6.55, -6.9) * mm, "end": v(6.6, -6.94) * mm});
            skLineSegment(sketch, "E1375", {"start": v(6.6, -6.94) * mm, "end": v(6.61, -7.01) * mm});
            skLineSegment(sketch, "E1376", {"start": v(6.61, -7.01) * mm, "end": v(6.43, -7.18) * mm});
            skLineSegment(sketch, "E1377", {"start": v(6.43, -7.18) * mm, "end": v(5.9, -7.67) * mm});
            skLineSegment(sketch, "E1378", {"start": v(5.9, -7.67) * mm, "end": v(5.2, -8.33) * mm});
            skLineSegment(sketch, "E1379", {"start": v(5.2, -8.33) * mm, "end": v(4.7, -8.8) * mm});
            skLineSegment(sketch, "E1380", {"start": v(4.7, -8.8) * mm, "end": v(4.67, -8.92) * mm});
            skLineSegment(sketch, "E1381", {"start": v(4.67, -8.92) * mm, "end": v(4.72, -9.02) * mm});
            skLineSegment(sketch, "E1382", {"start": v(4.72, -9.02) * mm, "end": v(4.78, -9.05) * mm});
            skLineSegment(sketch, "E1383", {"start": v(4.78, -9.05) * mm, "end": v(4.74, -9.1) * mm});
            skLineSegment(sketch, "E1384", {"start": v(4.74, -9.1) * mm, "end": v(4.64, -9.1) * mm});
            skLineSegment(sketch, "E1385", {"start": v(4.64, -9.1) * mm, "end": v(4.53, -9.18) * mm});
            skLineSegment(sketch, "E1386", {"start": v(4.53, -9.18) * mm, "end": v(4.44, -9.27) * mm});
            skLineSegment(sketch, "E1387", {"start": v(4.44, -9.27) * mm, "end": v(4.4, -9.2) * mm});
            skLineSegment(sketch, "E1388", {"start": v(4.4, -9.2) * mm, "end": v(4.25, -9.32) * mm});
            skLineSegment(sketch, "E1389", {"start": v(4.25, -9.32) * mm, "end": v(4.14, -9.32) * mm});
            skLineSegment(sketch, "E1390", {"start": v(4.14, -9.32) * mm, "end": v(4.01, -9.55) * mm});
            skLineSegment(sketch, "E1391", {"start": v(4.01, -9.55) * mm, "end": v(3.9, -9.65) * mm});
            skLineSegment(sketch, "E1392", {"start": v(3.9, -9.65) * mm, "end": v(3.9, -9.72) * mm});
            skLineSegment(sketch, "E1393", {"start": v(3.9, -9.72) * mm, "end": v(3.95, -9.82) * mm});
            skLineSegment(sketch, "E1394", {"start": v(3.95, -9.82) * mm, "end": v(4.02, -9.9) * mm});
            skLineSegment(sketch, "E1395", {"start": v(4.02, -9.9) * mm, "end": v(4, -9.94) * mm});
            skLineSegment(sketch, "E1396", {"start": v(4, -9.94) * mm, "end": v(3.93, -9.95) * mm});
            skLineSegment(sketch, "E1397", {"start": v(3.93, -9.95) * mm, "end": v(3.93, -10.02) * mm});
            skLineSegment(sketch, "E1398", {"start": v(3.93, -10.02) * mm, "end": v(3.89, -10.08) * mm});
            skLineSegment(sketch, "E1399", {"start": v(3.89, -10.08) * mm, "end": v(3.88, -10.13) * mm});
            skLineSegment(sketch, "E1400", {"start": v(3.88, -10.13) * mm, "end": v(3.83, -10.14) * mm});
            skLineSegment(sketch, "E1401", {"start": v(3.83, -10.14) * mm, "end": v(3.76, -10.09) * mm});
            skLineSegment(sketch, "E1402", {"start": v(3.76, -10.09) * mm, "end": v(3.68, -10.1) * mm});
            skLineSegment(sketch, "E1403", {"start": v(3.68, -10.1) * mm, "end": v(3.57, -10.23) * mm});
            skLineSegment(sketch, "E1404", {"start": v(3.57, -10.23) * mm, "end": v(3.48, -10.25) * mm});
            skLineSegment(sketch, "E1405", {"start": v(3.48, -10.25) * mm, "end": v(3.46, -10.22) * mm});
            skLineSegment(sketch, "E1406", {"start": v(3.46, -10.22) * mm, "end": v(3.39, -10.22) * mm});
            skLineSegment(sketch, "E1407", {"start": v(3.39, -10.22) * mm, "end": v(3.29, -10.3) * mm});
            skLineSegment(sketch, "E1408", {"start": v(3.29, -10.3) * mm, "end": v(3.22, -10.3) * mm});
            skLineSegment(sketch, "E1409", {"start": v(3.22, -10.3) * mm, "end": v(3.2, -10.26) * mm});
            skLineSegment(sketch, "E1410", {"start": v(3.2, -10.26) * mm, "end": v(3.12, -10.28) * mm});
            skLineSegment(sketch, "E1411", {"start": v(3.12, -10.28) * mm, "end": v(2.97, -10.45) * mm});
            skLineSegment(sketch, "E1412", {"start": v(2.97, -10.45) * mm, "end": v(2.91, -10.45) * mm});
            skLineSegment(sketch, "E1413", {"start": v(2.91, -10.45) * mm, "end": v(2.9, -10.42) * mm});
            skLineSegment(sketch, "E1414", {"start": v(2.9, -10.42) * mm, "end": v(2.87, -10.42) * mm});
            skLineSegment(sketch, "E1415", {"start": v(2.87, -10.42) * mm, "end": v(2.8, -10.49) * mm});
            skLineSegment(sketch, "E1416", {"start": v(2.8, -10.49) * mm, "end": v(2.79, -10.56) * mm});
            skLineSegment(sketch, "E1417", {"start": v(2.79, -10.56) * mm, "end": v(2.76, -10.58) * mm});
            skLineSegment(sketch, "E1418", {"start": v(2.76, -10.58) * mm, "end": v(2.74, -10.56) * mm});
            skLineSegment(sketch, "E1419", {"start": v(2.74, -10.56) * mm, "end": v(2.73, -10.44) * mm});
            skLineSegment(sketch, "E1420", {"start": v(2.73, -10.44) * mm, "end": v(2.73, -10.4) * mm});
            skLineSegment(sketch, "E1421", {"start": v(2.73, -10.4) * mm, "end": v(2.69, -10.4) * mm});
            skLineSegment(sketch, "E1422", {"start": v(2.69, -10.4) * mm, "end": v(2.63, -10.44) * mm});
            skLineSegment(sketch, "E1423", {"start": v(2.63, -10.44) * mm, "end": v(2.54, -10.47) * mm});
            skLineSegment(sketch, "E1424", {"start": v(2.54, -10.47) * mm, "end": v(2.47, -10.53) * mm});
            skLineSegment(sketch, "E1425", {"start": v(2.47, -10.53) * mm, "end": v(2.46, -10.61) * mm});
            skLineSegment(sketch, "E1426", {"start": v(2.46, -10.61) * mm, "end": v(2.55, -10.72) * mm});
            skLineSegment(sketch, "E1427", {"start": v(2.55, -10.72) * mm, "end": v(2.62, -10.74) * mm});
            skLineSegment(sketch, "E1428", {"start": v(2.62, -10.74) * mm, "end": v(2.66, -10.84) * mm});
            skLineSegment(sketch, "E1429", {"start": v(2.66, -10.84) * mm, "end": v(2.72, -10.93) * mm});
            skLineSegment(sketch, "E1430", {"start": v(2.72, -10.93) * mm, "end": v(2.77, -10.97) * mm});
            skLineSegment(sketch, "E1431", {"start": v(2.77, -10.97) * mm, "end": v(2.82, -10.96) * mm});
            skLineSegment(sketch, "E1432", {"start": v(2.82, -10.96) * mm, "end": v(2.84, -10.92) * mm});
            skLineSegment(sketch, "E1433", {"start": v(2.84, -10.92) * mm, "end": v(2.9, -10.9) * mm});
            skLineSegment(sketch, "E1434", {"start": v(2.9, -10.9) * mm, "end": v(2.9, -11) * mm});
            skLineSegment(sketch, "E1435", {"start": v(2.9, -11) * mm, "end": v(2.88, -11.03) * mm});
            skLineSegment(sketch, "E1436", {"start": v(2.88, -11.03) * mm, "end": v(2.9, -11.06) * mm});
            skLineSegment(sketch, "E1437", {"start": v(2.9, -11.06) * mm, "end": v(2.99, -11.13) * mm});
            skLineSegment(sketch, "E1438", {"start": v(2.99, -11.13) * mm, "end": v(3.09, -11.17) * mm});
            skLineSegment(sketch, "E1439", {"start": v(3.09, -11.17) * mm, "end": v(3.16, -11.25) * mm});
            skLineSegment(sketch, "E1440", {"start": v(3.16, -11.25) * mm, "end": v(3.31, -11.4) * mm});
            skLineSegment(sketch, "E1441", {"start": v(3.31, -11.4) * mm, "end": v(3.58, -11.54) * mm});
            skLineSegment(sketch, "E1442", {"start": v(3.58, -11.54) * mm, "end": v(3.65, -11.61) * mm});
            skLineSegment(sketch, "E1443", {"start": v(3.65, -11.61) * mm, "end": v(3.74, -11.67) * mm});
            skLineSegment(sketch, "E1444", {"start": v(3.74, -11.67) * mm, "end": v(3.83, -11.68) * mm});
            skLineSegment(sketch, "E1445", {"start": v(3.83, -11.68) * mm, "end": v(3.85, -11.64) * mm});
            skLineSegment(sketch, "E1446", {"start": v(3.85, -11.64) * mm, "end": v(3.9, -11.6) * mm});
            skLineSegment(sketch, "E1447", {"start": v(3.9, -11.6) * mm, "end": v(3.93, -11.62) * mm});
            skLineSegment(sketch, "E1448", {"start": v(3.93, -11.62) * mm, "end": v(3.92, -11.67) * mm});
            skLineSegment(sketch, "E1449", {"start": v(3.92, -11.67) * mm, "end": v(3.88, -11.7) * mm});
            skLineSegment(sketch, "E1450", {"start": v(3.88, -11.7) * mm, "end": v(3.89, -11.82) * mm});
            skLineSegment(sketch, "E1451", {"start": v(3.89, -11.82) * mm, "end": v(3.93, -11.87) * mm});
            skLineSegment(sketch, "E1452", {"start": v(3.93, -11.87) * mm, "end": v(4, -11.98) * mm});
            skLineSegment(sketch, "E1453", {"start": v(4, -11.98) * mm, "end": v(4.08, -12.03) * mm});
            skLineSegment(sketch, "E1454", {"start": v(4.08, -12.03) * mm, "end": v(4.2, -12.08) * mm});
            skLineSegment(sketch, "E1455", {"start": v(4.2, -12.08) * mm, "end": v(4.2, -12.03) * mm});
            skLineSegment(sketch, "E1456", {"start": v(4.2, -12.03) * mm, "end": v(4.21, -12) * mm});
            skLineSegment(sketch, "E1457", {"start": v(4.21, -12) * mm, "end": v(4.25, -12.03) * mm});
            skLineSegment(sketch, "E1458", {"start": v(4.25, -12.03) * mm, "end": v(4.29, -12.07) * mm});
            skLineSegment(sketch, "E1459", {"start": v(4.29, -12.07) * mm, "end": v(4.4, -12.19) * mm});
            skLineSegment(sketch, "E1460", {"start": v(4.4, -12.19) * mm, "end": v(4.55, -12.34) * mm});
            skLineSegment(sketch, "E1461", {"start": v(4.55, -12.34) * mm, "end": v(4.71, -12.5) * mm});
            skLineSegment(sketch, "E1462", {"start": v(4.71, -12.5) * mm, "end": v(4.7, -12.52) * mm});
            skLineSegment(sketch, "E1463", {"start": v(4.7, -12.52) * mm, "end": v(4.43, -12.39) * mm});
            skLineSegment(sketch, "E1464", {"start": v(4.43, -12.39) * mm, "end": v(4.34, -12.45) * mm});
            skLineSegment(sketch, "E1465", {"start": v(4.34, -12.45) * mm, "end": v(4.23, -12.4) * mm});
            skLineSegment(sketch, "E1466", {"start": v(4.23, -12.4) * mm, "end": v(4.17, -12.35) * mm});
            skLineSegment(sketch, "E1467", {"start": v(4.17, -12.35) * mm, "end": v(4.08, -12.33) * mm});
            skLineSegment(sketch, "E1468", {"start": v(4.08, -12.33) * mm, "end": v(3.73, -12.18) * mm});
            skLineSegment(sketch, "E1469", {"start": v(3.73, -12.18) * mm, "end": v(3.68, -12.16) * mm});
            skLineSegment(sketch, "E1470", {"start": v(3.68, -12.16) * mm, "end": v(3.6, -12.1) * mm});
            skLineSegment(sketch, "E1471", {"start": v(3.6, -12.1) * mm, "end": v(3.6, -12.04) * mm});
            skLineSegment(sketch, "E1472", {"start": v(3.6, -12.04) * mm, "end": v(3.56, -12.04) * mm});
            skLineSegment(sketch, "E1473", {"start": v(3.56, -12.04) * mm, "end": v(3.5, -12.1) * mm});
            skLineSegment(sketch, "E1474", {"start": v(3.5, -12.1) * mm, "end": v(3.46, -12.08) * mm});
            skLineSegment(sketch, "E1475", {"start": v(3.46, -12.08) * mm, "end": v(3.45, -12.04) * mm});
            skLineSegment(sketch, "E1476", {"start": v(3.45, -12.04) * mm, "end": v(3.5, -12) * mm});
            skLineSegment(sketch, "E1477", {"start": v(3.5, -12) * mm, "end": v(3.4, -11.93) * mm});
            skLineSegment(sketch, "E1478", {"start": v(3.4, -11.93) * mm, "end": v(3.37, -11.85) * mm});
            skLineSegment(sketch, "E1479", {"start": v(3.37, -11.85) * mm, "end": v(3.3, -11.77) * mm});
            skLineSegment(sketch, "E1480", {"start": v(3.3, -11.77) * mm, "end": v(3.24, -11.78) * mm});
            skLineSegment(sketch, "E1481", {"start": v(3.24, -11.78) * mm, "end": v(3.28, -11.81) * mm});
            skLineSegment(sketch, "E1482", {"start": v(3.28, -11.81) * mm, "end": v(3.29, -11.84) * mm});
            skLineSegment(sketch, "E1483", {"start": v(3.29, -11.84) * mm, "end": v(3.22, -11.9) * mm});
            skLineSegment(sketch, "E1484", {"start": v(3.22, -11.9) * mm, "end": v(3.2, -11.96) * mm});
            skLineSegment(sketch, "E1485", {"start": v(3.2, -11.96) * mm, "end": v(3.14, -11.97) * mm});
            skLineSegment(sketch, "E1486", {"start": v(3.14, -11.97) * mm, "end": v(3.1, -11.92) * mm});
            skLineSegment(sketch, "E1487", {"start": v(3.1, -11.92) * mm, "end": v(3.14, -11.88) * mm});
            skLineSegment(sketch, "E1488", {"start": v(3.14, -11.88) * mm, "end": v(3.17, -11.86) * mm});
            skLineSegment(sketch, "E1489", {"start": v(3.17, -11.86) * mm, "end": v(3.16, -11.83) * mm});
            skLineSegment(sketch, "E1490", {"start": v(3.16, -11.83) * mm, "end": v(3.12, -11.83) * mm});
            skLineSegment(sketch, "E1491", {"start": v(3.12, -11.83) * mm, "end": v(3.08, -11.84) * mm});
            skLineSegment(sketch, "E1492", {"start": v(3.08, -11.84) * mm, "end": v(3.05, -11.89) * mm});
            skLineSegment(sketch, "E1493", {"start": v(3.05, -11.89) * mm, "end": v(3.02, -11.92) * mm});
            skLineSegment(sketch, "E1494", {"start": v(3.02, -11.92) * mm, "end": v(3, -11.97) * mm});
            skLineSegment(sketch, "E1495", {"start": v(3, -11.97) * mm, "end": v(2.98, -12) * mm});
            skLineSegment(sketch, "E1496", {"start": v(2.98, -12) * mm, "end": v(2.9, -12) * mm});
            skLineSegment(sketch, "E1497", {"start": v(2.9, -12) * mm, "end": v(2.85, -11.96) * mm});
            skLineSegment(sketch, "E1498", {"start": v(2.85, -11.96) * mm, "end": v(2.8, -11.9) * mm});
            skLineSegment(sketch, "E1499", {"start": v(2.8, -11.9) * mm, "end": v(2.78, -11.85) * mm});
            skLineSegment(sketch, "E1500", {"start": v(2.78, -11.85) * mm, "end": v(2.76, -11.82) * mm});
            skLineSegment(sketch, "E1501", {"start": v(2.76, -11.82) * mm, "end": v(2.71, -11.78) * mm});
            skLineSegment(sketch, "E1502", {"start": v(2.71, -11.78) * mm, "end": v(2.64, -11.78) * mm});
            skLineSegment(sketch, "E1503", {"start": v(2.64, -11.78) * mm, "end": v(2.6, -11.75) * mm});
            skLineSegment(sketch, "E1504", {"start": v(2.6, -11.75) * mm, "end": v(2.57, -11.7) * mm});
            skLineSegment(sketch, "E1505", {"start": v(2.57, -11.7) * mm, "end": v(2.48, -11.7) * mm});
            skLineSegment(sketch, "E1506", {"start": v(2.48, -11.7) * mm, "end": v(2.45, -11.75) * mm});
            skLineSegment(sketch, "E1507", {"start": v(2.45, -11.75) * mm, "end": v(2.45, -11.8) * mm});
            skLineSegment(sketch, "E1508", {"start": v(2.45, -11.8) * mm, "end": v(2.47, -11.8) * mm});
            skLineSegment(sketch, "E1509", {"start": v(2.47, -11.8) * mm, "end": v(2.47, -11.89) * mm});
            skLineSegment(sketch, "E1510", {"start": v(2.47, -11.89) * mm, "end": v(2.43, -11.94) * mm});
            skLineSegment(sketch, "E1511", {"start": v(2.43, -11.94) * mm, "end": v(2.4, -11.94) * mm});
            skLineSegment(sketch, "E1512", {"start": v(2.4, -11.94) * mm, "end": v(2.38, -12) * mm});
            skLineSegment(sketch, "E1513", {"start": v(2.38, -12) * mm, "end": v(2.32, -12) * mm});
            skLineSegment(sketch, "E1514", {"start": v(2.32, -12) * mm, "end": v(2.3, -11.98) * mm});
            skLineSegment(sketch, "E1515", {"start": v(2.3, -11.98) * mm, "end": v(2.3, -11.95) * mm});
            skLineSegment(sketch, "E1516", {"start": v(2.3, -11.95) * mm, "end": v(2.35, -11.94) * mm});
            skLineSegment(sketch, "E1517", {"start": v(2.35, -11.94) * mm, "end": v(2.38, -11.94) * mm});
            skLineSegment(sketch, "E1518", {"start": v(2.38, -11.94) * mm, "end": v(2.4, -11.91) * mm});
            skLineSegment(sketch, "E1519", {"start": v(2.4, -11.91) * mm, "end": v(2.4, -11.86) * mm});
            skLineSegment(sketch, "E1520", {"start": v(2.4, -11.86) * mm, "end": v(2.35, -11.81) * mm});
            skLineSegment(sketch, "E1521", {"start": v(2.35, -11.81) * mm, "end": v(2.3, -11.78) * mm});
            skLineSegment(sketch, "E1522", {"start": v(2.3, -11.78) * mm, "end": v(2.26, -11.76) * mm});
            skLineSegment(sketch, "E1523", {"start": v(2.26, -11.76) * mm, "end": v(2.21, -11.72) * mm});
            skLineSegment(sketch, "E1524", {"start": v(2.21, -11.72) * mm, "end": v(2.2, -11.6) * mm});
            skLineSegment(sketch, "E1525", {"start": v(2.2, -11.6) * mm, "end": v(2.18, -11.56) * mm});
            skLineSegment(sketch, "E1526", {"start": v(2.18, -11.56) * mm, "end": v(2.16, -11.54) * mm});
            skLineSegment(sketch, "E1527", {"start": v(2.16, -11.54) * mm, "end": v(2.12, -11.54) * mm});
            skLineSegment(sketch, "E1528", {"start": v(2.12, -11.54) * mm, "end": v(2.12, -11.56) * mm});
            skLineSegment(sketch, "E1529", {"start": v(2.12, -11.56) * mm, "end": v(2.17, -11.63) * mm});
            skLineSegment(sketch, "E1530", {"start": v(2.17, -11.63) * mm, "end": v(2.14, -11.64) * mm});
            skLineSegment(sketch, "E1531", {"start": v(2.14, -11.64) * mm, "end": v(2.09, -11.6) * mm});
            skLineSegment(sketch, "E1532", {"start": v(2.09, -11.6) * mm, "end": v(2.06, -11.58) * mm});
            skLineSegment(sketch, "E1533", {"start": v(2.06, -11.58) * mm, "end": v(2.04, -11.55) * mm});
            skLineSegment(sketch, "E1534", {"start": v(2.04, -11.55) * mm, "end": v(2.04, -11.5) * mm});
            skLineSegment(sketch, "E1535", {"start": v(2.04, -11.5) * mm, "end": v(2.07, -11.49) * mm});
            skLineSegment(sketch, "E1536", {"start": v(2.07, -11.49) * mm, "end": v(2.07, -11.45) * mm});
            skLineSegment(sketch, "E1537", {"start": v(2.07, -11.45) * mm, "end": v(2.05, -11.43) * mm});
            skLineSegment(sketch, "E1538", {"start": v(2.05, -11.43) * mm, "end": v(2.04, -11.4) * mm});
            skLineSegment(sketch, "E1539", {"start": v(2.04, -11.4) * mm, "end": v(2.02, -11.38) * mm});
            skLineSegment(sketch, "E1540", {"start": v(2.02, -11.38) * mm, "end": v(2, -11.37) * mm});
            skLineSegment(sketch, "E1541", {"start": v(2, -11.37) * mm, "end": v(1.98, -11.4) * mm});
            skLineSegment(sketch, "E1542", {"start": v(1.98, -11.4) * mm, "end": v(1.95, -11.41) * mm});
            skLineSegment(sketch, "E1543", {"start": v(1.95, -11.41) * mm, "end": v(1.91, -11.4) * mm});
            skLineSegment(sketch, "E1544", {"start": v(1.91, -11.4) * mm, "end": v(1.9, -11.38) * mm});
            skLineSegment(sketch, "E1545", {"start": v(1.9, -11.38) * mm, "end": v(1.85, -11.38) * mm});
            skLineSegment(sketch, "E1546", {"start": v(1.85, -11.38) * mm, "end": v(1.83, -11.43) * mm});
            skLineSegment(sketch, "E1547", {"start": v(1.83, -11.43) * mm, "end": v(1.78, -11.47) * mm});
            skLineSegment(sketch, "E1548", {"start": v(1.78, -11.47) * mm, "end": v(1.78, -11.54) * mm});
            skLineSegment(sketch, "E1549", {"start": v(1.78, -11.54) * mm, "end": v(1.75, -11.57) * mm});
            skLineSegment(sketch, "E1550", {"start": v(1.75, -11.57) * mm, "end": v(1.69, -11.59) * mm});
            skLineSegment(sketch, "E1551", {"start": v(1.69, -11.59) * mm, "end": v(1.63, -11.6) * mm});
            skLineSegment(sketch, "E1552", {"start": v(1.63, -11.6) * mm, "end": v(1.6, -11.56) * mm});
            skLineSegment(sketch, "E1553", {"start": v(1.6, -11.56) * mm, "end": v(1.61, -11.52) * mm});
            skLineSegment(sketch, "E1554", {"start": v(1.61, -11.52) * mm, "end": v(1.59, -11.5) * mm});
            skLineSegment(sketch, "E1555", {"start": v(1.59, -11.5) * mm, "end": v(1.56, -11.52) * mm});
            skLineSegment(sketch, "E1556", {"start": v(1.56, -11.52) * mm, "end": v(1.54, -11.55) * mm});
            skLineSegment(sketch, "E1557", {"start": v(1.54, -11.55) * mm, "end": v(1.56, -11.6) * mm});
            skLineSegment(sketch, "E1558", {"start": v(1.56, -11.6) * mm, "end": v(1.58, -11.64) * mm});
            skLineSegment(sketch, "E1559", {"start": v(1.58, -11.64) * mm, "end": v(1.57, -11.7) * mm});
            skLineSegment(sketch, "E1560", {"start": v(1.57, -11.7) * mm, "end": v(1.55, -11.7) * mm});
            skLineSegment(sketch, "E1561", {"start": v(1.55, -11.7) * mm, "end": v(1.53, -11.67) * mm});
            skLineSegment(sketch, "E1562", {"start": v(1.53, -11.67) * mm, "end": v(1.5, -11.64) * mm});
            skLineSegment(sketch, "E1563", {"start": v(1.5, -11.64) * mm, "end": v(1.5, -11.62) * mm});
            skLineSegment(sketch, "E1564", {"start": v(1.5, -11.62) * mm, "end": v(1.49, -11.58) * mm});
            skLineSegment(sketch, "E1565", {"start": v(1.49, -11.58) * mm, "end": v(1.47, -11.55) * mm});
            skLineSegment(sketch, "E1566", {"start": v(1.47, -11.55) * mm, "end": v(1.43, -11.52) * mm});
            skLineSegment(sketch, "E1567", {"start": v(1.43, -11.52) * mm, "end": v(1.4, -11.47) * mm});
            skLineSegment(sketch, "E1568", {"start": v(1.4, -11.47) * mm, "end": v(1.38, -11.46) * mm});
            skLineSegment(sketch, "E1569", {"start": v(1.38, -11.46) * mm, "end": v(1.31, -11.43) * mm});
            skLineSegment(sketch, "E1570", {"start": v(1.31, -11.43) * mm, "end": v(1.3, -11.4) * mm});
            skLineSegment(sketch, "E1571", {"start": v(1.3, -11.4) * mm, "end": v(1.3, -11.36) * mm});
            skLineSegment(sketch, "E1572", {"start": v(1.3, -11.36) * mm, "end": v(1.33, -11.34) * mm});
            skLineSegment(sketch, "E1573", {"start": v(1.33, -11.34) * mm, "end": v(1.33, -11.27) * mm});
            skLineSegment(sketch, "E1574", {"start": v(1.33, -11.27) * mm, "end": v(1.3, -11.2) * mm});
            skLineSegment(sketch, "E1575", {"start": v(1.3, -11.2) * mm, "end": v(1.2, -11.2) * mm});
            skLineSegment(sketch, "E1576", {"start": v(1.2, -11.2) * mm, "end": v(1.17, -11.15) * mm});
            skLineSegment(sketch, "E1577", {"start": v(1.17, -11.15) * mm, "end": v(1.11, -11.14) * mm});
            skLineSegment(sketch, "E1578", {"start": v(1.11, -11.14) * mm, "end": v(1.07, -11.2) * mm});
            skLineSegment(sketch, "E1579", {"start": v(1.07, -11.2) * mm, "end": v(1.03, -11.2) * mm});
            skLineSegment(sketch, "E1580", {"start": v(1.03, -11.2) * mm, "end": v(1, -11.2) * mm});
            skLineSegment(sketch, "E1581", {"start": v(1, -11.2) * mm, "end": v(0.98, -11.18) * mm});
            skLineSegment(sketch, "E1582", {"start": v(0.98, -11.18) * mm, "end": v(0.91, -11.18) * mm});
            skLineSegment(sketch, "E1583", {"start": v(0.91, -11.18) * mm, "end": v(0.88, -11.18) * mm});
            skLineSegment(sketch, "E1584", {"start": v(0.88, -11.18) * mm, "end": v(0.86, -11.18) * mm});
            skLineSegment(sketch, "E1585", {"start": v(0.86, -11.18) * mm, "end": v(0.88, -11.23) * mm});
            skLineSegment(sketch, "E1586", {"start": v(0.88, -11.23) * mm, "end": v(0.91, -11.25) * mm});
            skLineSegment(sketch, "E1587", {"start": v(0.91, -11.25) * mm, "end": v(0.88, -11.27) * mm});
            skLineSegment(sketch, "E1588", {"start": v(0.88, -11.27) * mm, "end": v(0.84, -11.27) * mm});
            skLineSegment(sketch, "E1589", {"start": v(0.84, -11.27) * mm, "end": v(0.82, -11.25) * mm});
            skLineSegment(sketch, "E1590", {"start": v(0.82, -11.25) * mm, "end": v(0.78, -11.24) * mm});
            skLineSegment(sketch, "E1591", {"start": v(0.78, -11.24) * mm, "end": v(0.76, -11.28) * mm});
            skLineSegment(sketch, "E1592", {"start": v(0.76, -11.28) * mm, "end": v(0.73, -11.3) * mm});
            skLineSegment(sketch, "E1593", {"start": v(0.73, -11.3) * mm, "end": v(0.69, -11.3) * mm});
            skLineSegment(sketch, "E1594", {"start": v(0.69, -11.3) * mm, "end": v(0.66, -11.28) * mm});
            skLineSegment(sketch, "E1595", {"start": v(0.66, -11.28) * mm, "end": v(0.58, -11.28) * mm});
            skLineSegment(sketch, "E1596", {"start": v(0.58, -11.28) * mm, "end": v(0.47, -11.35) * mm});
            skLineSegment(sketch, "E1597", {"start": v(0.47, -11.35) * mm, "end": v(0.33, -11.4) * mm});
            skLineSegment(sketch, "E1598", {"start": v(0.33, -11.4) * mm, "end": v(0.24, -11.47) * mm});
            skLineSegment(sketch, "E1599", {"start": v(0.24, -11.47) * mm, "end": v(0.16, -11.48) * mm});
            skLineSegment(sketch, "E1600", {"start": v(0.16, -11.48) * mm, "end": v(0.09, -11.45) * mm});
            skLineSegment(sketch, "E1601", {"start": v(0.09, -11.45) * mm, "end": v(-0.01, -11.43) * mm});
            skLineSegment(sketch, "E1602", {"start": v(-0.01, -11.43) * mm, "end": v(-0.03, -11.41) * mm});
            skLineSegment(sketch, "E1603", {"start": v(-0.03, -11.41) * mm, "end": v(-0.08, -11.38) * mm});
            skLineSegment(sketch, "E1604", {"start": v(-0.08, -11.38) * mm, "end": v(-0.16, -11.38) * mm});
            skLineSegment(sketch, "E1605", {"start": v(-0.16, -11.38) * mm, "end": v(-0.22, -11.42) * mm});
            skLineSegment(sketch, "E1606", {"start": v(-0.22, -11.42) * mm, "end": v(-0.25, -11.45) * mm});
            skLineSegment(sketch, "E1607", {"start": v(-0.25, -11.45) * mm, "end": v(-0.26, -11.48) * mm});
            skLineSegment(sketch, "E1608", {"start": v(-0.26, -11.48) * mm, "end": v(-0.29, -11.49) * mm});
            skLineSegment(sketch, "E1609", {"start": v(-0.29, -11.49) * mm, "end": v(-0.32, -11.47) * mm});
            skLineSegment(sketch, "E1610", {"start": v(-0.32, -11.47) * mm, "end": v(-0.34, -11.44) * mm});
            skLineSegment(sketch, "E1611", {"start": v(-0.34, -11.44) * mm, "end": v(-0.36, -11.42) * mm});
            skLineSegment(sketch, "E1612", {"start": v(-0.36, -11.42) * mm, "end": v(-0.42, -11.45) * mm});
            skLineSegment(sketch, "E1613", {"start": v(-0.42, -11.45) * mm, "end": v(-0.47, -11.49) * mm});
            skLineSegment(sketch, "E1614", {"start": v(-0.47, -11.49) * mm, "end": v(-0.68, -11.49) * mm});
            skLineSegment(sketch, "E1615", {"start": v(-0.68, -11.49) * mm, "end": v(-0.75, -11.52) * mm});
            skLineSegment(sketch, "E1616", {"start": v(-0.75, -11.52) * mm, "end": v(-0.82, -11.52) * mm});
            skLineSegment(sketch, "E1617", {"start": v(-0.82, -11.52) * mm, "end": v(-0.85, -11.5) * mm});
            skLineSegment(sketch, "E1618", {"start": v(-0.85, -11.5) * mm, "end": v(-0.84, -11.45) * mm});
            skLineSegment(sketch, "E1619", {"start": v(-0.84, -11.45) * mm, "end": v(-0.83, -11.43) * mm});
            skLineSegment(sketch, "E1620", {"start": v(-0.83, -11.43) * mm, "end": v(-0.86, -11.4) * mm});
            skLineSegment(sketch, "E1621", {"start": v(-0.86, -11.4) * mm, "end": v(-0.9, -11.4) * mm});
            skLineSegment(sketch, "E1622", {"start": v(-0.9, -11.4) * mm, "end": v(-0.92, -11.4) * mm});
            skLineSegment(sketch, "E1623", {"start": v(-0.92, -11.4) * mm, "end": v(-0.92, -11.45) * mm});
            skLineSegment(sketch, "E1624", {"start": v(-0.92, -11.45) * mm, "end": v(-0.94, -11.49) * mm});
            skLineSegment(sketch, "E1625", {"start": v(-0.94, -11.49) * mm, "end": v(-0.98, -11.52) * mm});
            skLineSegment(sketch, "E1626", {"start": v(-0.98, -11.52) * mm, "end": v(-1.02, -11.56) * mm});
            skLineSegment(sketch, "E1627", {"start": v(-1.02, -11.56) * mm, "end": v(-1.06, -11.6) * mm});
            skLineSegment(sketch, "E1628", {"start": v(-1.06, -11.6) * mm, "end": v(-1.08, -11.64) * mm});
            skLineSegment(sketch, "E1629", {"start": v(-1.08, -11.64) * mm, "end": v(-1.1, -11.73) * mm});
            skLineSegment(sketch, "E1630", {"start": v(-1.1, -11.73) * mm, "end": v(-1.02, -11.8) * mm});
            skLineSegment(sketch, "E1631", {"start": v(-1.02, -11.8) * mm, "end": v(-1, -11.82) * mm});
            skLineSegment(sketch, "E1632", {"start": v(-1, -11.82) * mm, "end": v(-1, -11.85) * mm});
            skLineSegment(sketch, "E1633", {"start": v(-1, -11.85) * mm, "end": v(-1.01, -11.88) * mm});
            skLineSegment(sketch, "E1634", {"start": v(-1.01, -11.88) * mm, "end": v(-1.06, -11.88) * mm});
            skLineSegment(sketch, "E1635", {"start": v(-1.06, -11.88) * mm, "end": v(-1.1, -11.88) * mm});
            skLineSegment(sketch, "E1636", {"start": v(-1.1, -11.88) * mm, "end": v(-1.14, -11.85) * mm});
            skLineSegment(sketch, "E1637", {"start": v(-1.14, -11.85) * mm, "end": v(-1.18, -11.82) * mm});
            skLineSegment(sketch, "E1638", {"start": v(-1.18, -11.82) * mm, "end": v(-1.22, -11.77) * mm});
            skLineSegment(sketch, "E1639", {"start": v(-1.22, -11.77) * mm, "end": v(-1.25, -11.74) * mm});
            skLineSegment(sketch, "E1640", {"start": v(-1.25, -11.74) * mm, "end": v(-1.28, -11.72) * mm});
            skLineSegment(sketch, "E1641", {"start": v(-1.28, -11.72) * mm, "end": v(-1.28, -11.66) * mm});
            skLineSegment(sketch, "E1642", {"start": v(-1.28, -11.66) * mm, "end": v(-1.24, -11.64) * mm});
            skLineSegment(sketch, "E1643", {"start": v(-1.24, -11.64) * mm, "end": v(-1.2, -11.63) * mm});
            skLineSegment(sketch, "E1644", {"start": v(-1.2, -11.63) * mm, "end": v(-1.2, -11.6) * mm});
            skLineSegment(sketch, "E1645", {"start": v(-1.2, -11.6) * mm, "end": v(-1.26, -11.6) * mm});
            skLineSegment(sketch, "E1646", {"start": v(-1.26, -11.6) * mm, "end": v(-1.3, -11.56) * mm});
            skLineSegment(sketch, "E1647", {"start": v(-1.3, -11.56) * mm, "end": v(-1.3, -11.54) * mm});
            skLineSegment(sketch, "E1648", {"start": v(-1.3, -11.54) * mm, "end": v(-1.33, -11.53) * mm});
            skLineSegment(sketch, "E1649", {"start": v(-1.33, -11.53) * mm, "end": v(-1.33, -11.57) * mm});
            skLineSegment(sketch, "E1650", {"start": v(-1.33, -11.57) * mm, "end": v(-1.34, -11.62) * mm});
            skLineSegment(sketch, "E1651", {"start": v(-1.34, -11.62) * mm, "end": v(-1.37, -11.6) * mm});
            skLineSegment(sketch, "E1652", {"start": v(-1.37, -11.6) * mm, "end": v(-1.4, -11.57) * mm});
            skLineSegment(sketch, "E1653", {"start": v(-1.4, -11.57) * mm, "end": v(-1.4, -11.54) * mm});
            skLineSegment(sketch, "E1654", {"start": v(-1.4, -11.54) * mm, "end": v(-1.42, -11.54) * mm});
            skLineSegment(sketch, "E1655", {"start": v(-1.42, -11.54) * mm, "end": v(-1.43, -11.56) * mm});
            skLineSegment(sketch, "E1656", {"start": v(-1.43, -11.56) * mm, "end": v(-1.55, -11.57) * mm});
            skLineSegment(sketch, "E1657", {"start": v(-1.55, -11.57) * mm, "end": v(-1.58, -11.6) * mm});
            skLineSegment(sketch, "E1658", {"start": v(-1.58, -11.6) * mm, "end": v(-1.62, -11.6) * mm});
            skLineSegment(sketch, "E1659", {"start": v(-1.62, -11.6) * mm, "end": v(-1.68, -11.68) * mm});
            skLineSegment(sketch, "E1660", {"start": v(-1.68, -11.68) * mm, "end": v(-1.69, -11.7) * mm});
            skLineSegment(sketch, "E1661", {"start": v(-1.69, -11.7) * mm, "end": v(-1.72, -11.71) * mm});
            skLineSegment(sketch, "E1662", {"start": v(-1.72, -11.71) * mm, "end": v(-1.74, -11.69) * mm});
            skLineSegment(sketch, "E1663", {"start": v(-1.74, -11.69) * mm, "end": v(-1.78, -11.63) * mm});
            skLineSegment(sketch, "E1664", {"start": v(-1.78, -11.63) * mm, "end": v(-1.8, -11.58) * mm});
            skLineSegment(sketch, "E1665", {"start": v(-1.8, -11.58) * mm, "end": v(-1.95, -11.58) * mm});
            skLineSegment(sketch, "E1666", {"start": v(-1.95, -11.58) * mm, "end": v(-2.04, -11.62) * mm});
            skLineSegment(sketch, "E1667", {"start": v(-2.04, -11.62) * mm, "end": v(-2.08, -11.66) * mm});
            skLineSegment(sketch, "E1668", {"start": v(-2.08, -11.66) * mm, "end": v(-2.1, -11.73) * mm});
            skLineSegment(sketch, "E1669", {"start": v(-2.1, -11.73) * mm, "end": v(-2.12, -11.76) * mm});
            skLineSegment(sketch, "E1670", {"start": v(-2.12, -11.76) * mm, "end": v(-2.17, -11.78) * mm});
            skLineSegment(sketch, "E1671", {"start": v(-2.17, -11.78) * mm, "end": v(-2.2, -11.76) * mm});
            skLineSegment(sketch, "E1672", {"start": v(-2.2, -11.76) * mm, "end": v(-2.2, -11.68) * mm});
            skLineSegment(sketch, "E1673", {"start": v(-2.2, -11.68) * mm, "end": v(-2.27, -11.62) * mm});
            skLineSegment(sketch, "E1674", {"start": v(-2.27, -11.62) * mm, "end": v(-2.3, -11.58) * mm});
            skLineSegment(sketch, "E1675", {"start": v(-2.3, -11.58) * mm, "end": v(-2.32, -11.47) * mm});
            skLineSegment(sketch, "E1676", {"start": v(-2.32, -11.47) * mm, "end": v(-2.3, -11.41) * mm});
            skLineSegment(sketch, "E1677", {"start": v(-2.3, -11.41) * mm, "end": v(-2.27, -11.37) * mm});
            skLineSegment(sketch, "E1678", {"start": v(-2.27, -11.37) * mm, "end": v(-2.26, -11.37) * mm});
            skLineSegment(sketch, "E1679", {"start": v(-2.26, -11.37) * mm, "end": v(-2.26, -11.34) * mm});
            skLineSegment(sketch, "E1680", {"start": v(-2.26, -11.34) * mm, "end": v(-2.3, -11.32) * mm});
            skLineSegment(sketch, "E1681", {"start": v(-2.3, -11.32) * mm, "end": v(-2.32, -11.32) * mm});
            skLineSegment(sketch, "E1682", {"start": v(-2.32, -11.32) * mm, "end": v(-2.37, -11.34) * mm});
            skLineSegment(sketch, "E1683", {"start": v(-2.37, -11.34) * mm, "end": v(-2.42, -11.34) * mm});
            skLineSegment(sketch, "E1684", {"start": v(-2.42, -11.34) * mm, "end": v(-2.47, -11.43) * mm});
            skLineSegment(sketch, "E1685", {"start": v(-2.47, -11.43) * mm, "end": v(-2.54, -11.5) * mm});
            skLineSegment(sketch, "E1686", {"start": v(-2.54, -11.5) * mm, "end": v(-2.59, -11.5) * mm});
            skLineSegment(sketch, "E1687", {"start": v(-2.59, -11.5) * mm, "end": v(-2.62, -11.48) * mm});
            skLineSegment(sketch, "E1688", {"start": v(-2.62, -11.48) * mm, "end": v(-2.63, -11.42) * mm});
            skLineSegment(sketch, "E1689", {"start": v(-2.63, -11.42) * mm, "end": v(-2.68, -11.38) * mm});
            skLineSegment(sketch, "E1690", {"start": v(-2.68, -11.38) * mm, "end": v(-2.75, -11.4) * mm});
            skLineSegment(sketch, "E1691", {"start": v(-2.75, -11.4) * mm, "end": v(-2.82, -11.4) * mm});
            skLineSegment(sketch, "E1692", {"start": v(-2.82, -11.4) * mm, "end": v(-2.86, -11.36) * mm});
            skLineSegment(sketch, "E1693", {"start": v(-2.86, -11.36) * mm, "end": v(-2.86, -11.3) * mm});
            skLineSegment(sketch, "E1694", {"start": v(-2.86, -11.3) * mm, "end": v(-2.83, -11.28) * mm});
            skLineSegment(sketch, "E1695", {"start": v(-2.83, -11.28) * mm, "end": v(-2.76, -11.28) * mm});
            skLineSegment(sketch, "E1696", {"start": v(-2.76, -11.28) * mm, "end": v(-2.7, -11.33) * mm});
            skLineSegment(sketch, "E1697", {"start": v(-2.7, -11.33) * mm, "end": v(-2.65, -11.34) * mm});
            skLineSegment(sketch, "E1698", {"start": v(-2.65, -11.34) * mm, "end": v(-2.62, -11.36) * mm});
            skLineSegment(sketch, "E1699", {"start": v(-2.62, -11.36) * mm, "end": v(-2.57, -11.33) * mm});
            skLineSegment(sketch, "E1700", {"start": v(-2.57, -11.33) * mm, "end": v(-2.53, -11.3) * mm});
            skLineSegment(sketch, "E1701", {"start": v(-2.53, -11.3) * mm, "end": v(-2.53, -11.26) * mm});
            skLineSegment(sketch, "E1702", {"start": v(-2.53, -11.26) * mm, "end": v(-2.55, -11.24) * mm});
            skLineSegment(sketch, "E1703", {"start": v(-2.55, -11.24) * mm, "end": v(-2.58, -11.22) * mm});
            skLineSegment(sketch, "E1704", {"start": v(-2.58, -11.22) * mm, "end": v(-2.63, -11.2) * mm});
            skLineSegment(sketch, "E1705", {"start": v(-2.63, -11.2) * mm, "end": v(-2.67, -11.19) * mm});
            skLineSegment(sketch, "E1706", {"start": v(-2.67, -11.19) * mm, "end": v(-2.65, -11.17) * mm});
            skLineSegment(sketch, "E1707", {"start": v(-2.65, -11.17) * mm, "end": v(-2.62, -11.14) * mm});
            skLineSegment(sketch, "E1708", {"start": v(-2.62, -11.14) * mm, "end": v(-2.54, -11.04) * mm});
            skLineSegment(sketch, "E1709", {"start": v(-2.54, -11.04) * mm, "end": v(-2.44, -10.95) * mm});
            skLineSegment(sketch, "E1710", {"start": v(-2.44, -10.95) * mm, "end": v(-2.25, -10.84) * mm});
            skLineSegment(sketch, "E1711", {"start": v(-2.25, -10.84) * mm, "end": v(-2.1, -10.7) * mm});
            skLineSegment(sketch, "E1712", {"start": v(-2.1, -10.7) * mm, "end": v(-1.93, -10.6) * mm});
            skLineSegment(sketch, "E1713", {"start": v(-1.93, -10.6) * mm, "end": v(-1.87, -10.51) * mm});
            skLineSegment(sketch, "E1714", {"start": v(-1.87, -10.51) * mm, "end": v(-1.75, -10.44) * mm});
            skLineSegment(sketch, "E1715", {"start": v(-1.75, -10.44) * mm, "end": v(-1.7, -10.4) * mm});
            skLineSegment(sketch, "E1716", {"start": v(-1.7, -10.4) * mm, "end": v(-1.7, -10.34) * mm});
            skLineSegment(sketch, "E1717", {"start": v(-1.7, -10.34) * mm, "end": v(-1.72, -10.32) * mm});
            skLineSegment(sketch, "E1718", {"start": v(-1.72, -10.32) * mm, "end": v(-1.7, -10.3) * mm});
            skLineSegment(sketch, "E1719", {"start": v(-1.7, -10.3) * mm, "end": v(-1.66, -10.3) * mm});
            skLineSegment(sketch, "E1720", {"start": v(-1.66, -10.3) * mm, "end": v(-1.67, -10.27) * mm});
            skLineSegment(sketch, "E1721", {"start": v(-1.67, -10.27) * mm, "end": v(-1.7, -10.27) * mm});
            skLineSegment(sketch, "E1722", {"start": v(-1.7, -10.27) * mm, "end": v(-1.7, -10.23) * mm});
            skLineSegment(sketch, "E1723", {"start": v(-1.7, -10.23) * mm, "end": v(-1.71, -10.22) * mm});
            skLineSegment(sketch, "E1724", {"start": v(-1.71, -10.22) * mm, "end": v(-1.74, -10.22) * mm});
            skLineSegment(sketch, "E1725", {"start": v(-1.74, -10.22) * mm, "end": v(-1.75, -10.24) * mm});
            skLineSegment(sketch, "E1726", {"start": v(-1.75, -10.24) * mm, "end": v(-1.78, -10.24) * mm});
            skLineSegment(sketch, "E1727", {"start": v(-1.78, -10.24) * mm, "end": v(-1.8, -10.21) * mm});
            skLineSegment(sketch, "E1728", {"start": v(-1.8, -10.21) * mm, "end": v(-1.83, -10.18) * mm});
            skLineSegment(sketch, "E1729", {"start": v(-1.83, -10.18) * mm, "end": v(-1.88, -10.18) * mm});
            skLineSegment(sketch, "E1730", {"start": v(-1.88, -10.18) * mm, "end": v(-1.9, -10.23) * mm});
            skLineSegment(sketch, "E1731", {"start": v(-1.9, -10.23) * mm, "end": v(-1.96, -10.3) * mm});
            skLineSegment(sketch, "E1732", {"start": v(-1.96, -10.3) * mm, "end": v(-2.07, -10.36) * mm});
            skLineSegment(sketch, "E1733", {"start": v(-2.07, -10.36) * mm, "end": v(-2.14, -10.37) * mm});
            skLineSegment(sketch, "E1734", {"start": v(-2.14, -10.37) * mm, "end": v(-2.16, -10.34) * mm});
            skLineSegment(sketch, "E1735", {"start": v(-2.16, -10.34) * mm, "end": v(-2.21, -10.34) * mm});
            skLineSegment(sketch, "E1736", {"start": v(-2.21, -10.34) * mm, "end": v(-2.23, -10.38) * mm});
            skLineSegment(sketch, "E1737", {"start": v(-2.23, -10.38) * mm, "end": v(-2.31, -10.37) * mm});
            skLineSegment(sketch, "E1738", {"start": v(-2.31, -10.37) * mm, "end": v(-2.33, -10.33) * mm});
            skLineSegment(sketch, "E1739", {"start": v(-2.33, -10.33) * mm, "end": v(-2.37, -10.34) * mm});
            skLineSegment(sketch, "E1740", {"start": v(-2.37, -10.34) * mm, "end": v(-2.39, -10.37) * mm});
            skLineSegment(sketch, "E1741", {"start": v(-2.39, -10.37) * mm, "end": v(-2.4, -10.44) * mm});
            skLineSegment(sketch, "E1742", {"start": v(-2.4, -10.44) * mm, "end": v(-2.42, -10.44) * mm});
            skLineSegment(sketch, "E1743", {"start": v(-2.42, -10.44) * mm, "end": v(-2.44, -10.4) * mm});
            skLineSegment(sketch, "E1744", {"start": v(-2.44, -10.4) * mm, "end": v(-2.42, -10.34) * mm});
            skLineSegment(sketch, "E1745", {"start": v(-2.42, -10.34) * mm, "end": v(-2.42, -10.28) * mm});
            skLineSegment(sketch, "E1746", {"start": v(-2.42, -10.28) * mm, "end": v(-2.46, -10.27) * mm});
            skLineSegment(sketch, "E1747", {"start": v(-2.46, -10.27) * mm, "end": v(-2.54, -10.32) * mm});
            skLineSegment(sketch, "E1748", {"start": v(-2.54, -10.32) * mm, "end": v(-2.6, -10.32) * mm});
            skLineSegment(sketch, "E1749", {"start": v(-2.6, -10.32) * mm, "end": v(-2.64, -10.28) * mm});
            skLineSegment(sketch, "E1750", {"start": v(-2.64, -10.28) * mm, "end": v(-2.66, -10.22) * mm});
            skLineSegment(sketch, "E1751", {"start": v(-2.66, -10.22) * mm, "end": v(-2.66, -10.19) * mm});
            skLineSegment(sketch, "E1752", {"start": v(-2.66, -10.19) * mm, "end": v(-2.73, -10.15) * mm});
            skLineSegment(sketch, "E1753", {"start": v(-2.73, -10.15) * mm, "end": v(-2.77, -10.13) * mm});
            skLineSegment(sketch, "E1754", {"start": v(-2.77, -10.13) * mm, "end": v(-2.8, -10.1) * mm});
            skLineSegment(sketch, "E1755", {"start": v(-2.8, -10.1) * mm, "end": v(-2.8, -10.05) * mm});
            skLineSegment(sketch, "E1756", {"start": v(-2.8, -10.05) * mm, "end": v(-2.76, -10.01) * mm});
            skLineSegment(sketch, "E1757", {"start": v(-2.76, -10.01) * mm, "end": v(-2.73, -10) * mm});
            skLineSegment(sketch, "E1758", {"start": v(-2.73, -10) * mm, "end": v(-2.72, -9.92) * mm});
            skLineSegment(sketch, "E1759", {"start": v(-2.72, -9.92) * mm, "end": v(-2.7, -9.9) * mm});
            skLineSegment(sketch, "E1760", {"start": v(-2.7, -9.9) * mm, "end": v(-2.7, -9.84) * mm});
            skLineSegment(sketch, "E1761", {"start": v(-2.7, -9.84) * mm, "end": v(-2.75, -9.8) * mm});
            skLineSegment(sketch, "E1762", {"start": v(-2.75, -9.8) * mm, "end": v(-2.78, -9.77) * mm});
            skLineSegment(sketch, "E1763", {"start": v(-2.78, -9.77) * mm, "end": v(-2.8, -9.69) * mm});
            skLineSegment(sketch, "E1764", {"start": v(-2.8, -9.69) * mm, "end": v(-2.83, -9.66) * mm});
            skLineSegment(sketch, "E1765", {"start": v(-2.83, -9.66) * mm, "end": v(-2.87, -9.63) * mm});
            skLineSegment(sketch, "E1766", {"start": v(-2.87, -9.63) * mm, "end": v(-2.86, -9.6) * mm});
            skLineSegment(sketch, "E1767", {"start": v(-2.86, -9.6) * mm, "end": v(-2.84, -9.57) * mm});
            skLineSegment(sketch, "E1768", {"start": v(-2.84, -9.57) * mm, "end": v(-2.81, -9.56) * mm});
            skLineSegment(sketch, "E1769", {"start": v(-2.81, -9.56) * mm, "end": v(-2.78, -9.57) * mm});
            skLineSegment(sketch, "E1770", {"start": v(-2.78, -9.57) * mm, "end": v(-2.73, -9.61) * mm});
            skLineSegment(sketch, "E1771", {"start": v(-2.73, -9.61) * mm, "end": v(-2.71, -9.64) * mm});
            skLineSegment(sketch, "E1772", {"start": v(-2.71, -9.64) * mm, "end": v(-2.66, -9.64) * mm});
            skLineSegment(sketch, "E1773", {"start": v(-2.66, -9.64) * mm, "end": v(-2.66, -9.6) * mm});
            skLineSegment(sketch, "E1774", {"start": v(-2.66, -9.6) * mm, "end": v(-2.66, -9.55) * mm});
            skLineSegment(sketch, "E1775", {"start": v(-2.66, -9.55) * mm, "end": v(-2.71, -9.5) * mm});
            skLineSegment(sketch, "E1776", {"start": v(-2.71, -9.5) * mm, "end": v(-2.74, -9.43) * mm});
            skLineSegment(sketch, "E1777", {"start": v(-2.74, -9.43) * mm, "end": v(-2.8, -9.38) * mm});
            skLineSegment(sketch, "E1778", {"start": v(-2.8, -9.38) * mm, "end": v(-2.85, -9.38) * mm});
            skLineSegment(sketch, "E1779", {"start": v(-2.85, -9.38) * mm, "end": v(-2.88, -9.42) * mm});
            skLineSegment(sketch, "E1780", {"start": v(-2.88, -9.42) * mm, "end": v(-2.9, -9.47) * mm});
            skLineSegment(sketch, "E1781", {"start": v(-2.9, -9.47) * mm, "end": v(-2.92, -9.5) * mm});
            skLineSegment(sketch, "E1782", {"start": v(-2.92, -9.5) * mm, "end": v(-2.96, -9.48) * mm});
            skLineSegment(sketch, "E1783", {"start": v(-2.96, -9.48) * mm, "end": v(-2.96, -9.45) * mm});
            skLineSegment(sketch, "E1784", {"start": v(-2.96, -9.45) * mm, "end": v(-3.01, -9.44) * mm});
            skLineSegment(sketch, "E1785", {"start": v(-3.01, -9.44) * mm, "end": v(-3.03, -9.47) * mm});
            skLineSegment(sketch, "E1786", {"start": v(-3.03, -9.47) * mm, "end": v(-3.08, -9.48) * mm});
            skLineSegment(sketch, "E1787", {"start": v(-3.08, -9.48) * mm, "end": v(-3.11, -9.52) * mm});
            skLineSegment(sketch, "E1788", {"start": v(-3.11, -9.52) * mm, "end": v(-3.12, -9.57) * mm});
            skLineSegment(sketch, "E1789", {"start": v(-3.12, -9.57) * mm, "end": v(-3.15, -9.6) * mm});
            skLineSegment(sketch, "E1790", {"start": v(-3.15, -9.6) * mm, "end": v(-3.18, -9.56) * mm});
            skLineSegment(sketch, "E1791", {"start": v(-3.18, -9.56) * mm, "end": v(-3.18, -9.51) * mm});
            skLineSegment(sketch, "E1792", {"start": v(-3.18, -9.51) * mm, "end": v(-3.16, -9.49) * mm});
            skLineSegment(sketch, "E1793", {"start": v(-3.16, -9.49) * mm, "end": v(-3.17, -9.46) * mm});
            skLineSegment(sketch, "E1794", {"start": v(-3.17, -9.46) * mm, "end": v(-3.21, -9.42) * mm});
            skLineSegment(sketch, "E1795", {"start": v(-3.21, -9.42) * mm, "end": v(-3.24, -9.35) * mm});
            skLineSegment(sketch, "E1796", {"start": v(-3.24, -9.35) * mm, "end": v(-3.27, -9.32) * mm});
            skLineSegment(sketch, "E1797", {"start": v(-3.27, -9.32) * mm, "end": v(-3.29, -9.38) * mm});
            skLineSegment(sketch, "E1798", {"start": v(-3.29, -9.38) * mm, "end": v(-3.27, -9.43) * mm});
            skLineSegment(sketch, "E1799", {"start": v(-3.27, -9.43) * mm, "end": v(-3.28, -9.47) * mm});
            skLineSegment(sketch, "E1800", {"start": v(-3.28, -9.47) * mm, "end": v(-3.32, -9.47) * mm});
            skLineSegment(sketch, "E1801", {"start": v(-3.32, -9.47) * mm, "end": v(-3.34, -9.44) * mm});
            skLineSegment(sketch, "E1802", {"start": v(-3.34, -9.44) * mm, "end": v(-3.32, -9.4) * mm});
            skLineSegment(sketch, "E1803", {"start": v(-3.32, -9.4) * mm, "end": v(-3.33, -9.35) * mm});
            skLineSegment(sketch, "E1804", {"start": v(-3.33, -9.35) * mm, "end": v(-3.37, -9.3) * mm});
            skLineSegment(sketch, "E1805", {"start": v(-3.37, -9.3) * mm, "end": v(-3.4, -9.28) * mm});
            skLineSegment(sketch, "E1806", {"start": v(-3.4, -9.28) * mm, "end": v(-3.45, -9.28) * mm});
            skLineSegment(sketch, "E1807", {"start": v(-3.45, -9.28) * mm, "end": v(-3.46, -9.34) * mm});
            skLineSegment(sketch, "E1808", {"start": v(-3.46, -9.34) * mm, "end": v(-3.4, -9.4) * mm});
            skLineSegment(sketch, "E1809", {"start": v(-3.4, -9.4) * mm, "end": v(-3.35, -9.48) * mm});
            skLineSegment(sketch, "E1810", {"start": v(-3.35, -9.48) * mm, "end": v(-3.3, -9.54) * mm});
            skLineSegment(sketch, "E1811", {"start": v(-3.3, -9.54) * mm, "end": v(-3.3, -9.57) * mm});
            skLineSegment(sketch, "E1812", {"start": v(-3.3, -9.57) * mm, "end": v(-3.37, -9.57) * mm});
            skLineSegment(sketch, "E1813", {"start": v(-3.37, -9.57) * mm, "end": v(-3.45, -9.51) * mm});
            skLineSegment(sketch, "E1814", {"start": v(-3.45, -9.51) * mm, "end": v(-3.53, -9.47) * mm});
            skLineSegment(sketch, "E1815", {"start": v(-3.53, -9.47) * mm, "end": v(-3.61, -9.42) * mm});
            skLineSegment(sketch, "E1816", {"start": v(-3.61, -9.42) * mm, "end": v(-3.67, -9.4) * mm});
            skLineSegment(sketch, "E1817", {"start": v(-3.67, -9.4) * mm, "end": v(-3.72, -9.42) * mm});
            skLineSegment(sketch, "E1818", {"start": v(-3.72, -9.42) * mm, "end": v(-3.69, -9.45) * mm});
            skLineSegment(sketch, "E1819", {"start": v(-3.69, -9.45) * mm, "end": v(-3.69, -9.5) * mm});
            skLineSegment(sketch, "E1820", {"start": v(-3.69, -9.5) * mm, "end": v(-3.72, -9.53) * mm});
            skLineSegment(sketch, "E1821", {"start": v(-3.72, -9.53) * mm, "end": v(-3.76, -9.53) * mm});
            skLineSegment(sketch, "E1822", {"start": v(-3.76, -9.53) * mm, "end": v(-3.8, -9.5) * mm});
            skLineSegment(sketch, "E1823", {"start": v(-3.8, -9.5) * mm, "end": v(-3.8, -9.36) * mm});
            skLineSegment(sketch, "E1824", {"start": v(-3.8, -9.36) * mm, "end": v(-3.83, -9.31) * mm});
            skLineSegment(sketch, "E1825", {"start": v(-3.83, -9.31) * mm, "end": v(-3.9, -9.3) * mm});
            skLineSegment(sketch, "E1826", {"start": v(-3.9, -9.3) * mm, "end": v(-4.1, -9.12) * mm});
            skLineSegment(sketch, "E1827", {"start": v(-4.1, -9.12) * mm, "end": v(-4.16, -9.08) * mm});
            skLineSegment(sketch, "E1828", {"start": v(-4.16, -9.08) * mm, "end": v(-4.24, -9.06) * mm});
            skLineSegment(sketch, "E1829", {"start": v(-4.24, -9.06) * mm, "end": v(-4.29, -9.03) * mm});
            skLineSegment(sketch, "E1830", {"start": v(-4.29, -9.03) * mm, "end": v(-4.3, -8.96) * mm});
            skLineSegment(sketch, "E1831", {"start": v(-4.3, -8.96) * mm, "end": v(-4.26, -8.93) * mm});
            skLineSegment(sketch, "E1832", {"start": v(-4.26, -8.93) * mm, "end": v(-4.27, -8.88) * mm});
            skLineSegment(sketch, "E1833", {"start": v(-4.27, -8.88) * mm, "end": v(-4.3, -8.85) * mm});
            skLineSegment(sketch, "E1834", {"start": v(-4.3, -8.85) * mm, "end": v(-4.37, -8.83) * mm});
            skLineSegment(sketch, "E1835", {"start": v(-4.37, -8.83) * mm, "end": v(-4.67, -8.58) * mm});
            skLineSegment(sketch, "E1836", {"start": v(-4.67, -8.58) * mm, "end": v(-4.85, -8.48) * mm});
            skLineSegment(sketch, "E1837", {"start": v(-4.85, -8.48) * mm, "end": v(-5.03, -8.32) * mm});
            skLineSegment(sketch, "E1838", {"start": v(-5.03, -8.32) * mm, "end": v(-5.03, -8.28) * mm});
            skLineSegment(sketch, "E1839", {"start": v(-5.03, -8.28) * mm, "end": v(-4.98, -8.28) * mm});
            skLineSegment(sketch, "E1840", {"start": v(-4.98, -8.28) * mm, "end": v(-4.79, -8.44) * mm});
            skLineSegment(sketch, "E1841", {"start": v(-4.79, -8.44) * mm, "end": v(-4.63, -8.51) * mm});
            skLineSegment(sketch, "E1842", {"start": v(-4.63, -8.51) * mm, "end": v(-4.39, -8.72) * mm});
            skLineSegment(sketch, "E1843", {"start": v(-4.39, -8.72) * mm, "end": v(-4.35, -8.75) * mm});
            skLineSegment(sketch, "E1844", {"start": v(-4.35, -8.75) * mm, "end": v(-4.32, -8.75) * mm});
            skLineSegment(sketch, "E1845", {"start": v(-4.32, -8.75) * mm, "end": v(-4.32, -8.7) * mm});
            skLineSegment(sketch, "E1846", {"start": v(-4.32, -8.7) * mm, "end": v(-4.33, -8.65) * mm});
            skLineSegment(sketch, "E1847", {"start": v(-4.33, -8.65) * mm, "end": v(-4.37, -8.62) * mm});
            skLineSegment(sketch, "E1848", {"start": v(-4.37, -8.62) * mm, "end": v(-4.42, -8.6) * mm});
            skLineSegment(sketch, "E1849", {"start": v(-4.42, -8.6) * mm, "end": v(-4.43, -8.55) * mm});
            skLineSegment(sketch, "E1850", {"start": v(-4.43, -8.55) * mm, "end": v(-4.38, -8.53) * mm});
            skLineSegment(sketch, "E1851", {"start": v(-4.38, -8.53) * mm, "end": v(-4.35, -8.53) * mm});
            skLineSegment(sketch, "E1852", {"start": v(-4.35, -8.53) * mm, "end": v(-4.33, -8.51) * mm});
            skLineSegment(sketch, "E1853", {"start": v(-4.33, -8.51) * mm, "end": v(-4.34, -8.42) * mm});
            skLineSegment(sketch, "E1854", {"start": v(-4.34, -8.42) * mm, "end": v(-4.37, -8.35) * mm});
            skLineSegment(sketch, "E1855", {"start": v(-4.37, -8.35) * mm, "end": v(-4.44, -8.28) * mm});
            skLineSegment(sketch, "E1856", {"start": v(-4.44, -8.28) * mm, "end": v(-4.5, -8.23) * mm});
            skLineSegment(sketch, "E1857", {"start": v(-4.5, -8.23) * mm, "end": v(-4.59, -8.14) * mm});
            skLineSegment(sketch, "E1858", {"start": v(-4.59, -8.14) * mm, "end": v(-4.63, -8.09) * mm});
            skLineSegment(sketch, "E1859", {"start": v(-4.63, -8.09) * mm, "end": v(-4.66, -8.07) * mm});
            skLineSegment(sketch, "E1860", {"start": v(-4.66, -8.07) * mm, "end": v(-4.72, -8.08) * mm});
            skLineSegment(sketch, "E1861", {"start": v(-4.72, -8.08) * mm, "end": v(-4.72, -8.14) * mm});
            skLineSegment(sketch, "E1862", {"start": v(-4.72, -8.14) * mm, "end": v(-4.64, -8.2) * mm});
            skLineSegment(sketch, "E1863", {"start": v(-4.64, -8.2) * mm, "end": v(-4.56, -8.28) * mm});
            skLineSegment(sketch, "E1864", {"start": v(-4.56, -8.28) * mm, "end": v(-4.5, -8.35) * mm});
            skLineSegment(sketch, "E1865", {"start": v(-4.5, -8.35) * mm, "end": v(-4.46, -8.42) * mm});
            skLineSegment(sketch, "E1866", {"start": v(-4.46, -8.42) * mm, "end": v(-4.45, -8.47) * mm});
            skLineSegment(sketch, "E1867", {"start": v(-4.45, -8.47) * mm, "end": v(-4.45, -8.51) * mm});
            skLineSegment(sketch, "E1868", {"start": v(-4.45, -8.51) * mm, "end": v(-4.49, -8.52) * mm});
            skLineSegment(sketch, "E1869", {"start": v(-4.49, -8.52) * mm, "end": v(-4.5, -8.47) * mm});
            skLineSegment(sketch, "E1870", {"start": v(-4.5, -8.47) * mm, "end": v(-4.56, -8.4) * mm});
            skLineSegment(sketch, "E1871", {"start": v(-4.56, -8.4) * mm, "end": v(-4.64, -8.32) * mm});
            skLineSegment(sketch, "E1872", {"start": v(-4.64, -8.32) * mm, "end": v(-4.72, -8.26) * mm});
            skLineSegment(sketch, "E1873", {"start": v(-4.72, -8.26) * mm, "end": v(-4.77, -8.22) * mm});
            skLineSegment(sketch, "E1874", {"start": v(-4.77, -8.22) * mm, "end": v(-4.84, -8.18) * mm});
            skLineSegment(sketch, "E1875", {"start": v(-4.84, -8.18) * mm, "end": v(-4.9, -8.14) * mm});
            skLineSegment(sketch, "E1876", {"start": v(-4.9, -8.14) * mm, "end": v(-4.94, -8.12) * mm});
            skLineSegment(sketch, "E1877", {"start": v(-4.94, -8.12) * mm, "end": v(-4.94, -8.08) * mm});
            skLineSegment(sketch, "E1878", {"start": v(-4.94, -8.08) * mm, "end": v(-4.9, -8.07) * mm});
            skLineSegment(sketch, "E1879", {"start": v(-4.9, -8.07) * mm, "end": v(-4.89, -8.1) * mm});
            skLineSegment(sketch, "E1880", {"start": v(-4.89, -8.1) * mm, "end": v(-4.86, -8.1) * mm});
            skLineSegment(sketch, "E1881", {"start": v(-4.86, -8.1) * mm, "end": v(-4.84, -8.1) * mm});
            skLineSegment(sketch, "E1882", {"start": v(-4.84, -8.1) * mm, "end": v(-4.8, -8.08) * mm});
            skLineSegment(sketch, "E1883", {"start": v(-4.8, -8.08) * mm, "end": v(-4.78, -8.01) * mm});
            skLineSegment(sketch, "E1884", {"start": v(-4.78, -8.01) * mm, "end": v(-4.8, -7.96) * mm});
            skLineSegment(sketch, "E1885", {"start": v(-4.8, -7.96) * mm, "end": v(-4.82, -7.94) * mm});
            skLineSegment(sketch, "E1886", {"start": v(-4.82, -7.94) * mm, "end": v(-4.86, -7.94) * mm});
            skLineSegment(sketch, "E1887", {"start": v(-4.86, -7.94) * mm, "end": v(-4.89, -7.97) * mm});
            skLineSegment(sketch, "E1888", {"start": v(-4.89, -7.97) * mm, "end": v(-4.9, -8.02) * mm});
            skLineSegment(sketch, "E1889", {"start": v(-4.9, -8.02) * mm, "end": v(-4.9, -8.04) * mm});
            skLineSegment(sketch, "E1890", {"start": v(-4.9, -8.04) * mm, "end": v(-4.92, -8.04) * mm});
            skLineSegment(sketch, "E1891", {"start": v(-4.92, -8.04) * mm, "end": v(-4.93, -8.02) * mm});
            skLineSegment(sketch, "E1892", {"start": v(-4.93, -8.02) * mm, "end": v(-4.96, -8) * mm});
            skLineSegment(sketch, "E1893", {"start": v(-4.96, -8) * mm, "end": v(-5, -7.99) * mm});
            skLineSegment(sketch, "E1894", {"start": v(-5, -7.99) * mm, "end": v(-5.08, -7.88) * mm});
            skLineSegment(sketch, "E1895", {"start": v(-5.08, -7.88) * mm, "end": v(-5.14, -7.77) * mm});
            skLineSegment(sketch, "E1896", {"start": v(-5.14, -7.77) * mm, "end": v(-5.17, -7.72) * mm});
            skLineSegment(sketch, "E1897", {"start": v(-5.17, -7.72) * mm, "end": v(-5.25, -7.66) * mm});
            skLineSegment(sketch, "E1898", {"start": v(-5.25, -7.66) * mm, "end": v(-5.31, -7.6) * mm});
            skLineSegment(sketch, "E1899", {"start": v(-5.31, -7.6) * mm, "end": v(-5.34, -7.54) * mm});
            skLineSegment(sketch, "E1900", {"start": v(-5.34, -7.54) * mm, "end": v(-5.38, -7.51) * mm});
            skLineSegment(sketch, "E1901", {"start": v(-5.38, -7.51) * mm, "end": v(-5.48, -7.51) * mm});
            skLineSegment(sketch, "E1902", {"start": v(-5.48, -7.51) * mm, "end": v(-5.52, -7.52) * mm});
            skLineSegment(sketch, "E1903", {"start": v(-5.52, -7.52) * mm, "end": v(-5.55, -7.55) * mm});
            skLineSegment(sketch, "E1904", {"start": v(-5.55, -7.55) * mm, "end": v(-5.48, -7.62) * mm});
            skLineSegment(sketch, "E1905", {"start": v(-5.48, -7.62) * mm, "end": v(-5.43, -7.66) * mm});
            skLineSegment(sketch, "E1906", {"start": v(-5.43, -7.66) * mm, "end": v(-5.43, -7.72) * mm});
            skLineSegment(sketch, "E1907", {"start": v(-5.43, -7.72) * mm, "end": v(-5.46, -7.73) * mm});
            skLineSegment(sketch, "E1908", {"start": v(-5.46, -7.73) * mm, "end": v(-5.5, -7.73) * mm});
            skLineSegment(sketch, "E1909", {"start": v(-5.5, -7.73) * mm, "end": v(-5.57, -7.68) * mm});
            skLineSegment(sketch, "E1910", {"start": v(-5.57, -7.68) * mm, "end": v(-5.63, -7.61) * mm});
            skLineSegment(sketch, "E1911", {"start": v(-5.63, -7.61) * mm, "end": v(-5.65, -7.6) * mm});
            skLineSegment(sketch, "E1912", {"start": v(-5.65, -7.6) * mm, "end": v(-5.68, -7.6) * mm});
            skLineSegment(sketch, "E1913", {"start": v(-5.68, -7.6) * mm, "end": v(-5.73, -7.63) * mm});
            skLineSegment(sketch, "E1914", {"start": v(-5.73, -7.63) * mm, "end": v(-5.78, -7.63) * mm});
            skLineSegment(sketch, "E1915", {"start": v(-5.78, -7.63) * mm, "end": v(-5.83, -7.6) * mm});
            skLineSegment(sketch, "E1916", {"start": v(-5.83, -7.6) * mm, "end": v(-5.83, -7.55) * mm});
            skLineSegment(sketch, "E1917", {"start": v(-5.83, -7.55) * mm, "end": v(-5.83, -7.43) * mm});
            skLineSegment(sketch, "E1918", {"start": v(-5.83, -7.43) * mm, "end": v(-5.8, -7.4) * mm});
            skLineSegment(sketch, "E1919", {"start": v(-5.8, -7.4) * mm, "end": v(-5.76, -7.4) * mm});
            skLineSegment(sketch, "E1920", {"start": v(-5.76, -7.4) * mm, "end": v(-5.74, -7.45) * mm});
            skLineSegment(sketch, "E1921", {"start": v(-5.74, -7.45) * mm, "end": v(-5.7, -7.47) * mm});
            skLineSegment(sketch, "E1922", {"start": v(-5.7, -7.47) * mm, "end": v(-5.65, -7.47) * mm});
            skLineSegment(sketch, "E1923", {"start": v(-5.65, -7.47) * mm, "end": v(-5.61, -7.44) * mm});
            skLineSegment(sketch, "E1924", {"start": v(-5.61, -7.44) * mm, "end": v(-5.53, -7.44) * mm});
            skLineSegment(sketch, "E1925", {"start": v(-5.53, -7.44) * mm, "end": v(-5.53, -7.42) * mm});
            skLineSegment(sketch, "E1926", {"start": v(-5.53, -7.42) * mm, "end": v(-5.53, -7.38) * mm});
            skLineSegment(sketch, "E1927", {"start": v(-5.81, -6.97) * mm, "end": v(-5.75, -7.01) * mm});
            skLineSegment(sketch, "E1928", {"start": v(-5.75, -7.01) * mm, "end": v(-5.75, -7.08) * mm});
            skLineSegment(sketch, "E1929", {"start": v(-5.75, -7.08) * mm, "end": v(-5.81, -7.12) * mm});
            skLineSegment(sketch, "E1930", {"start": v(-5.81, -7.12) * mm, "end": v(-5.86, -7.07) * mm});
            skLineSegment(sketch, "E1931", {"start": v(-5.86, -7.07) * mm, "end": v(-5.87, -7.02) * mm});
            skLineSegment(sketch, "E1932", {"start": v(-5.98, -7.04) * mm, "end": v(-5.93, -6.96) * mm});
            skLineSegment(sketch, "E1933", {"start": v(-5.93, -6.96) * mm, "end": v(-5.93, -6.85) * mm});
            skLineSegment(sketch, "E1934", {"start": v(-5.93, -6.85) * mm, "end": v(-5.98, -6.85) * mm});
            skLineSegment(sketch, "E1935", {"start": v(-5.98, -6.85) * mm, "end": v(-6, -6.9) * mm});
            skLineSegment(sketch, "E1936", {"start": v(-6, -6.9) * mm, "end": v(-6.1, -6.9) * mm});
            skLineSegment(sketch, "E1937", {"start": v(-6.1, -6.9) * mm, "end": v(-6.17, -6.82) * mm});
            skLineSegment(sketch, "E1938", {"start": v(-6.17, -6.82) * mm, "end": v(-6.3, -6.79) * mm});
            skLineSegment(sketch, "E1939", {"start": v(-6.3, -6.79) * mm, "end": v(-6.38, -6.73) * mm});
            skLineSegment(sketch, "E1940", {"start": v(-6.38, -6.73) * mm, "end": v(-6.46, -6.59) * mm});
            skLineSegment(sketch, "E1941", {"start": v(-6.46, -6.59) * mm, "end": v(-6.6, -6.5) * mm});
            skLineSegment(sketch, "E1942", {"start": v(-6.6, -6.5) * mm, "end": v(-6.63, -6.51) * mm});
            skLineSegment(sketch, "E1943", {"start": v(-6.63, -6.51) * mm, "end": v(-6.6, -6.66) * mm});
            skLineSegment(sketch, "E1944", {"start": v(-6.6, -6.66) * mm, "end": v(-6.48, -6.79) * mm});
            skLineSegment(sketch, "E1945", {"start": v(-6.48, -6.79) * mm, "end": v(-6.37, -6.86) * mm});
            skLineSegment(sketch, "E1946", {"start": v(-6.37, -6.86) * mm, "end": v(-6.27, -6.93) * mm});
            skLineSegment(sketch, "E1947", {"start": v(-6.27, -6.93) * mm, "end": v(-6.13, -6.99) * mm});
            skLineSegment(sketch, "E1948", {"start": v(-6.13, -6.99) * mm, "end": v(-6.06, -7.03) * mm});
            skLineSegment(sketch, "E1949", {"start": v(4.6, -9.42) * mm, "end": v(4.7, -9.27) * mm});
            skLineSegment(sketch, "E1950", {"start": v(4.7, -9.27) * mm, "end": v(4.73, -9.15) * mm});
            skLineSegment(sketch, "E1951", {"start": v(4.73, -9.15) * mm, "end": v(4.9, -9.15) * mm});
            skLineSegment(sketch, "E1952", {"start": v(4.9, -9.15) * mm, "end": v(4.98, -9.09) * mm});
            skLineSegment(sketch, "E1953", {"start": v(4.98, -9.09) * mm, "end": v(5.1, -9.03) * mm});
            skLineSegment(sketch, "E1954", {"start": v(5.1, -9.03) * mm, "end": v(5.04, -9.17) * mm});
            skLineSegment(sketch, "E1955", {"start": v(5.04, -9.17) * mm, "end": v(4.94, -9.18) * mm});
            skLineSegment(sketch, "E1956", {"start": v(4.94, -9.18) * mm, "end": v(4.8, -9.31) * mm});
            skLineSegment(sketch, "E1957", {"start": v(4.8, -9.31) * mm, "end": v(4.73, -9.33) * mm});
            skLineSegment(sketch, "E1958", {"start": v(2.85, -10.57) * mm, "end": v(2.8, -10.7) * mm});
            skLineSegment(sketch, "E1959", {"start": v(2.8, -10.7) * mm, "end": v(2.75, -10.78) * mm});
            skLineSegment(sketch, "E1960", {"start": v(2.75, -10.78) * mm, "end": v(2.75, -10.83) * mm});
            skLineSegment(sketch, "E1961", {"start": v(2.75, -10.83) * mm, "end": v(2.78, -10.87) * mm});
            skLineSegment(sketch, "E1962", {"start": v(2.78, -10.87) * mm, "end": v(2.84, -10.87) * mm});
            skLineSegment(sketch, "E1963", {"start": v(2.84, -10.87) * mm, "end": v(2.88, -10.84) * mm});
            skLineSegment(sketch, "E1964", {"start": v(2.88, -10.84) * mm, "end": v(2.9, -10.8) * mm});
            skLineSegment(sketch, "E1965", {"start": v(2.9, -10.8) * mm, "end": v(2.88, -10.74) * mm});
            skLineSegment(sketch, "E1966", {"start": v(2.88, -10.74) * mm, "end": v(2.85, -10.57) * mm});
            skLineSegment(sketch, "E1967", {"start": v(4.6, -9.42) * mm, "end": v(4.73, -9.33) * mm});
            skLineSegment(sketch, "E1968", {"start": v(-5.53, -7.38) * mm, "end": v(-5.8, -7.2) * mm});
            skLineSegment(sketch, "E1969", {"start": v(-5.8, -7.2) * mm, "end": v(-6.09, -7.18) * mm});
            skLineSegment(sketch, "E1970", {"start": v(-6.09, -7.18) * mm, "end": v(-6.3, -7.08) * mm});
            skLineSegment(sketch, "E1971", {"start": v(-6.3, -7.08) * mm, "end": v(-6.34, -7.14) * mm});
            skLineSegment(sketch, "E1972", {"start": v(-6.34, -7.14) * mm, "end": v(-6.45, -7.05) * mm});
            skLineSegment(sketch, "E1973", {"start": v(-6.45, -7.05) * mm, "end": v(-6.71, -6.86) * mm});
            skLineSegment(sketch, "E1974", {"start": v(-6.71, -6.86) * mm, "end": v(-7, -6.56) * mm});
            skLineSegment(sketch, "E1975", {"start": v(-7, -6.56) * mm, "end": v(-7.4, -6.16) * mm});
            skLineSegment(sketch, "E1976", {"start": v(-7.4, -6.16) * mm, "end": v(-7.54, -6.12) * mm});
            skLineSegment(sketch, "E1977", {"start": v(-7.54, -6.12) * mm, "end": v(-7.58, -6.01) * mm});
            skLineSegment(sketch, "E1978", {"start": v(-7.58, -6.01) * mm, "end": v(-7.61, -5.98) * mm});
            skLineSegment(sketch, "E1979", {"start": v(-7.61, -5.98) * mm, "end": v(-7.65, -5.98) * mm});
            skLineSegment(sketch, "E1980", {"start": v(-7.65, -5.98) * mm, "end": v(-7.63, -6.07) * mm});
            skLineSegment(sketch, "E1981", {"start": v(-7.63, -6.07) * mm, "end": v(-7.67, -6.07) * mm});
            skLineSegment(sketch, "E1982", {"start": v(-7.67, -6.07) * mm, "end": v(-7.73, -6) * mm});
            skLineSegment(sketch, "E1983", {"start": v(-7.73, -6) * mm, "end": v(-7.82, -5.96) * mm});
            skLineSegment(sketch, "E1984", {"start": v(-7.82, -5.96) * mm, "end": v(-7.87, -5.9) * mm});
            skLineSegment(sketch, "E1985", {"start": v(-7.87, -5.9) * mm, "end": v(-7.98, -5.9) * mm});
            skLineSegment(sketch, "E1986", {"start": v(-7.98, -5.9) * mm, "end": v(-7.98, -5.94) * mm});
            skLineSegment(sketch, "E1987", {"start": v(-7.98, -5.94) * mm, "end": v(-7.8, -6.1) * mm});
            skLineSegment(sketch, "E1988", {"start": v(-7.8, -6.1) * mm, "end": v(-7.7, -6.25) * mm});
            skLineSegment(sketch, "E1989", {"start": v(-7.7, -6.25) * mm, "end": v(-7.73, -6.3) * mm});
            skLineSegment(sketch, "E1990", {"start": v(-7.73, -6.3) * mm, "end": v(-7.83, -6.23) * mm});
            skLineSegment(sketch, "E1991", {"start": v(-7.83, -6.23) * mm, "end": v(-8, -6.15) * mm});
            skLineSegment(sketch, "E1992", {"start": v(-8, -6.15) * mm, "end": v(-8.1, -6.06) * mm});
            skLineSegment(sketch, "E1993", {"start": v(-8.1, -6.06) * mm, "end": v(-8.1, -6) * mm});
            skLineSegment(sketch, "E1994", {"start": v(-8.1, -6) * mm, "end": v(-8.07, -5.97) * mm});
            skLineSegment(sketch, "E1995", {"start": v(-8.07, -5.97) * mm, "end": v(-8.07, -5.91) * mm});
            skLineSegment(sketch, "E1996", {"start": v(-8.07, -5.91) * mm, "end": v(-8.13, -5.86) * mm});
            skLineSegment(sketch, "E1997", {"start": v(-8.13, -5.86) * mm, "end": v(-8.2, -5.86) * mm});
            skLineSegment(sketch, "E1998", {"start": v(-8.2, -5.86) * mm, "end": v(-8.26, -5.97) * mm});
            skLineSegment(sketch, "E1999", {"start": v(-8.26, -5.97) * mm, "end": v(-8.32, -5.96) * mm});
            skLineSegment(sketch, "E2000", {"start": v(-8.32, -5.96) * mm, "end": v(-8.32, -5.87) * mm});
            skLineSegment(sketch, "E2001", {"start": v(-8.32, -5.87) * mm, "end": v(-8.38, -5.87) * mm});
            skLineSegment(sketch, "E2002", {"start": v(-8.38, -5.87) * mm, "end": v(-8.43, -6) * mm});
            skLineSegment(sketch, "E2003", {"start": v(-8.43, -6) * mm, "end": v(-8.48, -5.99) * mm});
            skLineSegment(sketch, "E2004", {"start": v(-8.48, -5.99) * mm, "end": v(-8.54, -5.94) * mm});
            skLineSegment(sketch, "E2005", {"start": v(-8.54, -5.94) * mm, "end": v(-8.58, -5.94) * mm});
            skLineSegment(sketch, "E2006", {"start": v(-8.58, -5.94) * mm, "end": v(-8.6, -5.97) * mm});
            skLineSegment(sketch, "E2007", {"start": v(-8.6, -5.97) * mm, "end": v(-8.64, -5.97) * mm});
            skLineSegment(sketch, "E2008", {"start": v(-8.64, -5.97) * mm, "end": v(-8.91, -5.73) * mm});
            skLineSegment(sketch, "E2009", {"start": v(-8.91, -5.73) * mm, "end": v(-9.12, -5.56) * mm});
            skLineSegment(sketch, "E2010", {"start": v(-9.12, -5.56) * mm, "end": v(-9.2, -5.53) * mm});
            skLineSegment(sketch, "E2011", {"start": v(-9.2, -5.53) * mm, "end": v(-9.52, -5.26) * mm});
            skLineSegment(sketch, "E2012", {"start": v(-9.52, -5.26) * mm, "end": v(-9.6, -5.24) * mm});
            skLineSegment(sketch, "E2013", {"start": v(-9.6, -5.24) * mm, "end": v(-9.81, -5.04) * mm});
            skLineSegment(sketch, "E2014", {"start": v(-9.81, -5.04) * mm, "end": v(-9.98, -4.8) * mm});
            skLineSegment(sketch, "E2015", {"start": v(-9.98, -4.8) * mm, "end": v(-10.02, -4.73) * mm});
            skLineSegment(sketch, "E2016", {"start": v(-10.02, -4.73) * mm, "end": v(-10.1, -4.7) * mm});
            skLineSegment(sketch, "E2017", {"start": v(-10.1, -4.7) * mm, "end": v(-10.16, -4.67) * mm});
            skLineSegment(sketch, "E2018", {"start": v(-10.16, -4.67) * mm, "end": v(-10.16, -4.6) * mm});
            skLineSegment(sketch, "E2019", {"start": v(-10.16, -4.6) * mm, "end": v(-10.13, -4.57) * mm});
            skLineSegment(sketch, "E2020", {"start": v(-10.13, -4.57) * mm, "end": v(-10.26, -4.44) * mm});
            skLineSegment(sketch, "E2021", {"start": v(-10.26, -4.44) * mm, "end": v(-10.33, -4.33) * mm});
            skLineSegment(sketch, "E2022", {"start": v(-10.33, -4.33) * mm, "end": v(-10.36, -4.23) * mm});
            skLineSegment(sketch, "E2023", {"start": v(-10.36, -4.23) * mm, "end": v(-10.4, -4.18) * mm});
            skLineSegment(sketch, "E2024", {"start": v(-10.4, -4.18) * mm, "end": v(-10.47, -4.15) * mm});
            skLineSegment(sketch, "E2025", {"start": v(-10.47, -4.15) * mm, "end": v(-10.53, -4.1) * mm});
            skLineSegment(sketch, "E2026", {"start": v(-10.53, -4.1) * mm, "end": v(-10.57, -4.1) * mm});
            skLineSegment(sketch, "E2027", {"start": v(-10.57, -4.1) * mm, "end": v(-10.6, -4.14) * mm});
            skLineSegment(sketch, "E2028", {"start": v(-10.6, -4.14) * mm, "end": v(-10.6, -4.2) * mm});
            skLineSegment(sketch, "E2029", {"start": v(-10.6, -4.2) * mm, "end": v(-10.56, -4.3) * mm});
            skLineSegment(sketch, "E2030", {"start": v(-10.56, -4.3) * mm, "end": v(-10.6, -4.32) * mm});
            skLineSegment(sketch, "E2031", {"start": v(-10.6, -4.32) * mm, "end": v(-10.68, -4.22) * mm});
            skLineSegment(sketch, "E2032", {"start": v(-10.68, -4.22) * mm, "end": v(-10.76, -4.12) * mm});
            skLineSegment(sketch, "E2033", {"start": v(-10.76, -4.12) * mm, "end": v(-10.79, -4.05) * mm});
            skLineSegment(sketch, "E2034", {"start": v(-10.79, -4.05) * mm, "end": v(-10.86, -3.97) * mm});
            skLineSegment(sketch, "E2035", {"start": v(-10.86, -3.97) * mm, "end": v(-10.9, -3.95) * mm});
            skLineSegment(sketch, "E2036", {"start": v(-10.9, -3.95) * mm, "end": v(-11, -3.92) * mm});
            skLineSegment(sketch, "E2037", {"start": v(-11, -3.92) * mm, "end": v(-11, -3.87) * mm});
            skLineSegment(sketch, "E2038", {"start": v(-11, -3.87) * mm, "end": v(-11.06, -3.83) * mm});
            skLineSegment(sketch, "E2039", {"start": v(-11.06, -3.83) * mm, "end": v(-11.05, -3.78) * mm});
            skLineSegment(sketch, "E2040", {"start": v(-11.05, -3.78) * mm, "end": v(-11.02, -3.77) * mm});
            skLineSegment(sketch, "E2041", {"start": v(-11.02, -3.77) * mm, "end": v(-11.02, -3.73) * mm});
            skLineSegment(sketch, "E2042", {"start": v(-11.02, -3.73) * mm, "end": v(-11.06, -3.7) * mm});
            skLineSegment(sketch, "E2043", {"start": v(-11.06, -3.7) * mm, "end": v(-11.1, -3.72) * mm});
            skLineSegment(sketch, "E2044", {"start": v(-11.1, -3.72) * mm, "end": v(-11.09, -3.77) * mm});
            skLineSegment(sketch, "E2045", {"start": v(-11.09, -3.77) * mm, "end": v(-11.14, -3.77) * mm});
            skLineSegment(sketch, "E2046", {"start": v(-11.14, -3.77) * mm, "end": v(-11.16, -3.74) * mm});
            skLineSegment(sketch, "E2047", {"start": v(-11.16, -3.74) * mm, "end": v(-11.2, -3.72) * mm});
            skLineSegment(sketch, "E2048", {"start": v(-11.2, -3.72) * mm, "end": v(-11.25, -3.78) * mm});
            skLineSegment(sketch, "E2049", {"start": v(-11.25, -3.78) * mm, "end": v(-11.3, -3.79) * mm});
            skLineSegment(sketch, "E2050", {"start": v(-11.3, -3.79) * mm, "end": v(-11.32, -3.73) * mm});
            skLineSegment(sketch, "E2051", {"start": v(-11.32, -3.73) * mm, "end": v(-11.28, -3.66) * mm});
            skLineSegment(sketch, "E2052", {"start": v(-11.28, -3.66) * mm, "end": v(-11.26, -3.58) * mm});
            skLineSegment(sketch, "E2053", {"start": v(-11.26, -3.58) * mm, "end": v(-11.36, -3.5) * mm});
            skLineSegment(sketch, "E2054", {"start": v(-11.36, -3.5) * mm, "end": v(-11.47, -3.39) * mm});
            skLineSegment(sketch, "E2055", {"start": v(-11.47, -3.39) * mm, "end": v(-11.5, -3.4) * mm});
            skLineSegment(sketch, "E2056", {"start": v(-11.5, -3.4) * mm, "end": v(-11.49, -3.46) * mm});
            skLineSegment(sketch, "E2057", {"start": v(-11.49, -3.46) * mm, "end": v(-11.52, -3.47) * mm});
            skLineSegment(sketch, "E2058", {"start": v(-11.52, -3.47) * mm, "end": v(-11.55, -3.44) * mm});
            skLineSegment(sketch, "E2059", {"start": v(-11.55, -3.44) * mm, "end": v(-11.58, -3.42) * mm});
            skLineSegment(sketch, "E2060", {"start": v(-11.58, -3.42) * mm, "end": v(-11.65, -3.4) * mm});
            skLineSegment(sketch, "E2061", {"start": v(-11.65, -3.4) * mm, "end": v(-11.74, -3.33) * mm});
            skLineSegment(sketch, "E2062", {"start": v(-11.74, -3.33) * mm, "end": v(-11.82, -3.25) * mm});
            skLineSegment(sketch, "E2063", {"start": v(-11.82, -3.25) * mm, "end": v(-11.87, -3.16) * mm});
            skLineSegment(sketch, "E2064", {"start": v(-11.87, -3.16) * mm, "end": v(-11.87, -3.05) * mm});
            skLineSegment(sketch, "E2065", {"start": v(-11.87, -3.05) * mm, "end": v(-11.94, -2.98) * mm});
            skLineSegment(sketch, "E2066", {"start": v(-11.94, -2.98) * mm, "end": v(-11.99, -2.98) * mm});
            skLineSegment(sketch, "E2067", {"start": v(-11.99, -2.98) * mm, "end": v(-12.04, -3.05) * mm});
            skLineSegment(sketch, "E2068", {"start": v(-12.04, -3.05) * mm, "end": v(-12.07, -3.13) * mm});
            skLineSegment(sketch, "E2069", {"start": v(-12.07, -3.13) * mm, "end": v(-12.11, -3.15) * mm});
            skLineSegment(sketch, "E2070", {"start": v(-12.11, -3.15) * mm, "end": v(-12.13, -3.13) * mm});
            skLineSegment(sketch, "E2071", {"start": v(-12.13, -3.13) * mm, "end": v(-12.13, -3.06) * mm});
            skLineSegment(sketch, "E2072", {"start": v(-12.13, -3.06) * mm, "end": v(-12.19, -3.02) * mm});
            skLineSegment(sketch, "E2073", {"start": v(-12.19, -3.02) * mm, "end": v(-12.15, -2.97) * mm});
            skLineSegment(sketch, "E2074", {"start": v(-12.15, -2.97) * mm, "end": v(-12.11, -2.91) * mm});
            skLineSegment(sketch, "E2075", {"start": v(-12.11, -2.91) * mm, "end": v(-12.1, -2.88) * mm});
            skLineSegment(sketch, "E2076", {"start": v(-12.1, -2.88) * mm, "end": v(-12.14, -2.84) * mm});
            skLineSegment(sketch, "E2077", {"start": v(-12.14, -2.84) * mm, "end": v(-12.21, -2.83) * mm});
            skLineSegment(sketch, "E2078", {"start": v(-12.21, -2.83) * mm, "end": v(-12.37, -2.67) * mm});
            skLineSegment(sketch, "E2079", {"start": v(-12.37, -2.67) * mm, "end": v(-12.43, -2.6) * mm});
            skLineSegment(sketch, "E2080", {"start": v(-12.43, -2.6) * mm, "end": v(-12.51, -2.6) * mm});
            skLineSegment(sketch, "E2081", {"start": v(-12.51, -2.6) * mm, "end": v(-12.53, -2.63) * mm});
            skLineSegment(sketch, "E2082", {"start": v(-12.53, -2.63) * mm, "end": v(-12.6, -2.64) * mm});
            skLineSegment(sketch, "E2083", {"start": v(-12.6, -2.64) * mm, "end": v(-12.62, -2.62) * mm});
            skLineSegment(sketch, "E2084", {"start": v(-12.62, -2.62) * mm, "end": v(-12.6, -2.59) * mm});
            skLineSegment(sketch, "E2085", {"start": v(-12.6, -2.59) * mm, "end": v(-12.54, -2.57) * mm});
            skLineSegment(sketch, "E2086", {"start": v(-12.54, -2.57) * mm, "end": v(-12.52, -2.54) * mm});
            skLineSegment(sketch, "E2087", {"start": v(-12.52, -2.54) * mm, "end": v(-12.48, -2.54) * mm});
            skLineSegment(sketch, "E2088", {"start": v(-12.48, -2.54) * mm, "end": v(-12.5, -2.49) * mm});
            skLineSegment(sketch, "E2089", {"start": v(-12.5, -2.49) * mm, "end": v(-12.53, -2.46) * mm});
            skLineSegment(sketch, "E2090", {"start": v(-12.53, -2.46) * mm, "end": v(-12.58, -2.45) * mm});
            skLineSegment(sketch, "E2091", {"start": v(-12.58, -2.45) * mm, "end": v(-12.6, -2.5) * mm});
            skLineSegment(sketch, "E2092", {"start": v(-12.6, -2.5) * mm, "end": v(-12.66, -2.55) * mm});
            skLineSegment(sketch, "E2093", {"start": v(-12.66, -2.55) * mm, "end": v(-12.7, -2.62) * mm});
            skLineSegment(sketch, "E2094", {"start": v(-12.7, -2.62) * mm, "end": v(-12.74, -2.68) * mm});
            skLineSegment(sketch, "E2095", {"start": v(-12.74, -2.68) * mm, "end": v(-12.74, -2.74) * mm});
            skLineSegment(sketch, "E2096", {"start": v(-12.74, -2.74) * mm, "end": v(-12.7, -2.77) * mm});
            skLineSegment(sketch, "E2097", {"start": v(-12.7, -2.77) * mm, "end": v(-12.66, -2.75) * mm});
            skLineSegment(sketch, "E2098", {"start": v(-12.66, -2.75) * mm, "end": v(-12.6, -2.75) * mm});
            skLineSegment(sketch, "E2099", {"start": v(-12.6, -2.75) * mm, "end": v(-12.6, -2.87) * mm});
            skLineSegment(sketch, "E2100", {"start": v(-12.6, -2.87) * mm, "end": v(-12.66, -2.93) * mm});
            skLineSegment(sketch, "E2101", {"start": v(-12.66, -2.93) * mm, "end": v(-12.75, -2.93) * mm});
            skLineSegment(sketch, "E2102", {"start": v(-12.75, -2.93) * mm, "end": v(-12.74, -2.9) * mm});
            skLineSegment(sketch, "E2103", {"start": v(-12.74, -2.9) * mm, "end": v(-12.77, -2.85) * mm});
            skLineSegment(sketch, "E2104", {"start": v(-12.77, -2.85) * mm, "end": v(-12.85, -2.87) * mm});
            skLineSegment(sketch, "E2105", {"start": v(-12.85, -2.87) * mm, "end": v(-12.9, -2.97) * mm});
            skLineSegment(sketch, "E2106", {"start": v(-12.9, -2.97) * mm, "end": v(-12.9, -3.04) * mm});
            skLineSegment(sketch, "E2107", {"start": v(-12.9, -3.04) * mm, "end": v(-12.87, -3.1) * mm});
            skLineSegment(sketch, "E2108", {"start": v(-12.87, -3.1) * mm, "end": v(-12.85, -3.16) * mm});
            skLineSegment(sketch, "E2109", {"start": v(-12.85, -3.16) * mm, "end": v(-12.9, -3.17) * mm});
            skLineSegment(sketch, "E2110", {"start": v(-12.9, -3.17) * mm, "end": v(-12.93, -3.13) * mm});
            skLineSegment(sketch, "E2111", {"start": v(-12.93, -3.13) * mm, "end": v(-12.95, -3.1) * mm});
            skLineSegment(sketch, "E2112", {"start": v(-12.95, -3.1) * mm, "end": v(-13, -3.09) * mm});
            skLineSegment(sketch, "E2113", {"start": v(-13, -3.09) * mm, "end": v(-13.06, -3.15) * mm});
            skLineSegment(sketch, "E2114", {"start": v(-13.06, -3.15) * mm, "end": v(-13.14, -3.23) * mm});
            skLineSegment(sketch, "E2115", {"start": v(-13.14, -3.23) * mm, "end": v(-13.22, -3.3) * mm});
            skLineSegment(sketch, "E2116", {"start": v(-13.22, -3.3) * mm, "end": v(-13.33, -3.35) * mm});
            skLineSegment(sketch, "E2117", {"start": v(-13.33, -3.35) * mm, "end": v(-13.38, -3.38) * mm});
            skLineSegment(sketch, "E2118", {"start": v(-13.38, -3.38) * mm, "end": v(-13.53, -3.48) * mm});
            skLineSegment(sketch, "E2119", {"start": v(-13.53, -3.48) * mm, "end": v(-13.56, -3.45) * mm});
            skLineSegment(sketch, "E2120", {"start": v(-13.56, -3.45) * mm, "end": v(-13.44, -3.33) * mm});
            skLineSegment(sketch, "E2121", {"start": v(-13.44, -3.33) * mm, "end": v(-13.43, -3.24) * mm});
            skLineSegment(sketch, "E2122", {"start": v(-13.43, -3.24) * mm, "end": v(-13.41, -3.22) * mm});
            skLineSegment(sketch, "E2123", {"start": v(-13.41, -3.22) * mm, "end": v(-13.42, -3.16) * mm});
            skLineSegment(sketch, "E2124", {"start": v(-13.42, -3.16) * mm, "end": v(-13.44, -3.12) * mm});
            skLineSegment(sketch, "E2125", {"start": v(-13.44, -3.12) * mm, "end": v(-13.5, -3.11) * mm});
            skLineSegment(sketch, "E2126", {"start": v(-13.5, -3.11) * mm, "end": v(-13.56, -3.16) * mm});
            skLineSegment(sketch, "E2127", {"start": v(-13.56, -3.16) * mm, "end": v(-13.6, -3.17) * mm});
            skLineSegment(sketch, "E2128", {"start": v(-13.6, -3.17) * mm, "end": v(-13.64, -3.13) * mm});
            skLineSegment(sketch, "E2129", {"start": v(-13.64, -3.13) * mm, "end": v(-13.7, -3.13) * mm});
            skLineSegment(sketch, "E2130", {"start": v(-13.7, -3.13) * mm, "end": v(-13.87, -3.29) * mm});
            skLineSegment(sketch, "E2131", {"start": v(-13.87, -3.29) * mm, "end": v(-14.02, -3.3) * mm});
            skLineSegment(sketch, "E2132", {"start": v(-14.02, -3.3) * mm, "end": v(-14.12, -3.28) * mm});
            skLineSegment(sketch, "E2133", {"start": v(-14.12, -3.28) * mm, "end": v(-14.26, -3.29) * mm});
            skLineSegment(sketch, "E2134", {"start": v(-14.26, -3.29) * mm, "end": v(-14.32, -3.33) * mm});
            skLineSegment(sketch, "E2135", {"start": v(-14.32, -3.33) * mm, "end": v(-14.43, -3.43) * mm});
            skLineSegment(sketch, "E2136", {"start": v(-14.43, -3.43) * mm, "end": v(-14.46, -3.5) * mm});
            skLineSegment(sketch, "E2137", {"start": v(-14.46, -3.5) * mm, "end": v(-14.52, -3.54) * mm});
            skLineSegment(sketch, "E2138", {"start": v(-14.52, -3.54) * mm, "end": v(-14.6, -3.58) * mm});
            skLineSegment(sketch, "E2139", {"start": v(-14.6, -3.58) * mm, "end": v(-14.68, -3.56) * mm});
            skLineSegment(sketch, "E2140", {"start": v(-14.68, -3.56) * mm, "end": v(-14.74, -3.55) * mm});
            skLineSegment(sketch, "E2141", {"start": v(-14.74, -3.55) * mm, "end": v(-15, -3.69) * mm});
            skLineSegment(sketch, "E2142", {"start": v(-15, -3.69) * mm, "end": v(-15.05, -3.7) * mm});
            skLineSegment(sketch, "E2143", {"start": v(-15.05, -3.7) * mm, "end": v(-15.12, -3.7) * mm});
            skLineSegment(sketch, "E2144", {"start": v(-15.12, -3.7) * mm, "end": v(-15.24, -3.84) * mm});
            skLineSegment(sketch, "E2145", {"start": v(-15.24, -3.84) * mm, "end": v(-15.36, -3.88) * mm});
            skLineSegment(sketch, "E2146", {"start": v(-15.36, -3.88) * mm, "end": v(-15.5, -3.97) * mm});
            skLineSegment(sketch, "E2147", {"start": v(-15.5, -3.97) * mm, "end": v(-15.54, -3.95) * mm});
            skLineSegment(sketch, "E2148", {"start": v(-15.54, -3.95) * mm, "end": v(-15.55, -3.9) * mm});
            skLineSegment(sketch, "E2149", {"start": v(-15.55, -3.9) * mm, "end": v(-15.5, -3.84) * mm});
            skLineSegment(sketch, "E2150", {"start": v(-15.5, -3.84) * mm, "end": v(-15.5, -3.72) * mm});
            skLineSegment(sketch, "E2151", {"start": v(-15.5, -3.72) * mm, "end": v(-15.53, -3.64) * mm});
            skLineSegment(sketch, "E2152", {"start": v(-15.53, -3.64) * mm, "end": v(-15.42, -3.49) * mm});
            skLineSegment(sketch, "E2153", {"start": v(-15.42, -3.49) * mm, "end": v(-15.38, -3.34) * mm});
            skLineSegment(sketch, "E2154", {"start": v(-15.38, -3.34) * mm, "end": v(-15.34, -3.28) * mm});
            skLineSegment(sketch, "E2155", {"start": v(-15.34, -3.28) * mm, "end": v(-15.2, -3.14) * mm});
            skLineSegment(sketch, "E2156", {"start": v(-15.2, -3.14) * mm, "end": v(-15.16, -3.02) * mm});
            skLineSegment(sketch, "E2157", {"start": v(-15.16, -3.02) * mm, "end": v(-15.2, -2.85) * mm});
            skLineSegment(sketch, "E2158", {"start": v(-15.2, -2.85) * mm, "end": v(-15.16, -2.83) * mm});
            skLineSegment(sketch, "E2159", {"start": v(-15.16, -2.83) * mm, "end": v(-15.13, -2.86) * mm});
            skLineSegment(sketch, "E2160", {"start": v(-15.13, -2.86) * mm, "end": v(-15.1, -2.87) * mm});
            skLineSegment(sketch, "E2161", {"start": v(-15.1, -2.87) * mm, "end": v(-15.08, -2.72) * mm});
            skLineSegment(sketch, "E2162", {"start": v(-15.08, -2.72) * mm, "end": v(-15.04, -2.6) * mm});
            skLineSegment(sketch, "E2163", {"start": v(-15.04, -2.6) * mm, "end": v(-14.9, -2.43) * mm});
            skLineSegment(sketch, "E2164", {"start": v(-14.9, -2.43) * mm, "end": v(-14.82, -2.25) * mm});
            skLineSegment(sketch, "E2165", {"start": v(-14.82, -2.25) * mm, "end": v(-14.79, -2.06) * mm});
            skLineSegment(sketch, "E2166", {"start": v(-14.79, -2.06) * mm, "end": v(-14.72, -2.02) * mm});
            skLineSegment(sketch, "E2167", {"start": v(-14.72, -2.02) * mm, "end": v(-14.67, -1.89) * mm});
            skLineSegment(sketch, "E2168", {"start": v(-14.67, -1.89) * mm, "end": v(-14.62, -1.72) * mm});
            skLineSegment(sketch, "E2169", {"start": v(-14.62, -1.72) * mm, "end": v(-14.56, -1.61) * mm});
            skLineSegment(sketch, "E2170", {"start": v(-14.56, -1.61) * mm, "end": v(-14.55, -1.5) * mm});
            skLineSegment(sketch, "E2171", {"start": v(-14.55, -1.5) * mm, "end": v(-14.53, -1.46) * mm});
            skLineSegment(sketch, "E2172", {"start": v(-14.53, -1.46) * mm, "end": v(-14.57, -1.37) * mm});
            skLineSegment(sketch, "E2173", {"start": v(-14.57, -1.37) * mm, "end": v(-14.65, -1.28) * mm});
            skLineSegment(sketch, "E2174", {"start": v(-14.65, -1.28) * mm, "end": v(-14.66, -1.2) * mm});
            skLineSegment(sketch, "E2175", {"start": v(-14.66, -1.2) * mm, "end": v(-14.64, -1.12) * mm});
            skLineSegment(sketch, "E2176", {"start": v(-14.64, -1.12) * mm, "end": v(-14.58, -1.04) * mm});
            skLineSegment(sketch, "E2177", {"start": v(-14.58, -1.04) * mm, "end": v(-14.53, -0.97) * mm});
            skLineSegment(sketch, "E2178", {"start": v(-14.53, -0.97) * mm, "end": v(-14.52, -0.79) * mm});
            skLineSegment(sketch, "E2179", {"start": v(-14.52, -0.79) * mm, "end": v(-14.44, -0.62) * mm});
            skLineSegment(sketch, "E2180", {"start": v(-14.44, -0.62) * mm, "end": v(-14.37, -0.48) * mm});
            skLineSegment(sketch, "E2181", {"start": v(-14.37, -0.48) * mm, "end": v(-14.36, -0.37) * mm});
            skLineSegment(sketch, "E2182", {"start": v(-14.36, -0.37) * mm, "end": v(-14.28, -0.32) * mm});
            skLineSegment(sketch, "E2183", {"start": v(-14.28, -0.32) * mm, "end": v(-14.26, -0.22) * mm});
            skLineSegment(sketch, "E2184", {"start": v(-14.26, -0.22) * mm, "end": v(-14.3, -0.15) * mm});
            skLineSegment(sketch, "E2185", {"start": v(-14.3, -0.15) * mm, "end": v(-14.32, -0.11) * mm});
            skLineSegment(sketch, "E2186", {"start": v(-14.32, -0.11) * mm, "end": v(-14.39, -0.1) * mm});
            skLineSegment(sketch, "E2187", {"start": v(-14.39, -0.1) * mm, "end": v(-14.5, 0) * mm});
            skLineSegment(sketch, "E2188", {"start": v(0, -7.5) * mm, "end": v(1.36, -5.12) * mm});
            skLineSegment(sketch, "E2189", {"start": v(1.36, -5.12) * mm, "end": v(2.42, -3.17) * mm});
            skLineSegment(sketch, "E2190", {"start": v(2.42, -3.17) * mm, "end": v(4.03, 0.03) * mm});
            skLineSegment(sketch, "E2191", {"start": v(4.03, 0.03) * mm, "end": v(4.64, 1.08) * mm});
            skLineSegment(sketch, "E2192", {"start": v(4.64, 1.08) * mm, "end": v(5.5, 2.75) * mm});
            skLineSegment(sketch, "E2193", {"start": v(5.5, 2.75) * mm, "end": v(5.64, 3.12) * mm});
            skLineSegment(sketch, "E2194", {"start": v(5.64, 3.12) * mm, "end": v(5.65, 3.4) * mm});
            skLineSegment(sketch, "E2195", {"start": v(5.65, 3.4) * mm, "end": v(5.37, 3.84) * mm});
            skLineSegment(sketch, "E2196", {"start": v(5.37, 3.84) * mm, "end": v(4.75, 4.63) * mm});
            skLineSegment(sketch, "E2197", {"start": v(4.75, 4.63) * mm, "end": v(3.77, 5.71) * mm});
            skLineSegment(sketch, "E2198", {"start": v(3.77, 5.71) * mm, "end": v(2.1, 7.47) * mm});
            skLineSegment(sketch, "E2199", {"start": v(2.1, 7.47) * mm, "end": v(1.05, 8.54) * mm});
            skLineSegment(sketch, "E2200", {"start": v(1.05, 8.54) * mm, "end": v(-0.04, 9.67) * mm});
            skLineSegment(sketch, "E2201", {"start": v(-0.04, 9.67) * mm, "end": v(-1.28, 8.43) * mm});
            skLineSegment(sketch, "E2202", {"start": v(-1.28, 8.43) * mm, "end": v(-2.62, 6.93) * mm});
            skLineSegment(sketch, "E2203", {"start": v(-2.62, 6.93) * mm, "end": v(-3.54, 5.97) * mm});
            skLineSegment(sketch, "E2204", {"start": v(-3.54, 5.97) * mm, "end": v(-4.53, 4.84) * mm});
            skLineSegment(sketch, "E2205", {"start": v(-4.53, 4.84) * mm, "end": v(-5.44, 3.92) * mm});
            skLineSegment(sketch, "E2206", {"start": v(-5.44, 3.92) * mm, "end": v(-5.65, 3.66) * mm});
            skLineSegment(sketch, "E2207", {"start": v(-5.65, 3.66) * mm, "end": v(-5.77, 3.4) * mm});
            skLineSegment(sketch, "E2208", {"start": v(-5.77, 3.4) * mm, "end": v(-5.78, 3.19) * mm});
            skLineSegment(sketch, "E2209", {"start": v(-5.78, 3.19) * mm, "end": v(-4.96, 1.5) * mm});
            skLineSegment(sketch, "E2210", {"start": v(-4.96, 1.5) * mm, "end": v(-4.16, -0.01) * mm});
            skLineSegment(sketch, "E2211", {"start": v(-4.16, -0.01) * mm, "end": v(-3.62, -1.15) * mm});
            skLineSegment(sketch, "E2212", {"start": v(-3.62, -1.15) * mm, "end": v(-3.28, -1.76) * mm});
            skLineSegment(sketch, "E2213", {"start": v(-3.28, -1.76) * mm, "end": v(-3.02, -2.13) * mm});
            skLineSegment(sketch, "E2214", {"start": v(-3.02, -2.13) * mm, "end": v(-2.55, -3.05) * mm});
            skLineSegment(sketch, "E2215", {"start": v(-2.55, -3.05) * mm, "end": v(-2.25, -3.75) * mm});
            skLineSegment(sketch, "E2216", {"start": v(-2.25, -3.75) * mm, "end": v(-1.98, -4.26) * mm});
            skLineSegment(sketch, "E2217", {"start": v(-1.98, -4.26) * mm, "end": v(-1.54, -4.98) * mm});
            skLineSegment(sketch, "E2218", {"start": v(-1.54, -4.98) * mm, "end": v(-1.2, -5.54) * mm});
            skLineSegment(sketch, "E2219", {"start": v(-1.2, -5.54) * mm, "end": v(-0.89, -6.07) * mm});
            skLineSegment(sketch, "E2220", {"start": v(-0.89, -6.07) * mm, "end": v(-0.54, -6.7) * mm});
            skLineSegment(sketch, "E2221", {"start": v(-0.54, -6.7) * mm, "end": v(-0.23, -7.23) * mm});
            skLineSegment(sketch, "E2222", {"start": v(-0.23, -7.23) * mm, "end": v(-0.07, -7.48) * mm});
            skLineSegment(sketch, "E2223", {"start": v(-0.07, -7.48) * mm, "end": v(0, -7.5) * mm});
            skLineSegment(sketch, "E2224", {"start": v(-6.06, -7.03) * mm, "end": v(-5.98, -7.04) * mm});
            skLineSegment(sketch, "E2225", {"start": v(-5.87, -7.02) * mm, "end": v(-5.81, -6.97) * mm});
            skSolve(sketch);
        }
        {
            var Q0;
            Q0=makeQuery(id+"F0.imprint","IMPRINT",FACE,{"disambiguationData":[TD([[makeQuery(id+"F0.imprint","IMPRINT",EDGE,{"derivedFrom":sQuery(id+"F0.wireOp",EDGE,"E1958")}),1.0]])]});
            var Q1;
            Q1=makeQuery(id+"F0.imprint","IMPRINT",FACE,{"disambiguationData":[TD([[makeQuery(id+"F0.imprint","IMPRINT",EDGE,{"derivedFrom":sQuery(id+"F0.wireOp",EDGE,"E1949")}),-1.0]])]});
            var Q2;
            Q2=makeQuery(id+"F0.imprint","IMPRINT",FACE,{"disambiguationData":[TD([[makeQuery(id+"F0.imprint","IMPRINT",EDGE,{"derivedFrom":sQuery(id+"F0.wireOp",EDGE,"E699")}),1.0]])]});
            var Q3;
            Q3=makeQuery(id+"F0.imprint","IMPRINT",FACE,{"disambiguationData":[TD([[makeQuery(id+"F0.imprint","IMPRINT",EDGE,{"derivedFrom":sQuery(id+"F0.wireOp",EDGE,"E658")}),-1.0]])]});
            var Q4;
            Q4=makeQuery(id+"F0.imprint","IMPRINT",FACE,{"disambiguationData":[TD([[makeQuery(id+"F0.imprint","IMPRINT",EDGE,{"derivedFrom":sQuery(id+"F0.wireOp",EDGE,"E649")}),-1.0]])]});
            var Q5;
            Q5=makeQuery(id+"F0.imprint","IMPRINT",FACE,{"disambiguationData":[TD([[makeQuery(id+"F0.imprint","IMPRINT",EDGE,{"derivedFrom":sQuery(id+"F0.wireOp",EDGE,"E1")}),-1.0]])]});
            var Q6;
            Q6=makeQuery(id+"F0.imprint","IMPRINT",FACE,{"disambiguationData":[TD([[makeQuery(id+"F0.imprint","IMPRINT",EDGE,{"derivedFrom":sQuery(id+"F0.wireOp",EDGE,"E353")}),-1.0]])]});
            extrude(context, id + "F1", {"entities" : qUnion([Q0, Q1, Q2, Q3, Q4, Q5, Q6]), "depth" : 2.5 * mm, "offsetDistance" : 25.4 * mm});
        }
        {
            var Q0;
            Q0=qCreatedBy(makeId("Top.planeOp"),FACE);
            var sketch = newSketch(context, id + "F2", { "sketchPlane" : qUnion([Q0])});
            skCircle(sketch, "E2226", {"center": v(0, 0) * mm, "radius": 20 * mm});
            skCircle(sketch, "E2227", {"center": v(0, 0) * mm, "radius": 18.8 * mm});
            skSolve(sketch);
        }
        {
            var Q0;
            Q0=makeQuery(id+"F2.imprint","IMPRINT",FACE,{"disambiguationData":[TD([[makeQuery(id+"F2.imprint","IMPRINT",EDGE,{"derivedFrom":sQuery(id+"F2.wireOp",EDGE,"E2226")}),1.0]])]});
            extrude(context, id + "F3", {"entities" : qUnion([Q0]), "depth" : 2.5 * mm, "offsetDistance" : 25.4 * mm});
        }
        {
            var Q0;
            Q0=makeQuery(id+"F2.imprint","IMPRINT",FACE,{"disambiguationData":[TD([[makeQuery(id+"F2.imprint","IMPRINT",EDGE,{"derivedFrom":sQuery(id+"F2.wireOp",EDGE,"E2227")}),1.0]])]});
            var Q1;
            Q1=makeQuery(id+"F2.imprint","IMPRINT",FACE,{"disambiguationData":[TD([[makeQuery(id+"F2.imprint","IMPRINT",EDGE,{"derivedFrom":sQuery(id+"F2.wireOp",EDGE,"E2226")}),1.0]])]});
            extrude(context, id + "F4", {"entities" : qUnion([Q0, Q1]), "depth" : -2.5 * mm, "offsetDistance" : 25.4 * mm});
        }
    });
